FCSTD DOCUMENT  (FreeCAD 0.21R)
Label: MMU
License: All rights reserved
LicenseURL: http://en.wikipedia.org/wiki/All_rights_reserved
objects: Sketcher::SketchObject×75, Part::Feature×72, PartDesign::Pad×33, PartDesign::Pocket×28, PartDesign::Body×21, App::Part×17, Part::FeaturePython×10, PartDesign::Chamfer×8, PartDesign::PolarPattern×5, Mesh::Feature×2, PartDesign::FeatureBase×2, PartDesign::Groove×1, Spreadsheet::Sheet×1, PartDesign::AdditiveLoft×1, PartDesign::SubtractivePipe×1, PartDesign::Fillet×1
note: 331 computed .brp shape members not serialized (recipe doc carries the construction recipe); baked Part::Feature solids carry a one-line shape summary decoded from their .brp

FEATURE [Sketcher::SketchObject] Sketch
  FullyConstrained = true
  MapMode = 5
  Support = -> [XY_Plane]
  expr: Constraints[33] = 34mm
  expr: Constraints[46] = 6mm
  expr: Constraints[47] = Spreadsheet.FilamentTopPathOffset
  expr: Constraints[7] = 2mm
  sketch-geometry (21):
    g0: Circle CenterX=0 CenterY=0 CenterZ=0 NormalX=0 NormalY=0 NormalZ=1 AngleXU=0 Radius=17
    g1: Circle CenterX=0 CenterY=13.208 CenterZ=0 NormalX=0 NormalY=0 NormalZ=1 AngleXU=0 Radius=1
    g2: Circle CenterX=0 CenterY=-13.208 CenterZ=0 NormalX=0 NormalY=0 NormalZ=1 AngleXU=0 Radius=1
    g3: Circle CenterX=-11.4385 CenterY=6.604 CenterZ=0 NormalX=0 NormalY=0 NormalZ=1 AngleXU=0 Radius=1
    g4: Circle CenterX=11.4385 CenterY=6.604 CenterZ=0 NormalX=0 NormalY=0 NormalZ=1 AngleXU=0 Radius=1
    g5: Circle CenterX=11.4385 CenterY=-6.604 CenterZ=0 NormalX=0 NormalY=0 NormalZ=1 AngleXU=0 Radius=1
    g6: Circle CenterX=-11.4385 CenterY=-6.604 CenterZ=0 NormalX=0 NormalY=0 NormalZ=1 AngleXU=0 Radius=1
    g7: LineSegment StartX=0 StartY=13.208 StartZ=0 EndX=-11.4385 EndY=6.604 EndZ=0
    g8: LineSegment StartX=-11.4385 StartY=6.604 StartZ=0 EndX=-11.4385 EndY=-6.604 EndZ=0
    g9: LineSegment StartX=-11.4385 StartY=-6.604 StartZ=0 EndX=0 EndY=-13.208 EndZ=0
    g10: LineSegment StartX=0 StartY=-13.208 StartZ=0 EndX=11.4385 EndY=-6.604 EndZ=0
    g11: LineSegment StartX=11.4385 StartY=-6.604 StartZ=0 EndX=11.4385 EndY=6.604 EndZ=0
    g12: LineSegment StartX=11.4385 StartY=6.604 StartZ=0 EndX=0 EndY=13.208 EndZ=0
    g13: Circle CenterX=0 CenterY=0 CenterZ=0 NormalX=0 NormalY=0 NormalZ=1 AngleXU=0 Radius=13.208
    g14: GeomPoint X=0 Y=17 Z=0
    g15: Circle CenterX=-11.4385 CenterY=6.604 CenterZ=0 NormalX=0 NormalY=0 NormalZ=1 AngleXU=0 Radius=3
    g16: Circle CenterX=0 CenterY=13.208 CenterZ=0 NormalX=0 NormalY=0 NormalZ=1 AngleXU=0 Radius=3
    g17: Circle CenterX=11.4385 CenterY=6.604 CenterZ=0 NormalX=0 NormalY=0 NormalZ=1 AngleXU=0 Radius=3
    g18: Circle CenterX=-11.4385 CenterY=-6.604 CenterZ=0 NormalX=0 NormalY=0 NormalZ=1 AngleXU=0 Radius=3
    g19: Circle CenterX=0 CenterY=-13.208 CenterZ=0 NormalX=0 NormalY=0 NormalZ=1 AngleXU=0 Radius=3
    g20: Circle CenterX=11.4385 CenterY=-6.604 CenterZ=0 NormalX=0 NormalY=0 NormalZ=1 AngleXU=0 Radius=3
  constraints (44):
    c: Coincident(g0,g-1)
    c: PointOnObject(g1,g-2)
    c: PointOnObject(g2,g-2)
    c: Equal(g3,g1)
    c: Equal(g5,g2)
    c: Equal(g2,g6)
    c: Equal(g6,g3)
    c: Diameter(g1) = 2
    c: Coincident(g7,g8)
    c: Coincident(g8,g9)
    c: Coincident(g9,g10)
    c: Coincident(g10,g11)
    c: Coincident(g11,g12)
    c: Coincident(g12,g7)
    c: Equal(g7, g8-g12) x5
    c: PointOnObject(g7,g13)
    c: PointOnObject(g8,g13)
    c: PointOnObject(g9,g13)
    c: PointOnObject(g10,g13)
    c: PointOnObject(g12,g13)
    c: Coincident(g13,g0)
    c: Coincident(g12,g1)
    c: Coincident(g3,g7)
    c: Coincident(g8,g6)
    c: Coincident(g2,g9)
    c: Coincident(g5,g10)
    c: Coincident(g4,g11)
    c: PointOnObject(g14,g0)
    c: PointOnObject(g14,g-2)
    c: Diameter(g0) = 34
    c: Equal(g4,g1)
    c: Coincident(g15,g3)
    c: Coincident(g16,g1)
    c: Coincident(g17,g4)
    c: Coincident(g18,g6)
    c: Coincident(g19,g2)
    c: Coincident(g20,g5)
    c: Equal(g20,g17)
    c: Equal(g17,g16)
    c: Equal(g16,g15)
    c: Equal(g15,g18)
    c: Equal(g18,g19)
    c: Diameter(g16) = 6
    c: DistanceY(g0,g1) = 13.208
FEATURE [PartDesign::Pad] Pad
  Direction = (0,0,1)
  Length = 38.1
  Length2 = 9.906
  Profile = -> Sketch
  ReferenceAxis = -> Sketch [N_Axis]
  Type = 0
FEATURE [Sketcher::SketchObject] Sketch001
  FullyConstrained = false
  MapMode = 5
  Placement = pos=(0,0,0) rot=(1,0,0;1.5708rad)
  Support = -> [XZ_Plane]
  sketch-geometry (4):
    g0: ArcOfCircle CenterX=-17.564 CenterY=26.2819 CenterZ=0 NormalX=0 NormalY=0 NormalZ=1 AngleXU=0 Radius=4.064 StartAngle=3.14159 EndAngle=6.28319
    g1: ArcOfCircle CenterX=-17.564 CenterY=30.52 CenterZ=0 NormalX=0 NormalY=0 NormalZ=1 AngleXU=0 Radius=4.064 StartAngle=3e-16 EndAngle=3.14159
    g2: LineSegment StartX=-13.5 StartY=26.2819 StartZ=0 EndX=-13.5 EndY=30.52 EndZ=0
    g3: LineSegment StartX=-21.628 StartY=30.52 StartZ=0 EndX=-21.628 EndY=26.2819 EndZ=0
  constraints (8):
    c: Tangent(g0,g2) = -1.5708
    c: Tangent(g2,g1) = -1.5708
    c: Tangent(g1,g3) = -1.5708
    c: Tangent(g3,g0) = -1.5708
    c: Equal(g0,g1)
    c: Vertical(g2)
    c: DistanceX(g1,g1) = 4.064
    c: DistanceX(g0,g-1) = 13.5
FEATURE [PartDesign::Groove] Groove
  Angle = 360
  Axis = (0,-2e-16,1)
  Base = (0,0,0)
  BaseFeature = -> Pad
  Profile = -> Sketch001
  ReferenceAxis = -> Sketch001 [V_Axis]
  Reversed = true
FEATURE [Sketcher::SketchObject] Sketch002
  FullyConstrained = false
  MapMode = 5
  Placement = pos=(0,0,0) rot=(0.57735,0.57735,0.57735;2.0944rad)
  Support = -> [YZ_Plane]
  expr: Constraints[6] = Spreadsheet.IdlerBearingZ
  expr: Constraints[7] = Spreadsheet.IdlerBearingOffset
  expr: Constraints[8] = 7mm
  sketch-geometry (4):
    g0: ArcOfCircle CenterX=-15.9643 CenterY=27.94 CenterZ=0 NormalX=0 NormalY=0 NormalZ=1 AngleXU=0 Radius=3.31487 StartAngle=1.5708 EndAngle=4.71239
    g1: ArcOfCircle CenterX=-9.652 CenterY=27.94 CenterZ=0 NormalX=0 NormalY=0 NormalZ=1 AngleXU=0 Radius=3.31487 StartAngle=4.71239 EndAngle=7.85398
    g2: LineSegment StartX=-15.9643 StartY=24.6251 StartZ=0 EndX=-9.652 EndY=24.6251 EndZ=0
    g3: LineSegment StartX=-9.652 StartY=31.2549 StartZ=0 EndX=-15.9643 EndY=31.2549 EndZ=0
  constraints (9):
    c: Tangent(g0,g2) = -1.5708
    c: Tangent(g2,g1) = -1.5708
    c: Tangent(g1,g3) = -1.5708
    c: Tangent(g3,g0) = -1.5708
    c: Equal(g0,g1)
    c: Horizontal(g2)
    c: DistanceY(g-1,g0) = 27.94
    c: DistanceX(g1,g-1) = 9.652
    c: Diameter(g1) = 6.62974
FEATURE [PartDesign::Pocket] Pocket
  BaseFeature = -> Groove
  Direction = (-1,2e-16,-3e-16)
  Length = 2.794
  Length2 = 5.08
  Midplane = true
  Profile = -> Sketch002
  ReferenceAxis = -> Sketch002 [N_Axis]
  Type = 0
  expr: Length = Spreadsheet.IdlerBearingWidth + 0.01"
FEATURE [PartDesign::PolarPattern] PolarPattern
  Angle = 360
  Axis = -> Z_Axis
  BaseFeature = -> Pocket
  Occurrences = 6
  Originals = -> [Pocket]
FEATURE [Part::Feature] Part__Feature  label="Hobbed Shaft"
  shape: bbox 9.206 x 11 x 9.227 mm, 71 faces (baked)
FEATURE [Sketcher::SketchObject] Sketch003
  AttachmentOffset = pos=(0,0,7.62) rot=(0,0,1;0rad)
  FullyConstrained = false
  MapMode = 5
  Placement = pos=(0,-7.62,-1.7e-15) rot=(1,0,0;1.5708rad)
  Support = -> [XZ_Plane002]
  sketch-geometry (16):
    g0: ArcOfCircle CenterX=-39.2362 CenterY=0.297645 CenterZ=0 NormalX=0 NormalY=0 NormalZ=1 AngleXU=0 Radius=8.97278 StartAngle=2.89527 EndAngle=6.14074
    g1: LineSegment StartX=-41.3063 StartY=28.862 StartZ=0 EndX=-47.9381 EndY=2.48557 EndZ=0
    g2: LineSegment StartX=-30.3543 StartY=-0.976169 StartZ=0 EndX=-27.6367 EndY=17.9726 EndZ=0
    g3: Circle CenterX=-39.2362 CenterY=0.297645 CenterZ=0 NormalX=0 NormalY=0 NormalZ=1 AngleXU=0 Radius=6.05
    g4: Circle CenterX=-17.75 CenterY=27.75 CenterZ=0 NormalX=0 NormalY=0 NormalZ=1 AngleXU=0 Radius=2.56662
    g5: Circle CenterX=-8.40876 CenterY=42.3503 CenterZ=0 NormalX=0 NormalY=0 NormalZ=1 AngleXU=0 Radius=2.032
    g6: Circle CenterX=-11.4193 CenterY=18.5398 CenterZ=0 NormalX=0 NormalY=0 NormalZ=1 AngleXU=0 Radius=2.032
    g7: Circle CenterX=-32.2192 CenterY=45.3608 CenterZ=0 NormalX=0 NormalY=0 NormalZ=1 AngleXU=0 Radius=2.032
    g8: Circle CenterX=-35.2297 CenterY=21.5503 CenterZ=0 NormalX=0 NormalY=0 NormalZ=1 AngleXU=0 Radius=2.032
    g9: LineSegment StartX=-32.2192 StartY=45.3608 StartZ=0 EndX=-8.40876 EndY=42.3503 EndZ=0
    g10: LineSegment StartX=-8.40876 StartY=42.3503 StartZ=0 EndX=-11.4193 EndY=18.5398 EndZ=0
    g11: LineSegment StartX=-11.4193 StartY=18.5398 StartZ=0 EndX=-35.2297 EndY=21.5503 EndZ=0
    g12: LineSegment StartX=-35.2297 StartY=21.5503 StartZ=0 EndX=-32.2192 EndY=45.3608 EndZ=0
    g13: LineSegment StartX=-27.6367 StartY=17.9726 StartZ=0 EndX=-14.5474 EndY=23.3304 EndZ=0
    g14: LineSegment StartX=-17.6166 StartY=33.2063 StartZ=0 EndX=-41.3063 EndY=28.862 EndZ=0
    g15: ArcOfCircle CenterX=-17.75 CenterY=27.75 CenterZ=0 NormalX=0 NormalY=0 NormalZ=1 AngleXU=0 Radius=5.45795 StartAngle=5.33945 EndAngle=7.82954
  constraints (28):
    c: Tangent(g1,g0) = -1.5708
    c: Tangent(g0,g2) = -1.5708
    c: Coincident(g3,g0)
    c: Diameter(g3) = 12.1
    c: Coincident(g9,g7)
    c: Coincident(g9,g5)
    c: Coincident(g10,g5)
    c: Coincident(g10,g6)
    c: Coincident(g10,g11)
    c: Coincident(g11,g8)
    c: Coincident(g11,g12)
    c: Coincident(g12,g7)
    c: Equal(g5,g7)
    c: Equal(g7,g6)
    c: Equal(g6,g8)
    c: Perpendicular(g9,g10)
    c: Perpendicular(g11,g10)
    c: Perpendicular(g9,g12)
    c: Equal(g9,g12)
    c: Distance(g10) = 24
    c: Diameter(g6) = 4.064
    c: Coincident(g13,g2)
    c: Coincident(g14,g1)
    c: Coincident(g15,g4)
    c: Coincident(g15,g14)
    c: Coincident(g15,g13)
    c: DistanceY(g-1,g4) = 27.75
    c: DistanceX(g4,g-1) = 17.75
FEATURE [PartDesign::Pad] Pad001
  Direction = (0,-1,-2e-16)
  Length = 17.5
  Length2 = 9.906
  Placement = pos=(0,0,0) rot=(1,0,0;1.5708rad)
  Profile = -> Sketch003
  ReferenceAxis = -> Sketch003 [N_Axis]
  Type = 0
FEATURE [Part::Feature] Part__Feature001  label="SOLID"
  shape: bbox 4 x 34.64 x 34.64 mm, 32 faces (baked)
FEATURE [Part::Feature] Part__Feature002  label="SOLID001"
  shape: bbox 4 x 29.63 x 29.63 mm, 16 faces (baked)
FEATURE [Part::Feature] Part__Feature003  label="SOLID002"
  shape: bbox 0.356 x 33.1 x 33.1 mm, 26 faces (baked)
FEATURE [Part::Feature] Part__Feature004  label="SOLID003"
  shape: bbox 0.356 x 33.1 x 33.1 mm, 26 faces (baked)
FEATURE [Part::Feature] Part__Feature005  label="SOLID004"
  shape: bbox 1.588 x 29.93 x 30.01 mm, 88 faces (baked)
FEATURE [App::Part] bearing_w_61705_2rs1_2_1  label="bearing_w_61705-2rs1_2_1"
  Group = -> [Part__Feature001,Part__Feature002,Part__Feature003,Part__Feature004,Part__Feature005]
  Origin = -> Origin004
  Placement = pos=(-2.5e-15,0,10.9982) rot=(0,1,0;1.5708rad)
FEATURE [Part::Feature] Part__Feature006  label="SOLID005"
  shape: bbox 0.356 x 33.1 x 33.1 mm, 26 faces (baked)
FEATURE [Part::Feature] Part__Feature007  label="SOLID006"
  shape: bbox 4 x 29.63 x 29.63 mm, 16 faces (baked)
FEATURE [Part::Feature] Part__Feature008  label="SOLID007"
  shape: bbox 4 x 34.64 x 34.64 mm, 32 faces (baked)
FEATURE [Part::Feature] Part__Feature009  label="SOLID008"
  shape: bbox 1.588 x 29.93 x 30.01 mm, 88 faces (baked)
FEATURE [Part::Feature] Part__Feature010  label="SOLID009"
  shape: bbox 0.356 x 33.1 x 33.1 mm, 26 faces (baked)
FEATURE [App::Part] bearing_w_61705_2rs1_2_002  label="bearing_w_61705-2rs1_2_002"
  Group = -> [Part__Feature008,Part__Feature007,Part__Feature010,Part__Feature006,Part__Feature009]
  Origin = -> Origin005
  Placement = pos=(4e-15,0,-17.9578) rot=(0,1,0;1.5708rad)
FEATURE [Sketcher::SketchObject] Sketch004
  FullyConstrained = false
  MapMode = 5
  Support = -> [XY_Plane006]
  sketch-geometry (1):
    g0: Circle CenterX=0 CenterY=0 CenterZ=0 NormalX=0 NormalY=0 NormalZ=1 AngleXU=0 Radius=14.3648
  constraints (1):
    c: Coincident(g0,g-1)
FEATURE [PartDesign::Pad] Pad002
  Direction = (0,0,1)
  Length = 6.35
  Length2 = 9.906
  Profile = -> Sketch004
  ReferenceAxis = -> Sketch004 [N_Axis]
  Type = 0
FEATURE [Sketcher::SketchObject] Sketch005
  FullyConstrained = false
  MapMode = 5
  Support = -> [XY_Plane006]
  sketch-geometry (5):
    g0: Circle CenterX=0 CenterY=0 CenterZ=0 NormalX=0 NormalY=0 NormalZ=1 AngleXU=0 Radius=14.3648
    g1: ArcOfCircle CenterX=-14.7291 CenterY=0 CenterZ=0 NormalX=0 NormalY=0 NormalZ=1 AngleXU=0 Radius=0.120334 StartAngle=1.5708 EndAngle=4.71239
    g2: LineSegment StartX=-14.7291 StartY=0.120334 StartZ=0 EndX=-14.2261 EndY=0.205585 EndZ=0
    g3: LineSegment StartX=-14.2261 StartY=0.205585 StartZ=0 EndX=-14.2261 EndY=-0.205585 EndZ=0
    g4: LineSegment StartX=-14.2261 StartY=-0.205585 StartZ=0 EndX=-14.7291 EndY=-0.120334 EndZ=0
  constraints (10):
    c: Coincident(g0,g-1)
    c: Block(g0)
    c: PointOnObject(g1,g-1)
    c: Vertical(g1,g1)
    c: Vertical(g1,g1)
    c: Coincident(g2,g1)
    c: Coincident(g3,g2)
    c: Coincident(g4,g3)
    c: Coincident(g4,g1)
    c: Symmetric(g2,g3,g-1)
FEATURE [PartDesign::Pad] Pad003
  BaseFeature = -> Pad002
  Direction = (0,0,1)
  Length = 6.35
  Length2 = 9.906
  Profile = -> Sketch005
  ReferenceAxis = -> Sketch005 [N_Axis]
  Type = 0
FEATURE [PartDesign::PolarPattern] PolarPattern001
  Angle = 360
  Axis = -> Sketch005 [N_Axis]
  BaseFeature = -> Pad003
  Occurrences = 100
  Originals = -> [Pad003]
FEATURE [PartDesign::Body] Body002  label="RotateTeeth"
  Group = -> [Sketch004,Pad002,Sketch005,Pad003,PolarPattern001]
  Origin = -> Origin006
  Placement = pos=(0,0,-11.5062) rot=(0,0,1;0rad)
  Tip = -> PolarPattern001
FEATURE [Sketcher::SketchObject] Sketch006
  AttachmentOffset = pos=(0,0,12.7) rot=(0,0,1;0rad)
  FullyConstrained = true
  MapMode = 5
  Placement = pos=(0,0,12.7) rot=(0,0,1;0rad)
  Support = -> [XY_Plane007]
  expr: Constraints[2] = 30mm
  sketch-geometry (2):
    g0: Circle CenterX=0 CenterY=0 CenterZ=0 NormalX=0 NormalY=0 NormalZ=1 AngleXU=0 Radius=18.5
    g1: Circle CenterX=0 CenterY=0 CenterZ=0 NormalX=0 NormalY=0 NormalZ=1 AngleXU=0 Radius=15
  constraints (4):
    c: Coincident(g0,g-1)
    c: Coincident(g1,g0)
    c: Diameter(g1) = 30
    c: Diameter(g0) = 37
FEATURE [PartDesign::Pad] Pad004
  Direction = (0,0,1)
  Length = 7.62
  Length2 = 9.906
  Profile = -> Sketch006
  ReferenceAxis = -> Sketch006 [N_Axis]
  Type = 0
FEATURE [Sketcher::SketchObject] Sketch007
  AttachmentOffset = pos=(0,0,12.7) rot=(0,0,1;0rad)
  FullyConstrained = false
  MapMode = 5
  Placement = pos=(0,0,12.7) rot=(0,0,1;0rad)
  Support = -> [XY_Plane007]
  expr: Constraints[2] = 34mm / 2
  sketch-geometry (9):
    g0: LineSegment StartX=-1 StartY=17 StartZ=0 EndX=1 EndY=17 EndZ=0
    g1: GeomPoint X=0 Y=17 Z=0
    g2: LineSegment StartX=4.50856 StartY=19 StartZ=0 EndX=-4.50856 EndY=19 EndZ=0
    g3: ArcOfCircle CenterX=-1 CenterY=20.3275 CenterZ=0 NormalX=0 NormalY=0 NormalZ=1 AngleXU=0 Radius=3.32752 StartAngle=4.15708 EndAngle=4.71239
    g4: ArcOfCircle CenterX=1 CenterY=20.3275 CenterZ=0 NormalX=0 NormalY=0 NormalZ=1 AngleXU=0 Radius=3.32752 StartAngle=4.71239 EndAngle=5.2677
    g5: ArcOfCircle CenterX=-4.50857 CenterY=14.6725 CenterZ=0 NormalX=0 NormalY=0 NormalZ=1 AngleXU=0 Radius=3.32752 StartAngle=1.01549 EndAngle=1.5708
    g6: ArcOfCircle CenterX=4.50857 CenterY=14.6725 CenterZ=0 NormalX=0 NormalY=0 NormalZ=1 AngleXU=0 Radius=3.32752 StartAngle=1.5708 EndAngle=2.1261
    g7: LineSegment StartX=-4.50857 StartY=18 StartZ=0 EndX=-4.50856 EndY=19 EndZ=0
    g8: LineSegment StartX=4.50856 StartY=18 StartZ=0 EndX=4.50856 EndY=19 EndZ=0
  constraints (23):
    c: Horizontal(g0)
    c: PointOnObject(g1,g-2)
    c: DistanceY(g-1,g1) = 17
    c: Symmetric(g2,g2,g-2)
    c: DistanceX(g2,g2) = 9.01713
    c: Tangent(g0,g3) = -1.5708
    c: Tangent(g0,g4) = -1.5708
    c: Equal(g3,g4)
    c: Symmetric(g0,g0,g1)
    c: Equal(g6,g5)
    c: DistanceX(g0,g0) = 2
    c: Tangent(g5,g3) = 1.5708
    c: Tangent(g6,g4) = 1.5708
    c: Horizontal(g4,g3)
    c: Horizontal(g5,g6)
    c: Coincident(g7,g5)
    c: Coincident(g2,g7)
    c: Coincident(g8,g6)
    c: Coincident(g8,g2)
    c: Vertical(g8)
    c: Vertical(g5,g5)
    c: DistanceY(g1,g5) = 1
    c: Equal(g5,g3)
FEATURE [PartDesign::Pocket] Pocket001
  BaseFeature = -> Pad004
  Direction = (0,0,-1)
  Length = 25.4
  Length2 = 5.08
  Profile = -> Sketch007
  ReferenceAxis = -> Sketch007 [N_Axis]
  Reversed = true
  Type = 0
FEATURE [PartDesign::PolarPattern] PolarPattern002
  Angle = 360
  Axis = -> Z_Axis007
  BaseFeature = -> Pocket001
  Occurrences = 6
  Originals = -> [Pocket001]
FEATURE [Part::Feature] Part__Feature011  label="SOLID010"
  shape: bbox 4 x 10.82 x 10.82 mm, 32 faces (baked)
FEATURE [Part::Feature] Part__Feature012  label="SOLID011"
  shape: bbox 4 x 5.209 x 5.209 mm, 16 faces (baked)
FEATURE [Part::Feature] Part__Feature013  label="SOLID012"
  shape: bbox 1.588 x 7.234 x 7.379 mm, 28 faces (baked)
FEATURE [App::Part] bearing_623_2_1
  Group = -> [Part__Feature011,Part__Feature012,Part__Feature013]
  Origin = -> Origin009
  Placement = pos=(-21.3266,0,12.9066) rot=(0,1,0;4.71239rad)
FEATURE [Part::Feature] Part__Feature015  label="pc4-m6"
  Placement = pos=(-11.4808,7.1374,37.719) rot=(0,0,1;0rad)
  shape: bbox 11.55 x 11.55 x 20.8 mm, 84 faces (baked)
FEATURE [Part::Feature] Part__Feature016  label="pc4-m007"
  Placement = pos=(-11.42,-6.17,37.59) rot=(0,0,1;0rad)
  shape: bbox 11.55 x 11.55 x 20.8 mm, 84 faces (baked)
FEATURE [Part::Feature] Part__Feature017  label="pc4-m008"
  Placement = pos=(-0.28,-12.73,37.59) rot=(0,0,1;0rad)
  shape: bbox 11.55 x 11.55 x 20.8 mm, 84 faces (baked)
FEATURE [Part::Feature] Part__Feature018  label="pc4-m009"
  Placement = pos=(11.28,-6.65,37.59) rot=(0,0,1;0rad)
  shape: bbox 11.55 x 11.55 x 20.8 mm, 84 faces (baked)
FEATURE [Part::Feature] Part__Feature019  label="pc4-m010"
  Placement = pos=(-0.03,13.18,37.59) rot=(0,0,1;0rad)
  shape: bbox 11.55 x 11.55 x 20.8 mm, 84 faces (baked)
FEATURE [Part::Feature] Part__Feature020  label="pc4-m011"
  Placement = pos=(11.68,6.96,37.59) rot=(0,0,1;0rad)
  shape: bbox 11.55 x 11.55 x 20.8 mm, 84 faces (baked)
FEATURE [App::Part] Part002  label="Couplings"
  Group = -> [Part__Feature015,Part__Feature016,Part__Feature017,Part__Feature018,Part__Feature019,Part__Feature020]
  Origin = -> Origin010
FEATURE [Sketcher::SketchObject] Sketch008
  FullyConstrained = false
  MapMode = 5
  Support = -> [XY_Plane]
  expr: Constraints[1] = 25mm
  sketch-geometry (2):
    g0: Circle CenterX=0 CenterY=0 CenterZ=0 NormalX=0 NormalY=0 NormalZ=1 AngleXU=0 Radius=12.5
    g1: Circle CenterX=0 CenterY=0 CenterZ=0 NormalX=0 NormalY=0 NormalZ=1 AngleXU=0 Radius=21.9399
  constraints (3):
    c: Coincident(g0,g-1)
    c: Diameter(g0) = 25
    c: Coincident(g1,g0)
FEATURE [PartDesign::Pocket] Pocket002
  BaseFeature = -> PolarPattern
  Direction = (0,0,-1)
  Length = 11.43
  Length2 = 5.08
  Profile = -> Sketch008
  ReferenceAxis = -> Sketch008 [N_Axis]
  Reversed = true
  Type = 0
FEATURE [Sketcher::SketchObject] Sketch009
  FullyConstrained = false
  MapMode = 5
  Support = -> [XY_Plane011]
  expr: Constraints[9] = Spreadsheet.PivotFrameRadius
  sketch-geometry (11):
    g0: Circle CenterX=0 CenterY=0 CenterZ=0 NormalX=0 NormalY=0 NormalZ=1 AngleXU=0 Radius=15.75
    g1: ArcOfCircle CenterX=0 CenterY=0 CenterZ=0 NormalX=0 NormalY=0 NormalZ=1 AngleXU=0 Radius=41.91 StartAngle=4.51427 EndAngle=7.25357
    g2: LineSegment StartX=23.6783 StartY=34.5801 StartZ=0 EndX=5.00879 EndY=47.3638 EndZ=0
    g3: LineSegment StartX=-64.4109 StartY=-29.8155 StartZ=0 EndX=-8.24899 EndY=-41.0902 EndZ=0
    g4: LineSegment StartX=-23.0323 StartY=57.2349 StartZ=0 EndX=-57.988 EndY=28.0376 EndZ=0
    g5: LineSegment StartX=5.00879 StartY=47.3638 StartZ=0 EndX=-23.0323 EndY=57.2349 EndZ=0
    g6: LineSegment StartX=-57.988 StartY=28.0376 StartZ=0 EndX=-64.4109 EndY=-29.8155 EndZ=0
    g7: ArcOfCircle CenterX=-49.1729 CenterY=-13.0622 CenterZ=0 NormalX=0 NormalY=0 NormalZ=1 AngleXU=0 Radius=3.72272 StartAngle=1.5708 EndAngle=4.71239
    g8: ArcOfCircle CenterX=-35.7364 CenterY=-13.0622 CenterZ=0 NormalX=0 NormalY=0 NormalZ=1 AngleXU=0 Radius=3.72272 StartAngle=4.71239 EndAngle=7.85398
    g9: LineSegment StartX=-49.1729 StartY=-16.7849 StartZ=0 EndX=-35.7364 EndY=-16.7849 EndZ=0
    g10: LineSegment StartX=-35.7364 StartY=-9.33949 StartZ=0 EndX=-49.1729 EndY=-9.33949 EndZ=0
  constraints (16):
    c: Coincident(g0,g-1)
    c: Diameter(g0) = 31.5
    c: Tangent(g1,g2) = -1.5708
    c: Tangent(g3,g1) = -1.5708
    c: Coincident(g1,g0)
    c: Coincident(g5,g2)
    c: Coincident(g5,g4)
    c: Coincident(g6,g4)
    c: Coincident(g6,g3)
    c: Diameter(g1) = 83.82
    c: Tangent(g7,g9) = -1.5708
    c: Tangent(g9,g8) = -1.5708
    c: Tangent(g8,g10) = -1.5708
    c: Tangent(g10,g7) = -1.5708
    c: Equal(g7,g8)
    c: Horizontal(g9)
FEATURE [PartDesign::Pad] Pad005
  Direction = (0,0,1)
  Length = 8.89
  Length2 = 9.906
  Profile = -> Sketch009
  ReferenceAxis = -> Sketch009 [N_Axis]
  Type = 0
FEATURE [Sketcher::SketchObject] Sketch010
  FullyConstrained = false
  MapMode = 5
  Placement = pos=(0,0,0) rot=(1,0,0;1.5708rad)
  Support = -> [XZ_Plane011]
  sketch-geometry (4):
    g0: LineSegment StartX=-46.7628 StartY=29.512 StartZ=0 EndX=-59.6542 EndY=8.89 EndZ=0
    g1: LineSegment StartX=-46.7628 StartY=29.512 StartZ=0 EndX=-32.037 EndY=29.512 EndZ=0
    g2: LineSegment StartX=-32.037 StartY=29.512 StartZ=0 EndX=-34.8413 EndY=8.89 EndZ=0
    g3: LineSegment StartX=-34.8413 StartY=8.89 StartZ=0 EndX=-59.6542 EndY=8.89 EndZ=0
  constraints (7):
    c: Coincident(g1,g0)
    c: Coincident(g2,g1)
    c: Coincident(g3,g2)
    c: Coincident(g3,g0)
    c: Horizontal(g3)
    c: Horizontal(g1)
    c: DistanceY(g-1,g0) = 8.89
FEATURE [PartDesign::Pad] Pad006
  BaseFeature = -> Pad005
  Direction = (0,-1,-2e-16)
  Length = 7.62
  Length2 = 9.906
  Profile = -> Sketch010
  ReferenceAxis = -> Sketch010 [N_Axis]
  Type = 0
FEATURE [Sketcher::SketchObject] Sketch011
  AttachmentOffset = pos=(0,0,7.62) rot=(0,0,1;0rad)
  FullyConstrained = false
  MapMode = 5
  Placement = pos=(0,-7.62,-1.7e-15) rot=(1,0,0;1.5708rad)
  Support = -> [XZ_Plane011]
  sketch-geometry (1):
    g0: Circle CenterX=-39.2583 CenterY=22.0028 CenterZ=0 NormalX=0 NormalY=0 NormalZ=1 AngleXU=0 Radius=6
  constraints (1):
    c: Diameter(g0) = 12
FEATURE [PartDesign::Pad] Pad007
  BaseFeature = -> Pad006
  Direction = (0,-1,-2e-16)
  Length = 10.16
  Length2 = 9.906
  Profile = -> Sketch011
  ReferenceAxis = -> Sketch011 [N_Axis]
  Type = 0
FEATURE [Spreadsheet::Sheet] Spreadsheet
  cells = A1(IdlerBearingOffset)==0.38"; B1=IdlerBearingOffset; A2(IdlerBearingZ)==1.1"; B2=IdlerBearingZ; A3(IdlerBearingWidth)==0.1"; B3=IdlerBearingWidth; A4(FilamentTopPathOffset)==0.52"; B4=FilamentTopPathOffset; A5(FilamentBottomPathOffset)==0.4"; B5=FilamentBottomPathOffset; A6(PivotFrameRadius)==3.3"; B6=PivotFrameRadius
FEATURE [Sketcher::SketchObject] Sketch014
  FullyConstrained = false
  MapMode = 5
  Placement = pos=(0,0,0) rot=(0.57735,0.57735,0.57735;2.0944rad)
  Support = -> [YZ_Plane]
  expr: Constraints[6] = Spreadsheet.IdlerBearingZ
  expr: Constraints[7] = Spreadsheet.IdlerBearingOffset
  expr: Constraints[8] = 3.1mm
  sketch-geometry (4):
    g0: ArcOfCircle CenterX=-9.652 CenterY=27.94 CenterZ=0 NormalX=0 NormalY=0 NormalZ=1 AngleXU=0 Radius=1.65282 StartAngle=4.71239 EndAngle=7.85398
    g1: ArcOfCircle CenterX=-14.0387 CenterY=27.94 CenterZ=0 NormalX=0 NormalY=0 NormalZ=1 AngleXU=0 Radius=1.65282 StartAngle=1.5708 EndAngle=4.71239
    g2: LineSegment StartX=-9.652 StartY=29.5928 StartZ=0 EndX=-14.0387 EndY=29.5928 EndZ=0
    g3: LineSegment StartX=-14.0387 StartY=26.2872 StartZ=0 EndX=-9.652 EndY=26.2872 EndZ=0
  constraints (9):
    c: Tangent(g0,g2) = -1.5708
    c: Tangent(g2,g1) = -1.5708
    c: Tangent(g1,g3) = -1.5708
    c: Tangent(g3,g0) = -1.5708
    c: Equal(g0,g1)
    c: Horizontal(g2)
    c: DistanceY(g-1,g0) = 27.94
    c: DistanceX(g0,g-1) = 9.652
    c: Diameter(g0) = 3.30563
FEATURE [PartDesign::Pocket] Pocket003
  BaseFeature = -> Pocket002
  Direction = (-1,2e-16,-3e-16)
  Length = 10.16
  Length2 = 5.08
  Midplane = true
  Profile = -> Sketch014
  ReferenceAxis = -> Sketch014 [N_Axis]
  Type = 0
FEATURE [PartDesign::PolarPattern] PolarPattern004
  Angle = 360
  Axis = -> Z_Axis
  BaseFeature = -> Pocket003
  Occurrences = 6
  Originals = -> [Pocket003]
FEATURE [Part::Feature] Part__Feature042  label="7804K124_Stainless Steel Ball Bearing"
  Placement = pos=(0,9.652,27.94) rot=(0,1,0;1.5708rad)
  shape: bbox 2.5 x 6.119 x 6.119 mm, 66 faces, 16 solids (baked)
  expr: .Placement.Base.y = Spreadsheet.IdlerBearingOffset
  expr: .Placement.Base.z = Spreadsheet.IdlerBearingZ
FEATURE [Part::Feature] Part__Feature043  label="7804K124_Stainless Steel Ball Bearing001"
  Placement = pos=(0.0508,-9.652,27.94) rot=(0,1,0;1.5708rad)
  shape: bbox 2.5 x 6.119 x 6.119 mm, 66 faces, 16 solids (baked)
  expr: .Placement.Base.y = -Spreadsheet.IdlerBearingOffset
  expr: .Placement.Base.z = Spreadsheet.IdlerBearingZ
FEATURE [Part::Feature] Part__Feature044  label="7804K124_Stainless Steel Ball Bearing002"
  Placement = pos=(-8.49085,4.89655,27.94) rot=(-0.447214,0.774597,0.447214;1.82348rad)
  shape: bbox 6.321 x 5.04 x 6.119 mm, 66 faces, 16 solids (baked)
  expr: .Placement.Base.z = Spreadsheet.IdlerBearingZ
FEATURE [Part::Feature] Part__Feature045  label="7804K124_Stainless Steel Ball Bearing003"
  Placement = pos=(8.7206,5.0292,27.94) rot=(0.447214,0.774597,-0.447214;1.82348rad)
  shape: bbox 6.321 x 5.04 x 6.119 mm, 66 faces, 16 solids (baked)
  expr: .Placement.Base.z = Spreadsheet.IdlerBearingZ
FEATURE [Part::Feature] Part__Feature046  label="7804K124_Stainless Steel Ball Bearing004"
  Placement = pos=(8.66678,-5.01741,27.94) rot=(-0.447214,0.774597,0.447214;1.82348rad)
  shape: bbox 6.321 x 5.04 x 6.119 mm, 66 faces, 16 solids (baked)
  expr: .Placement.Base.z = Spreadsheet.IdlerBearingZ
FEATURE [Part::Feature] Part__Feature047  label="7804K124_Stainless Steel Ball Bearing005"
  Placement = pos=(0,7.62,27.94) rot=(0,1,0;1.5708rad)
  shape: bbox 2.5 x 6.119 x 6.119 mm, 66 faces, 16 solids (baked)
  expr: .Placement.Base.z = Spreadsheet.IdlerBearingZ
FEATURE [Part::Feature] Part__Feature048  label="7804K124_Stainless Steel Ball Bearing006"
  Placement = pos=(-8.90125,-5.10522,27.94) rot=(0.447214,0.774597,-0.447214;1.82348rad)
  shape: bbox 6.321 x 5.04 x 6.119 mm, 66 faces, 16 solids (baked)
  expr: .Placement.Base.z = Spreadsheet.IdlerBearingZ
FEATURE [App::Part] Part003  label="Bearings"
  Group = -> [Part__Feature042,Part__Feature043,Part__Feature044,Part__Feature045,Part__Feature046,Part__Feature047,Part__Feature048]
  Origin = -> Origin013
FEATURE [Sketcher::SketchObject] Sketch019
  AttachmentOffset = pos=(0,0,38.1) rot=(0,0,1;1.5708rad)
  FullyConstrained = true
  MapMode = 5
  Placement = pos=(0,0,38.1) rot=(0,0,1;1.5708rad)
  Support = -> [XY_Plane]
  expr: Constraints[2] = Spreadsheet.FilamentTopPathOffset
  sketch-geometry (1):
    g0: Circle CenterX=-13.208 CenterY=0 CenterZ=0 NormalX=0 NormalY=0 NormalZ=1 AngleXU=0 Radius=1.5
  constraints (3):
    c: PointOnObject(g0,g-1)
    c: Diameter(g0) = 3
    c: DistanceX(g0,g-1) = 13.208
FEATURE [Sketcher::SketchObject] Sketch020
  AttachmentOffset = pos=(0,0,20.32) rot=(0,0,1;1.5708rad)
  FullyConstrained = true
  MapMode = 5
  Placement = pos=(0,0,20.32) rot=(0,0,1;1.5708rad)
  Support = -> [XY_Plane]
  expr: Constraints[2] = Spreadsheet.FilamentTopPathOffset
  sketch-geometry (1):
    g0: Circle CenterX=-13.208 CenterY=0 CenterZ=0 NormalX=0 NormalY=0 NormalZ=1 AngleXU=0 Radius=1.5
  constraints (3):
    c: PointOnObject(g0,g-1)
    c: Diameter(g0) = 3
    c: DistanceX(g0,g-1) = 13.208
FEATURE [Sketcher::SketchObject] Sketch021
  AttachmentOffset = pos=(0,0,10.16) rot=(0,0,1;1.5708rad)
  FullyConstrained = true
  MapMode = 5
  Placement = pos=(0,0,10.16) rot=(0,0,1;1.5708rad)
  Support = -> [XY_Plane]
  expr: Constraints[2] = Spreadsheet.FilamentBottomPathOffset
  sketch-geometry (1):
    g0: Circle CenterX=-10.16 CenterY=0 CenterZ=0 NormalX=0 NormalY=0 NormalZ=1 AngleXU=0 Radius=1.5
  constraints (3):
    c: PointOnObject(g0,g-1)
    c: Diameter(g0) = 3
    c: DistanceX(g0,g-1) = 10.16
FEATURE [Sketcher::SketchObject] Sketch022
  AttachmentOffset = pos=(0,0,0) rot=(0,0,1;1.5708rad)
  FullyConstrained = true
  MapMode = 5
  Placement = pos=(0,0,0) rot=(0,0,1;1.5708rad)
  Support = -> [XY_Plane]
  expr: Constraints[2] = Spreadsheet.FilamentBottomPathOffset
  sketch-geometry (1):
    g0: Circle CenterX=-10.16 CenterY=0 CenterZ=0 NormalX=0 NormalY=0 NormalZ=1 AngleXU=0 Radius=1.5
  constraints (3):
    c: PointOnObject(g0,g-1)
    c: Diameter(g0) = 3
    c: DistanceX(g0,g-1) = 10.16
FEATURE [Part::FeaturePython] InvoluteGear  # WARN: FeaturePython — macro-defined, semantics opaque (R4)
  AttacherType = Attacher::AttachEngine3D
  Placement = pos=(-29,29,-12.217) rot=(0,0,1;0.174533rad)
  angular_backlash = 0
  backlash = 0
  beta = 0
  clearance = 0.25
  da = 22
  df = 17.5
  double_helix = false
  dw = 20
  head = 0
  head_fillet = 0
  height = 5
  module = 1
  numpoints = 6
  pressure_angle = 20
  properties_from_tool = false
  reversed_backlash = false
  root_fillet = 0
  shift = 0
  simple = false
  teeth = 20
  transverse_pitch = 3.14159
  undercut = false
  version = 0.0.4
  expr: angular_backlash = backlash / dw * 360° / pi
  expr: dw = teeth * module
FEATURE [Sketcher::SketchObject] Sketch023
  FullyConstrained = true
  MapMode = 5
  Support = -> [XY_Plane014]
  sketch-geometry (1):
    g0: Circle CenterX=0 CenterY=0 CenterZ=0 NormalX=0 NormalY=0 NormalZ=1 AngleXU=0 Radius=12.5
  constraints (2):
    c: Coincident(g0,g-1)
    c: Diameter(g0) = 25
FEATURE [Part::Feature] Part__Feature049  label="28BYJ-48 Side Enclosure"
  shape: bbox 28.01 x 19.21 x 28.01 mm, 67 faces (baked)
FEATURE [Part::Feature] Part__Feature050  label="28BYJ-48 Upper Enclosure"
  Placement = pos=(0,-19,0) rot=(0,0,1;3.14159rad)
  shape: bbox 42 x 3.4 x 29 mm, 63 faces (baked)
FEATURE [Part::Feature] Part__Feature051  label="28BYJ-48 Motor Wire Front Cover"
  Placement = pos=(1e-15,-19,-2e-15) rot=(0,0,1;0rad)
  shape: bbox 16.34 x 13.5 x 5.632 mm, 26 faces (baked)
FEATURE [Part::Feature] Part__Feature052  label="28BYJ-48 Dummy Wire"
  Placement = pos=(-4.3e-14,-17.25,-16.5) rot=(1,0,0;1.5708rad)
  shape: bbox 7 x 2 x 1 mm, 21 faces (baked)
FEATURE [Part::Feature] Part__Feature053  label="28BYJ-48 Motor Bearing Ring"
  Placement = pos=(2e-15,-20.25,8) rot=(0.99943,0,0.033769;3.14159rad)
  shape: bbox 7 x 2.5 x 7 mm, 4 faces (baked)
FEATURE [Part::Feature] Part__Feature054  label="28BYJ-48 Shaft"
  Placement = pos=(2e-15,-18,8) rot=(0,1,0;2.63043rad)
  shape: bbox 5.365 x 10 x 5 mm, 11 faces (baked)
FEATURE [Part::Feature] Part__Feature055  label="28BYJ-48 Lower Enclosure"
  Placement = pos=(0,-2e-15,0) rot=(0.682081,0,0.731277;3.14159rad)
  shape: bbox 26 x 1 x 26 mm, 3 faces (baked)
FEATURE [App::Part] _8BYJ_48_Stepper_Motor  label="28BYJ-48 Stepper Motor"
  Group = -> [Part__Feature049,Part__Feature050,Part__Feature051,Part__Feature052,Part__Feature053,Part__Feature054,Part__Feature055]
  Origin = -> Origin015
  Placement = pos=(-26.9748,73.5076,-39.4208) rot=(0.57735,-0.57735,0.57735;4.18879rad)
FEATURE [Sketcher::SketchObject] Sketch024
  FullyConstrained = true
  MapMode = 5
  Support = -> [XY_Plane011]
  expr: Constraints[16] = 22.1mm
  sketch-geometry (33):
    g0: LineSegment StartX=-30.9105 StartY=7.1631 StartZ=0 EndX=-7.1631 EndY=27.0895 EndZ=0
    g1: LineSegment StartX=-7.1631 StartY=27.0895 StartZ=0 EndX=-27.0895 EndY=50.8369 EndZ=0
    g2: LineSegment StartX=-27.0895 StartY=50.8369 StartZ=0 EndX=-50.8369 EndY=30.9105 EndZ=0
    g3: LineSegment StartX=-50.8369 StartY=30.9105 StartZ=0 EndX=-30.9105 EndY=7.1631 EndZ=0
    g4: GeomPoint X=-29 Y=29 Z=0
    g5: ArcOfCircle CenterX=-30.1429 CenterY=30.362 CenterZ=0 NormalX=0 NormalY=0 NormalZ=1 AngleXU=0 Radius=11.05 StartAngle=0.698132 EndAngle=3.83972
    g6: ArcOfCircle CenterX=-27.8571 CenterY=27.638 CenterZ=0 NormalX=0 NormalY=0 NormalZ=1 AngleXU=0 Radius=11.05 StartAngle=3.83972 EndAngle=6.98132
    g7: LineSegment StartX=-38.6077 StartY=23.2592 StartZ=0 EndX=-36.3219 EndY=20.5352 EndZ=0
    g8: LineSegment StartX=-19.3923 StartY=34.7408 StartZ=0 EndX=-21.6781 EndY=37.4648 EndZ=0
    g9: LineSegment StartX=-30.1429 StartY=30.362 StartZ=0 EndX=-29 EndY=29 EndZ=0
    g10: LineSegment StartX=-29 StartY=29 StartZ=0 EndX=-27.8571 EndY=27.638 EndZ=0
    g11: ArcOfCircle CenterX=-32.0534 CenterY=8.52513 CenterZ=0 NormalX=0 NormalY=0 NormalZ=1 AngleXU=0 Radius=1.55 StartAngle=0.698132 EndAngle=3.83972
    g12: ArcOfCircle CenterX=-29.7676 CenterY=5.80108 CenterZ=0 NormalX=0 NormalY=0 NormalZ=1 AngleXU=0 Radius=1.55 StartAngle=3.83972 EndAngle=6.98132
    g13: LineSegment StartX=-33.2407 StartY=7.52881 StartZ=0 EndX=-30.955 EndY=4.80476 EndZ=0
    g14: LineSegment StartX=-28.5802 StartY=6.7974 StartZ=0 EndX=-30.866 EndY=9.52145 EndZ=0
    g15: ArcOfCircle CenterX=-8.30598 CenterY=28.4515 CenterZ=0 NormalX=0 NormalY=0 NormalZ=1 AngleXU=0 Radius=1.55 StartAngle=0.698132 EndAngle=3.83972
    g16: ArcOfCircle CenterX=-6.02023 CenterY=25.7275 CenterZ=0 NormalX=0 NormalY=0 NormalZ=1 AngleXU=0 Radius=1.55 StartAngle=3.83972 EndAngle=6.98132
    g17: LineSegment StartX=-9.49335 StartY=27.4552 StartZ=0 EndX=-7.2076 EndY=24.7312 EndZ=0
    g18: LineSegment StartX=-4.83286 StartY=26.7238 StartZ=0 EndX=-7.11861 EndY=29.4479 EndZ=0
    g19: ArcOfCircle CenterX=-49.694 CenterY=29.5485 CenterZ=0 NormalX=0 NormalY=0 NormalZ=1 AngleXU=0 Radius=1.55 StartAngle=3.83972 EndAngle=6.98132
    g20: ArcOfCircle CenterX=-51.9798 CenterY=32.2725 CenterZ=0 NormalX=0 NormalY=0 NormalZ=1 AngleXU=0 Radius=1.55 StartAngle=0.698132 EndAngle=3.83972
    g21: LineSegment StartX=-48.5067 StartY=30.5448 StartZ=0 EndX=-50.7924 EndY=33.2688 EndZ=0
    g22: LineSegment StartX=-53.1671 StartY=31.2762 StartZ=0 EndX=-50.8814 EndY=28.5521 EndZ=0
    g23: ArcOfCircle CenterX=-25.9466 CenterY=49.4749 CenterZ=0 NormalX=0 NormalY=0 NormalZ=1 AngleXU=0 Radius=1.55 StartAngle=3.83972 EndAngle=6.98132
    g24: ArcOfCircle CenterX=-28.2324 CenterY=52.1989 CenterZ=0 NormalX=0 NormalY=0 NormalZ=1 AngleXU=0 Radius=1.55 StartAngle=0.698132 EndAngle=3.83972
    g25: LineSegment StartX=-24.7593 StartY=50.4712 StartZ=0 EndX=-27.045 EndY=53.1952 EndZ=0
    g26: LineSegment StartX=-29.4198 StartY=51.2026 StartZ=0 EndX=-27.134 EndY=48.4785 EndZ=0
    g27: LineSegment StartX=-7.1631 StartY=27.0895 StartZ=0 EndX=-6.02023 EndY=25.7275 EndZ=0
    g28: LineSegment StartX=-30.9105 StartY=7.1631 StartZ=0 EndX=-29.7676 EndY=5.80108 EndZ=0
    g29: LineSegment StartX=-51.9798 StartY=32.2725 StartZ=0 EndX=-50.8369 EndY=30.9105 EndZ=0
    g30: LineSegment StartX=-28.2324 StartY=52.1989 StartZ=0 EndX=-27.0895 EndY=50.8369 EndZ=0
    g31: LineSegment StartX=-8.30598 StartY=28.4515 StartZ=0 EndX=-8.13598 EndY=26.2732 EndZ=0
    g32: LineSegment StartX=-8.13598 StartY=26.2732 StartZ=0 EndX=-6.02023 EndY=25.7275 EndZ=0
  constraints (80):
    c: Coincident(g0,g1)
    c: Coincident(g1,g2)
    c: Coincident(g2,g3)
    c: Coincident(g3,g0)
    c: Symmetric(g1,g0,g4)
    c: Perpendicular(g3,g0)
    c: Perpendicular(g3,g2)
    c: Perpendicular(g2,g1)
    c: Equal(g3,g2)
    c: Distance(g1) = 31
    c: Tangent(g5,g7) = -1.5708
    c: Tangent(g7,g6) = -1.5708
    c: Tangent(g6,g8) = -1.5708
    c: Tangent(g8,g5) = -1.5708
    c: Equal(g5,g6)
    c: Parallel(g8,g1)
    c: Distance(g5,g5) = 22.1
    c: Coincident(g9,g5)
    c: Coincident(g9,g4)
    c: Coincident(g10,g4)
    c: Coincident(g10,g6)
    c: Parallel(g10,g9)
    c: Equal(g9,g10)
    c: Tangent(g11,g13) = -1.5708
    c: Tangent(g13,g12) = -1.5708
    c: Tangent(g12,g14) = -1.5708
    c: Tangent(g14,g11) = -1.5708
    c: Equal(g11,g12)
    c: PointOnObject(g11,g3)
    c: Tangent(g15,g17) = -1.5708
    c: Tangent(g17,g16) = -1.5708
    c: Tangent(g16,g18) = -1.5708
    c: Tangent(g18,g15) = -1.5708
    c: Equal(g15,g16)
    c: PointOnObject(g15,g1)
    c: Tangent(g19,g21) = -1.5708
    c: Tangent(g21,g20) = -1.5708
    c: Tangent(g20,g22) = -1.5708
    c: Tangent(g22,g19) = -1.5708
    c: Equal(g19,g20)
    c: PointOnObject(g19,g3)
    c: Tangent(g23,g25) = -1.5708
    c: Tangent(g25,g24) = -1.5708
    c: Tangent(g24,g26) = -1.5708
    c: Tangent(g26,g23) = -1.5708
    c: Equal(g23,g24)
    c: PointOnObject(g23,g1)
    c: Parallel(g18,g25)
    c: Coincident(g27,g0)
    c: Coincident(g27,g16)
    c: Parallel(g27,g1)
    c: Equal(g25,g18)
    c: Equal(g18,g22)
    c: Equal(g22,g13)
    c: Coincident(g28,g0)
    c: Coincident(g28,g12)
    c: Parallel(g3,g28)
    c: Diameter(g12) = 3.1
    c: Equal(g20,g12)
    c: Equal(g12,g16)
    c: Equal(g16,g24)
    c: Coincident(g29,g20)
    c: Coincident(g29,g2)
    c: Coincident(g30,g24)
    c: Coincident(g30,g1)
    c: Equal(g30,g29)
    c: Equal(g29,g27)
    c: Equal(g27,g28)
    c: Parallel(g29,g3)
    c: Distance(g5,g6) = 3.556
    c: Distance(g23,g24) = 3.556
    c: Coincident(g31,g15)
    c: PointOnObject(g31,g0)
    c: Coincident(g32,g31)
    c: Coincident(g32,g16)
    c: Equal(g31,g32)
    c: Distance(g31,g0) = 1.27
    c: DistanceY(g-1,g4) = 29
    c: DistanceX(g4,g-1) = 29
    c: Angle(g-1,g3) = 2.26893
FEATURE [Sketcher::SketchObject] Sketch025
  FullyConstrained = true
  MapMode = 5
  Support = -> [XY_Plane]
  expr: Constraints[0] = 25mm
  sketch-geometry (10):
    g0: Circle CenterX=0 CenterY=0 CenterZ=0 NormalX=0 NormalY=0 NormalZ=1 AngleXU=0 Radius=12.5
    g1: Circle CenterX=0 CenterY=10.16 CenterZ=0 NormalX=0 NormalY=0 NormalZ=1 AngleXU=0 Radius=1.5
    g2: Circle CenterX=8.79882 CenterY=5.08 CenterZ=0 NormalX=0 NormalY=0 NormalZ=1 AngleXU=0 Radius=1.5
    g3: Circle CenterX=8.79882 CenterY=-5.08 CenterZ=0 NormalX=0 NormalY=0 NormalZ=1 AngleXU=0 Radius=1.5
    g4: Circle CenterX=0 CenterY=-10.16 CenterZ=0 NormalX=0 NormalY=0 NormalZ=1 AngleXU=0 Radius=1.5
    g5: Circle CenterX=-8.79882 CenterY=-5.08 CenterZ=0 NormalX=0 NormalY=0 NormalZ=1 AngleXU=0 Radius=1.5
    g6: Circle CenterX=-8.79882 CenterY=5.08 CenterZ=0 NormalX=0 NormalY=0 NormalZ=1 AngleXU=0 Radius=1.5
    g7: LineSegment StartX=-8.79882 StartY=-5.08 StartZ=0 EndX=8.79882 EndY=5.08 EndZ=0
    g8: LineSegment StartX=8.79882 StartY=-5.08 StartZ=0 EndX=-8.79882 EndY=5.08 EndZ=0
    g9: LineSegment StartX=0 StartY=10.16 StartZ=0 EndX=0 EndY=-10.16 EndZ=0
  constraints (23):
    c: Diameter(g0) = 25
    c: Coincident(g0,g-1)
    c: PointOnObject(g1,g-2)
    c: Equal(g1,g6)
    c: Equal(g6,g2)
    c: Equal(g2,g3)
    c: Equal(g3,g4)
    c: Equal(g4,g5)
    c: Diameter(g1) = 3
    c: Coincident(g7,g5)
    c: Coincident(g7,g2)
    c: Coincident(g8,g3)
    c: Coincident(g8,g6)
    c: Symmetric(g3,g6,g0)
    c: Symmetric(g5,g2,g0)
    c: Angle(g7,g-1) = 2.61799
    c: Angle(g8,g-1) = 0.523599
    c: Coincident(g9,g1)
    c: Coincident(g9,g4)
    c: Equal(g8,g7)
    c: Equal(g7,g9)
    c: Symmetric(g1,g4,g0)
    c: DistanceY(g1) = 10.16
FEATURE [Sketcher::SketchObject] Sketch026
  FullyConstrained = false
  MapMode = 5
  Support = -> [XY_Plane011]
  expr: Constraints[13] = Spreadsheet.PivotFrameRadius
  sketch-geometry (7):
    g0: ArcOfCircle CenterX=0 CenterY=0 CenterZ=0 NormalX=0 NormalY=0 NormalZ=1 AngleXU=0 Radius=34.9226 StartAngle=4.71239 EndAngle=6.34897
    g1: ArcOfCircle CenterX=0 CenterY=0 CenterZ=0 NormalX=0 NormalY=0 NormalZ=1 AngleXU=0 Radius=41.91 StartAngle=4.71239 EndAngle=6.33799
    g2: LineSegment StartX=34.8471 StartY=2.29554 StartZ=0 EndX=41.8471 EndY=2.29554 EndZ=0
    g3: LineSegment StartX=-6.4e-15 StartY=-34.9226 StartZ=0 EndX=-6.4e-15 EndY=-41.91 EndZ=0
    g4: LineSegment StartX=-23.8891 StartY=-30.1063 StartZ=0 EndX=-24.9829 EndY=-25.0613 EndZ=0
    g5: LineSegment StartX=-24.9829 StartY=-25.0613 StartZ=0 EndX=-7.1e-15 EndY=-34.9226 EndZ=0
    g6: LineSegment StartX=-23.8891 StartY=-30.1063 StartZ=0 EndX=-7.1e-15 EndY=-41.91 EndZ=0
  constraints (15):
    c: Coincident(g0,g-1)
    c: PointOnObject(g0,g-2)
    c: Coincident(g1,g0)
    c: Vertical(g1,g0)
    c: Horizontal(g1,g0)
    c: Coincident(g2,g0)
    c: Coincident(g2,g1)
    c: Coincident(g3,g0)
    c: Coincident(g3,g1)
    c: Coincident(g4,g5)
    c: Coincident(g5,g0)
    c: Coincident(g4,g6)
    c: Coincident(g6,g1)
    c: Diameter(g1) = 83.82
    c: DistanceX(g2,g2) = 7
FEATURE [PartDesign::Pad] Pad009
  BaseFeature = -> Pad007
  Direction = (0,0,1)
  Length = 29.21
  Length2 = 9.906
  Profile = -> Sketch026
  ReferenceAxis = -> Sketch026 [N_Axis]
  Type = 0
FEATURE [Sketcher::SketchObject] Sketch027
  AttachmentOffset = pos=(0,0,29.21) rot=(0,0,1;0rad)
  FullyConstrained = false
  MapMode = 5
  Placement = pos=(0,0,29.21) rot=(0,0,1;0rad)
  Support = -> [XY_Plane011]
  expr: Constraints[7] = Spreadsheet.PivotFrameRadius
  sketch-geometry (15):
    g0: Circle CenterX=0 CenterY=0 CenterZ=0 NormalX=0 NormalY=0 NormalZ=1 AngleXU=0 Radius=15.9
    g1: ArcOfCircle CenterX=0 CenterY=0 CenterZ=0 NormalX=0 NormalY=0 NormalZ=1 AngleXU=0 Radius=41.91 StartAngle=4.71239 EndAngle=6.46427
    g2: LineSegment StartX=41.2247 StartY=7.54787 StartZ=0 EndX=40.5483 EndY=11.2423 EndZ=0
    g3: LineSegment StartX=-4.4308 StartY=21.4434 StartZ=0 EndX=-17.2122 EndY=15.3247 EndZ=0
    g4: LineSegment StartX=40.5483 StartY=11.2423 StartZ=0 EndX=-4.4308 EndY=21.4434 EndZ=0
    g5: LineSegment StartX=-17.2122 StartY=15.3247 StartZ=0 EndX=-22.6585 EndY=-20.3025 EndZ=0
    g6: LineSegment StartX=-22.6585 StartY=-20.3025 StartZ=0 EndX=0 EndY=-41.91 EndZ=0
    g7: Circle CenterX=38.4941 CenterY=-0.671918 CenterZ=0 NormalX=0 NormalY=0 NormalZ=1 AngleXU=0 Radius=2.3
    g8: Circle CenterX=33.0009 CenterY=-19.829 CenterZ=0 NormalX=0 NormalY=0 NormalZ=1 AngleXU=0 Radius=2.3
    g9: Circle CenterX=-0.671918 CenterY=-38.4941 CenterZ=0 NormalX=0 NormalY=0 NormalZ=1 AngleXU=0 Radius=2.3
    g10: Circle CenterX=18.6652 CenterY=-33.6729 CenterZ=0 NormalX=0 NormalY=0 NormalZ=1 AngleXU=0 Radius=2.3
    g11: LineSegment StartX=0 StartY=0 StartZ=0 EndX=38.4941 EndY=-0.671918 EndZ=0
    g12: LineSegment StartX=0 StartY=0 StartZ=0 EndX=33.0009 EndY=-19.829 EndZ=0
    g13: LineSegment StartX=0 StartY=0 StartZ=0 EndX=18.6652 EndY=-33.6729 EndZ=0
    g14: LineSegment StartX=0 StartY=0 StartZ=0 EndX=-0.671918 EndY=-38.4941 EndZ=0
  constraints (31):
    c: Coincident(g0,g-1)
    c: Diameter(g0) = 31.8
    c: Tangent(g1,g2) = -1.5708
    c: Coincident(g1,g0)
    c: Coincident(g4,g2)
    c: Coincident(g4,g3)
    c: Coincident(g5,g3)
    c: Diameter(g1) = 83.82
    c: PointOnObject(g1,g-2)
    c: Coincident(g5,g6)
    c: Coincident(g6,g1)
    c: Coincident(g11,g0)
    c: Coincident(g11,g7)
    c: Coincident(g12,g0)
    c: Coincident(g12,g8)
    c: Coincident(g13,g0)
    c: Coincident(g13,g10)
    c: Coincident(g14,g0)
    c: Coincident(g14,g9)
    c: Equal(g14,g13)
    c: Equal(g13,g12)
    c: Equal(g12,g11)
    c: Equal(g10,g7)
    c: Equal(g7,g8)
    c: Equal(g8,g9)
    c: Diameter(g7) = 4.6
    c: Distance(g11) = 38.5
    c: Angle(g12,g11) = 0.523599
    c: Angle(g13,g12) = 0.523599
    c: Angle(g14,g13) = 0.523599
    c: Angle(g11,g-1) = 0.0174533
FEATURE [Sketcher::SketchObject] Sketch028
  AttachmentOffset = pos=(0,0,17) rot=(0,0,1;0rad)
  FullyConstrained = false
  MapMode = 5
  Placement = pos=(0,0,17) rot=(0,0,1;0rad)
  Support = -> [XY_Plane002]
  sketch-geometry (8):
    g0: ArcOfCircle CenterX=-21.5074 CenterY=0 CenterZ=0 NormalX=0 NormalY=0 NormalZ=1 AngleXU=0 Radius=4 StartAngle=4.35012 EndAngle=8.11146
    g1: LineSegment StartX=-22.925 StartY=-3.74038 StartZ=0 EndX=-28.0552 EndY=-7.62 EndZ=0
    g2: LineSegment StartX=-22.526 StartY=3.86814 StartZ=0 EndX=-34.2403 EndY=0.783535 EndZ=0
    g3: LineSegment StartX=-28.0552 StartY=-7.62 StartZ=0 EndX=-39.3482 EndY=-7.62 EndZ=0
    g4: LineSegment StartX=-39.3482 StartY=-7.62 StartZ=0 EndX=-39.1891 EndY=-5.07912 EndZ=0
    g5: LineSegment StartX=-39.1891 StartY=-5.07912 StartZ=0 EndX=-34.2403 EndY=0.783535 EndZ=0
    g6: Circle CenterX=-21.5074 CenterY=0 CenterZ=0 NormalX=0 NormalY=0 NormalZ=1 AngleXU=0 Radius=1.55837
    g7: Circle CenterX=-21.5074 CenterY=0 CenterZ=0 NormalX=0 NormalY=0 NormalZ=1 AngleXU=0 Radius=5
  constraints (13):
    c: PointOnObject(g0,g-1)
    c: Coincident(g1,g0)
    c: Coincident(g3,g1)
    c: DistanceY(g3,g-1) = 7.62
    c: Horizontal(g3)
    c: Coincident(g4,g3)
    c: Coincident(g5,g4)
    c: Coincident(g5,g2)
    c: Coincident(g6,g0)
    c: Coincident(g7,g0)
    c: Diameter(g7) = 10
    c: Tangent(g2,g0) = -1.5708
    c: Diameter(g0) = 8
FEATURE [PartDesign::Pad] Pad011
  BaseFeature = -> Pad001
  Direction = (0,0,1)
  Length = 3.81
  Length2 = 9.906
  Placement = pos=(0,0,0) rot=(1,0,0;1.5708rad)
  Profile = -> Sketch028
  ReferenceAxis = -> Sketch028 [N_Axis]
  Type = 0
FEATURE [Sketcher::SketchObject] Sketch029
  AttachmentOffset = pos=(0,0,25.4) rot=(0,0,1;0rad)
  FullyConstrained = true
  MapMode = 5
  Placement = pos=(0,-25.4,-5.6e-15) rot=(1,0,0;1.5708rad)
  Support = -> [XZ_Plane002]
  sketch-geometry (10):
    g0: LineSegment StartX=-4.75 StartY=40.75 StartZ=0 EndX=-30.75 EndY=40.75 EndZ=0
    g1: LineSegment StartX=-30.75 StartY=40.75 StartZ=0 EndX=-30.75 EndY=14.75 EndZ=0
    g2: LineSegment StartX=-30.75 StartY=14.75 StartZ=0 EndX=-4.75 EndY=14.75 EndZ=0
    g3: LineSegment StartX=-4.75 StartY=14.75 StartZ=0 EndX=-4.75 EndY=40.75 EndZ=0
    g4: Circle CenterX=-30.75 CenterY=40.75 CenterZ=0 NormalX=0 NormalY=0 NormalZ=1 AngleXU=0 Radius=1.5
    g5: Circle CenterX=-4.75 CenterY=40.75 CenterZ=0 NormalX=0 NormalY=0 NormalZ=1 AngleXU=0 Radius=1.5
    g6: Circle CenterX=-4.75 CenterY=14.75 CenterZ=0 NormalX=0 NormalY=0 NormalZ=1 AngleXU=0 Radius=1.5
    g7: Circle CenterX=-30.75 CenterY=14.75 CenterZ=0 NormalX=0 NormalY=0 NormalZ=1 AngleXU=0 Radius=1.5
    g8: GeomPoint X=-17.75 Y=27.75 Z=0
    g9: Circle CenterX=-17.75 CenterY=27.75 CenterZ=0 NormalX=0 NormalY=0 NormalZ=1 AngleXU=0 Radius=11.5
  constraints (23):
    c: Coincident(g0,g1)
    c: Coincident(g1,g2)
    c: Coincident(g2,g3)
    c: Coincident(g3,g0)
    c: Equal(g0,g1)
    c: Equal(g0,g2)
    c: Equal(g0,g3)
    c: Perpendicular(g0,g1)
    c: Coincident(g4,g0)
    c: Coincident(g5,g0)
    c: Coincident(g6,g2)
    c: Coincident(g7,g1)
    c: Equal(g7,g4)
    c: Equal(g4,g5)
    c: Equal(g5,g6)
    c: Diameter(g6) = 3
    c: Symmetric(g4,g6,g8)
    c: Distance(g3) = 26
    c: Vertical(g3)
    c: Coincident(g9,g8)
    c: Diameter(g9) = 23
    c: DistanceX(g9) = -17.75
    c: DistanceY(g9) = 27.75
FEATURE [Part::Feature] Part__Feature056  label="FeedMotor"
  Placement = pos=(-17.6022,-25.4,27.813) rot=(-1,0,0;1.5708rad)
  shape: bbox 35 x 37.5 x 39.5 mm, 178 faces (baked)
FEATURE [Part::Feature] Part__Feature057  label="RotateMotor-14"
  Placement = pos=(-24.0959,23.8442,-15.748) rot=(0,0,1;3.83972rad)
  shape: bbox 46.74 x 46.74 x 37.5 mm, 178 faces (baked)
FEATURE [Sketcher::SketchObject] Sketch030
  FullyConstrained = false
  MapMode = 5
  Support = -> [XY_Plane011]
  expr: Constraints[16] = 22.1mm
  expr: Constraints[85] = 43mm
  sketch-geometry (38):
    g0: LineSegment StartX=-30.6023 StartY=10.6852 StartZ=0 EndX=-10.6852 EndY=27.3977 EndZ=0
    g1: LineSegment StartX=-10.6852 StartY=27.3977 StartZ=0 EndX=-27.3977 EndY=47.3148 EndZ=0
    g2: LineSegment StartX=-27.3977 StartY=47.3148 StartZ=0 EndX=-47.3148 EndY=30.6023 EndZ=0
    g3: LineSegment StartX=-47.3148 StartY=30.6023 StartZ=0 EndX=-30.6023 EndY=10.6852 EndZ=0
    g4: GeomPoint X=-29 Y=29 Z=0
    g5: ArcOfCircle CenterX=-30.1429 CenterY=30.362 CenterZ=0 NormalX=0 NormalY=0 NormalZ=1 AngleXU=0 Radius=11.05 StartAngle=0.698132 EndAngle=3.83972
    g6: ArcOfCircle CenterX=-27.8571 CenterY=27.638 CenterZ=0 NormalX=0 NormalY=0 NormalZ=1 AngleXU=0 Radius=11.05 StartAngle=3.83972 EndAngle=6.98132
    g7: LineSegment StartX=-38.6077 StartY=23.2592 StartZ=0 EndX=-36.3219 EndY=20.5352 EndZ=0
    g8: LineSegment StartX=-19.3923 StartY=34.7408 StartZ=0 EndX=-21.6781 EndY=37.4648 EndZ=0
    g9: LineSegment StartX=-30.1429 StartY=30.362 StartZ=0 EndX=-29 EndY=29 EndZ=0
    g10: LineSegment StartX=-29 StartY=29 StartZ=0 EndX=-27.8571 EndY=27.638 EndZ=0
    g11: ArcOfCircle CenterX=-31.7452 CenterY=12.0472 CenterZ=0 NormalX=0 NormalY=0 NormalZ=1 AngleXU=0 Radius=1.55 StartAngle=0.698132 EndAngle=3.83972
    g12: ArcOfCircle CenterX=-29.4595 CenterY=9.32316 CenterZ=0 NormalX=0 NormalY=0 NormalZ=1 AngleXU=0 Radius=1.55 StartAngle=3.83972 EndAngle=6.98132
    g13: LineSegment StartX=-32.9326 StartY=11.0509 StartZ=0 EndX=-30.6468 EndY=8.32684 EndZ=0
    g14: LineSegment StartX=-28.2721 StartY=10.3195 StartZ=0 EndX=-30.5578 EndY=13.0435 EndZ=0
    g15: ArcOfCircle CenterX=-11.8281 CenterY=28.7597 CenterZ=0 NormalX=0 NormalY=0 NormalZ=1 AngleXU=0 Radius=1.55 StartAngle=0.698132 EndAngle=3.83972
    g16: ArcOfCircle CenterX=-9.54231 CenterY=26.0356 CenterZ=0 NormalX=0 NormalY=0 NormalZ=1 AngleXU=0 Radius=1.55 StartAngle=3.83972 EndAngle=6.98132
    g17: LineSegment StartX=-13.0154 StartY=27.7634 StartZ=0 EndX=-10.7297 EndY=25.0393 EndZ=0
    g18: LineSegment StartX=-8.35494 StartY=27.032 StartZ=0 EndX=-10.6407 EndY=29.756 EndZ=0
    g19: ArcOfCircle CenterX=-46.1719 CenterY=29.2403 CenterZ=0 NormalX=0 NormalY=0 NormalZ=1 AngleXU=0 Radius=1.55 StartAngle=3.83972 EndAngle=6.98132
    g20: ArcOfCircle CenterX=-48.4577 CenterY=31.9644 CenterZ=0 NormalX=0 NormalY=0 NormalZ=1 AngleXU=0 Radius=1.55 StartAngle=0.698132 EndAngle=3.83972
    g21: LineSegment StartX=-44.9846 StartY=30.2366 StartZ=0 EndX=-47.2703 EndY=32.9607 EndZ=0
    g22: LineSegment StartX=-49.6451 StartY=30.968 StartZ=0 EndX=-47.3593 EndY=28.244 EndZ=0
    g23: ArcOfCircle CenterX=-26.2548 CenterY=45.9528 CenterZ=0 NormalX=0 NormalY=0 NormalZ=1 AngleXU=0 Radius=1.55 StartAngle=3.83972 EndAngle=6.98132
    g24: ArcOfCircle CenterX=-28.5405 CenterY=48.6768 CenterZ=0 NormalX=0 NormalY=0 NormalZ=1 AngleXU=0 Radius=1.55 StartAngle=0.698132 EndAngle=3.83972
    g25: LineSegment StartX=-25.0674 StartY=46.9491 StartZ=0 EndX=-27.3532 EndY=49.6732 EndZ=0
    g26: LineSegment StartX=-29.7279 StartY=47.6805 StartZ=0 EndX=-27.4422 EndY=44.9565 EndZ=0
    g27: LineSegment StartX=-10.6852 StartY=27.3977 StartZ=0 EndX=-9.54231 EndY=26.0356 EndZ=0
    g28: LineSegment StartX=-30.6023 StartY=10.6852 StartZ=0 EndX=-29.4595 EndY=9.32316 EndZ=0
    g29: LineSegment StartX=-48.4577 StartY=31.9644 StartZ=0 EndX=-47.3148 EndY=30.6023 EndZ=0
    g30: LineSegment StartX=-28.5405 StartY=48.6768 StartZ=0 EndX=-27.3977 EndY=47.3148 EndZ=0
    g31: LineSegment StartX=-11.8281 StartY=28.7597 StartZ=0 EndX=-11.6581 EndY=26.5813 EndZ=0
    g32: LineSegment StartX=-11.6581 StartY=26.5813 StartZ=0 EndX=-9.54231 EndY=26.0356 EndZ=0
    g33: LineSegment StartX=-28.356 StartY=61.6805 StartZ=0 EndX=-61.2959 EndY=34.0407 EndZ=0
    g34: LineSegment StartX=-61.2959 StartY=34.0407 StartZ=0 EndX=-29.644 EndY=-3.68055 EndZ=0
    g35: LineSegment StartX=-29.644 StartY=-3.68055 StartZ=0 EndX=3.29589 EndY=23.9593 EndZ=0
    g36: LineSegment StartX=3.29589 StartY=23.9593 StartZ=0 EndX=-28.356 EndY=61.6805 EndZ=0
    g37: GeomPoint X=-29 Y=29 Z=0
  constraints (91):
    c: Coincident(g0,g1)
    c: Coincident(g1,g2)
    c: Coincident(g2,g3)
    c: Coincident(g3,g0)
    c: Symmetric(g1,g0,g4)
    c: Perpendicular(g3,g0)
    c: Perpendicular(g3,g2)
    c: Perpendicular(g2,g1)
    c: Equal(g3,g2)
    c: Distance(g1) = 26
    c: Tangent(g5,g7) = -1.5708
    c: Tangent(g7,g6) = -1.5708
    c: Tangent(g6,g8) = -1.5708
    c: Tangent(g8,g5) = -1.5708
    c: Equal(g5,g6)
    c: Parallel(g8,g1)
    c: Distance(g5,g5) = 22.1
    c: Coincident(g9,g5)
    c: Coincident(g9,g4)
    c: Coincident(g10,g4)
    c: Coincident(g10,g6)
    c: Parallel(g10,g9)
    c: Equal(g9,g10)
    c: Tangent(g11,g13) = -1.5708
    c: Tangent(g13,g12) = -1.5708
    c: Tangent(g12,g14) = -1.5708
    c: Tangent(g14,g11) = -1.5708
    c: Equal(g11,g12)
    c: PointOnObject(g11,g3)
    c: Tangent(g15,g17) = -1.5708
    c: Tangent(g17,g16) = -1.5708
    c: Tangent(g16,g18) = -1.5708
    c: Tangent(g18,g15) = -1.5708
    c: Equal(g15,g16)
    c: PointOnObject(g15,g1)
    c: Tangent(g19,g21) = -1.5708
    c: Tangent(g21,g20) = -1.5708
    c: Tangent(g20,g22) = -1.5708
    c: Tangent(g22,g19) = -1.5708
    c: Equal(g19,g20)
    c: PointOnObject(g19,g3)
    c: Tangent(g23,g25) = -1.5708
    c: Tangent(g25,g24) = -1.5708
    c: Tangent(g24,g26) = -1.5708
    c: Tangent(g26,g23) = -1.5708
    c: Equal(g23,g24)
    c: PointOnObject(g23,g1)
    c: Parallel(g18,g25)
    c: Coincident(g27,g0)
    c: Coincident(g27,g16)
    c: Parallel(g27,g1)
    c: Equal(g25,g18)
    c: Equal(g18,g22)
    c: Equal(g22,g13)
    c: Coincident(g28,g0)
    c: Coincident(g28,g12)
    c: Parallel(g3,g28)
    c: Diameter(g12) = 3.1
    c: Equal(g20,g12)
    c: Equal(g12,g16)
    c: Equal(g16,g24)
    c: Coincident(g29,g20)
    c: Coincident(g29,g2)
    c: Coincident(g30,g24)
    c: Coincident(g30,g1)
    c: Equal(g30,g29)
    c: Equal(g29,g27)
    c: Equal(g27,g28)
    c: Parallel(g29,g3)
    c: Distance(g5,g6) = 3.556
    c: Distance(g23,g24) = 3.556
    c: Coincident(g31,g15)
    c: PointOnObject(g31,g0)
    c: Coincident(g32,g31)
    c: Coincident(g32,g16)
    c: Equal(g31,g32)
    c: Distance(g31,g0) = 1.27
    c: Angle(g-1,g3) = 2.26893
    c: DistanceY(g-1,g4) = 29
    c: DistanceX(g4,g-1) = 29
    c: Coincident(g33,g34)
    c: Coincident(g34,g35)
    c: Coincident(g35,g36)
    c: Coincident(g36,g33)
    c: Parallel(g1,g36)
    c: Distance(g33) = 43
    c: Perpendicular(g34,g35)
    c: Perpendicular(g33,g34)
    c: Perpendicular(g36,g33)
    c: Symmetric(g33,g35,g37)
    c: Coincident(g37,g4)
FEATURE [Sketcher::SketchObject] Sketch031
  AttachmentOffset = pos=(0,0,14) rot=(0,0,1;0rad)
  FullyConstrained = false
  MapMode = 5
  Placement = pos=(0,-14,-3.1e-15) rot=(1,0,0;1.5708rad)
  Support = -> [XZ_Plane016]
  sketch-geometry (1):
    g0: LineSegment StartX=-40.9166 StartY=28.5719 StartZ=0 EndX=-17.4675 EndY=32.6815 EndZ=0
FEATURE [PartDesign::Body] Body007  label="FeedMount"
  Group = -> [Sketch031]
  Origin = -> Origin016
FEATURE [Sketcher::SketchObject] Sketch032  label="YSlicer"
  AttachmentOffset = pos=(0,0,50) rot=(0,0,1;0rad)
  FullyConstrained = false
  MapMode = 5
  Placement = pos=(-50,1.11e-14,-1.11e-14) rot=(-0.57735,0.57735,0.57735;4.18879rad)
  Support = -> [YZ_Plane002]
  sketch-geometry (6):
    g0: LineSegment StartX=15.0915 StartY=7.36291 StartZ=0 EndX=25.8864 EndY=11.1747 EndZ=0
    g1: LineSegment StartX=25.8864 StartY=11.1747 StartZ=0 EndX=25.8864 EndY=33.1188 EndZ=0
    g2: LineSegment StartX=15.0915 StartY=7.36291 StartZ=0 EndX=15.0915 EndY=-12.4787 EndZ=0
    g3: LineSegment StartX=15.0915 StartY=-12.4787 StartZ=0 EndX=34.9085 EndY=-12.4787 EndZ=0
    g4: LineSegment StartX=34.9085 StartY=-12.4787 StartZ=0 EndX=34.9085 EndY=33.1188 EndZ=0
    g5: LineSegment StartX=34.9085 StartY=33.1188 StartZ=0 EndX=25.8864 EndY=33.1188 EndZ=0
  constraints (11):
    c: Coincident(g1,g0)
    c: Vertical(g1)
    c: Coincident(g2,g0)
    c: Vertical(g2)
    c: Coincident(g3,g2)
    c: Horizontal(g3)
    c: Coincident(g4,g3)
    c: Vertical(g4)
    c: Coincident(g5,g4)
    c: Coincident(g5,g1)
    c: Horizontal(g5)
FEATURE [PartDesign::Pocket] Pocket007
  BaseFeature = -> Pad011
  Direction = (1,-2e-16,3e-16)
  Length = 5
  Length2 = 5
  Placement = pos=(0,0,0) rot=(1,0,0;1.5708rad)
  Profile = -> Sketch032
  ReferenceAxis = -> Sketch032 [N_Axis]
  Type = 1
FEATURE [Sketcher::SketchObject] Sketch033  label="ZSlicer"
  AttachmentOffset = pos=(0,0,35) rot=(0,0,1;0rad)
  FullyConstrained = false
  MapMode = 5
  Placement = pos=(0,0,35) rot=(0,0,1;0rad)
  Support = -> [XY_Plane002]
  sketch-geometry (4):
    g0: LineSegment StartX=-43.8848 StartY=-23.4718 StartZ=0 EndX=-43.8848 EndY=-6.06898 EndZ=0
    g1: LineSegment StartX=-43.8848 StartY=-6.06898 StartZ=0 EndX=-25.5222 EndY=-6.06898 EndZ=0
    g2: LineSegment StartX=-25.5222 StartY=-6.06898 StartZ=0 EndX=-25.5222 EndY=-9.61029 EndZ=0
    g3: LineSegment StartX=-43.8848 StartY=-23.4718 StartZ=0 EndX=-25.5222 EndY=-9.61029 EndZ=0
  constraints (7):
    c: Coincident(g0,g1)
    c: Coincident(g1,g2)
    c: Horizontal(g1)
    c: Vertical(g0)
    c: Vertical(g2)
    c: Coincident(g3,g0)
    c: Coincident(g3,g2)
FEATURE [PartDesign::Pocket] Pocket008
  BaseFeature = -> Pocket007
  Direction = (0,0,-1)
  Length = 12.6
  Length2 = 5
  Placement = pos=(0,0,0) rot=(1,0,0;1.5708rad)
  Profile = -> Sketch033
  ReferenceAxis = -> Sketch033 [N_Axis]
  Type = 0
FEATURE [Sketcher::SketchObject] Sketch034
  AttachmentOffset = pos=(0,0,-25) rot=(0,0,1;0rad)
  FullyConstrained = false
  MapMode = 5
  Placement = pos=(0,-25,-5.6e-15) rot=(0,0.707107,0.707107;3.14159rad)
  Support = -> [XZ_Plane002]
  sketch-geometry (19):
    g0: LineSegment StartX=30.75 StartY=40.75 StartZ=0 EndX=4.75 EndY=40.75 EndZ=0
    g1: LineSegment StartX=4.75 StartY=40.75 StartZ=0 EndX=4.75 EndY=14.75 EndZ=0
    g2: LineSegment StartX=4.75 StartY=14.75 StartZ=0 EndX=30.75 EndY=14.75 EndZ=0
    g3: LineSegment StartX=30.75 StartY=14.75 StartZ=0 EndX=30.75 EndY=40.75 EndZ=0
    g4: Circle CenterX=4.75 CenterY=40.75 CenterZ=0 NormalX=0 NormalY=0 NormalZ=1 AngleXU=0 Radius=1.5
    g5: Circle CenterX=30.75 CenterY=40.75 CenterZ=0 NormalX=0 NormalY=0 NormalZ=1 AngleXU=0 Radius=1.5
    g6: Circle CenterX=30.75 CenterY=14.75 CenterZ=0 NormalX=0 NormalY=0 NormalZ=1 AngleXU=0 Radius=1.5
    g7: Circle CenterX=4.75 CenterY=14.75 CenterZ=0 NormalX=0 NormalY=0 NormalZ=1 AngleXU=0 Radius=1.5
    g8: GeomPoint X=17.75 Y=27.75 Z=0
    g9: ArcOfCircle CenterX=4.75 CenterY=40.75 CenterZ=0 NormalX=0 NormalY=0 NormalZ=1 AngleXU=0 Radius=3.26481 StartAngle=1.61434 EndAngle=4.71239
    g10: ArcOfCircle CenterX=4.75 CenterY=14.75 CenterZ=0 NormalX=0 NormalY=0 NormalZ=1 AngleXU=0 Radius=3.26481 StartAngle=1.5708 EndAngle=4.71239
    g11: LineSegment StartX=4.75 StartY=11.4852 StartZ=0 EndX=33.7613 EndY=11.4852 EndZ=0
    g12: LineSegment StartX=4.60787 StartY=44.0117 StartZ=0 EndX=33.8629 EndY=44.0117 EndZ=0
    g13: LineSegment StartX=33.8629 StartY=44.0117 StartZ=0 EndX=40.9653 EndY=36.7606 EndZ=0
    g14: ArcOfCircle CenterX=17.75 CenterY=27.75 CenterZ=0 NormalX=0 NormalY=0 NormalZ=1 AngleXU=0 Radius=12.5 StartAngle=4.03437 EndAngle=8.532
    g15: LineSegment StartX=4.75 StartY=18.0148 StartZ=0 EndX=9.90933 EndY=18.0148 EndZ=0
    g16: LineSegment StartX=4.75 StartY=37.4852 StartZ=0 EndX=9.90933 EndY=37.4852 EndZ=0
    g17: LineSegment StartX=40.9653 StartY=36.7606 StartZ=0 EndX=40.9653 EndY=19.1299 EndZ=0
    g18: LineSegment StartX=40.9653 StartY=19.1299 StartZ=0 EndX=33.7613 EndY=11.4852 EndZ=0
  constraints (44):
    c: Coincident(g0,g1)
    c: Coincident(g1,g2)
    c: Coincident(g2,g3)
    c: Coincident(g3,g0)
    c: Equal(g0,g1)
    c: Equal(g0,g2)
    c: Equal(g0,g3)
    c: Perpendicular(g0,g1)
    c: Coincident(g4,g0)
    c: Coincident(g5,g0)
    c: Coincident(g6,g2)
    c: Coincident(g7,g1)
    c: Equal(g7,g4)
    c: Equal(g4,g5)
    c: Equal(g5,g6)
    c: Diameter(g6) = 3
    c: Symmetric(g4,g6,g8)
    c: Distance(g3) = 26
    c: Vertical(g3)
    c: DistanceX(g8) = 17.75
    c: DistanceY(g8) = 27.75
    c: Coincident(g9,g4)
    c: PointOnObject(g9,g1)
    c: Coincident(g10,g7)
    c: PointOnObject(g10,g1)
    c: Vertical(g10,g7)
    c: Equal(g9,g10)
    c: Coincident(g11,g10)
    c: Horizontal(g11)
    c: Coincident(g12,g9)
    c: Horizontal(g12)
    c: Coincident(g13,g12)
    c: Coincident(g14,g8)
    c: Diameter(g14) = 25
    c: Coincident(g15,g10)
    c: Coincident(g16,g9)
    c: Horizontal(g16)
    c: Horizontal(g15)
    c: Coincident(g14,g16)
    c: Coincident(g14,g15)
    c: Coincident(g17,g13)
    c: Coincident(g18,g17)
    c: Coincident(g18,g11)
    c: Vertical(g17)
FEATURE [PartDesign::Pad] Pad012
  BaseFeature = -> Pocket008
  Direction = (0,1,2e-16)
  Length = 3
  Length2 = 10
  Placement = pos=(0,0,0) rot=(1,0,0;1.5708rad)
  Profile = -> Sketch034
  ReferenceAxis = -> Sketch034 [N_Axis]
  Type = 0
FEATURE [PartDesign::Pocket] Pocket009
  BaseFeature = -> Pad012
  Direction = (0,1,2e-16)
  Length = 5
  Length2 = 5
  Placement = pos=(0,0,0) rot=(1,0,0;1.5708rad)
  Profile = -> Sketch029
  ReferenceAxis = -> Sketch029 [N_Axis]
  Type = 1
FEATURE [Sketcher::SketchObject] Sketch035
  AttachmentOffset = pos=(0,0,25.4) rot=(0,0,1;0rad)
  FullyConstrained = true
  MapMode = 5
  Placement = pos=(0,-25.4,-5.6e-15) rot=(1,0,0;1.5708rad)
  Support = -> [XZ_Plane002]
  sketch-geometry (10):
    g0: LineSegment StartX=-5 StartY=41.8 StartZ=0 EndX=-31 EndY=41.8 EndZ=0
    g1: LineSegment StartX=-31 StartY=41.8 StartZ=0 EndX=-31 EndY=15.8 EndZ=0
    g2: LineSegment StartX=-31 StartY=15.8 StartZ=0 EndX=-5 EndY=15.8 EndZ=0
    g3: LineSegment StartX=-5 StartY=15.8 StartZ=0 EndX=-5 EndY=41.8 EndZ=0
    g4: Circle CenterX=-31 CenterY=41.8 CenterZ=0 NormalX=0 NormalY=0 NormalZ=1 AngleXU=0 Radius=1.5
    g5: Circle CenterX=-5 CenterY=41.8 CenterZ=0 NormalX=0 NormalY=0 NormalZ=1 AngleXU=0 Radius=1.5
    g6: Circle CenterX=-5 CenterY=15.8 CenterZ=0 NormalX=0 NormalY=0 NormalZ=1 AngleXU=0 Radius=1.5
    g7: Circle CenterX=-31 CenterY=15.8 CenterZ=0 NormalX=0 NormalY=0 NormalZ=1 AngleXU=0 Radius=1.5
    g8: GeomPoint X=-18 Y=28.8 Z=0
    g9: Circle CenterX=-18 CenterY=28.8 CenterZ=0 NormalX=0 NormalY=0 NormalZ=1 AngleXU=0 Radius=11.5
  constraints (23):
    c: Coincident(g0,g1)
    c: Coincident(g1,g2)
    c: Coincident(g2,g3)
    c: Coincident(g3,g0)
    c: Equal(g0,g1)
    c: Equal(g0,g2)
    c: Equal(g0,g3)
    c: Perpendicular(g0,g1)
    c: Coincident(g4,g0)
    c: Coincident(g5,g0)
    c: Coincident(g6,g2)
    c: Coincident(g7,g1)
    c: Equal(g7,g4)
    c: Equal(g4,g5)
    c: Equal(g5,g6)
    c: Diameter(g6) = 3
    c: Symmetric(g4,g6,g8)
    c: Distance(g3) = 26
    c: Vertical(g3)
    c: Coincident(g9,g8)
    c: Diameter(g9) = 23
    c: DistanceX(g9) = -18
    c: DistanceY(g9) = 28.8
FEATURE [PartDesign::Pocket] Pocket010
  BaseFeature = -> Pocket009
  Direction = (0,1,2e-16)
  Length = 2
  Length2 = 5
  Placement = pos=(0,0,0) rot=(1,0,0;1.5708rad)
  Profile = -> Sketch035
  ReferenceAxis = -> Sketch035 [N_Axis]
  Type = 0
FEATURE [Sketcher::SketchObject] Sketch036
  AttachmentOffset = pos=(0,0,18) rot=(0,0,1;0rad)
  FullyConstrained = true
  MapMode = 5
  Placement = pos=(0,-18,-4e-15) rot=(1,0,0;1.5708rad)
  Support = -> [XZ_Plane011]
  sketch-geometry (4):
    g0: Circle CenterX=-41.5127 CenterY=24.2627 CenterZ=0 NormalX=0 NormalY=0 NormalZ=1 AngleXU=0 Radius=2.05
    g1: Circle CenterX=-36.9873 CenterY=19.7373 CenterZ=0 NormalX=0 NormalY=0 NormalZ=1 AngleXU=0 Radius=2.05
    g2: LineSegment StartX=-41.5127 StartY=24.2627 StartZ=0 EndX=-36.9873 EndY=19.7373 EndZ=0
    g3: Circle CenterX=-39.25 CenterY=22 CenterZ=0 NormalX=0 NormalY=0 NormalZ=1 AngleXU=0 Radius=6
  constraints (10):
    c: Equal(g1,g0)
    c: Coincident(g2,g0)
    c: Coincident(g2,g1)
    c: Angle(g-2,g2) = 0.785398
    c: Diameter(g0) = 4.1
    c: Distance(g0,g1) = 6.4
    c: Diameter(g3) = 12
    c: Symmetric(g0,g1,g3)
    c: DistanceY(g3) = 22
    c: DistanceX(g3,g-1) = 39.25
FEATURE [Sketcher::SketchObject] Sketch037
  AttachmentOffset = pos=(0,0,18) rot=(0,0,1;0rad)
  FullyConstrained = false
  MapMode = 5
  Placement = pos=(0,-18,-4e-15) rot=(1,0,0;1.5708rad)
  Support = -> [XZ_Plane017]
  sketch-geometry (9):
    g0: Circle CenterX=-2.26274 CenterY=2.26274 CenterZ=0 NormalX=0 NormalY=0 NormalZ=1 AngleXU=0 Radius=1.6
    g1: Circle CenterX=2.26274 CenterY=-2.26274 CenterZ=0 NormalX=0 NormalY=0 NormalZ=1 AngleXU=0 Radius=1.6
    g2: LineSegment StartX=-2.26274 StartY=2.26274 StartZ=0 EndX=2.26274 EndY=-2.26274 EndZ=0
    g3: Circle CenterX=0 CenterY=0 CenterZ=0 NormalX=0 NormalY=0 NormalZ=1 AngleXU=0 Radius=6
    g4: ArcOfCircle CenterX=0 CenterY=0 CenterZ=0 NormalX=0 NormalY=0 NormalZ=1 AngleXU=0 Radius=9 StartAngle=3.14159 EndAngle=6.13646
    g5: LineSegment StartX=8.9033 StartY=-1.31576 StartZ=0 EndX=9.58011 EndY=3.5 EndZ=0
    g6: ArcOfCircle CenterX=0 CenterY=0 CenterZ=0 NormalX=0 NormalY=0 NormalZ=1 AngleXU=0 Radius=6 StartAngle=0.622827 EndAngle=2.93088
    g7: LineSegment StartX=4.8734 StartY=3.5 StartZ=0 EndX=9.58011 EndY=3.5 EndZ=0
    g8: LineSegment StartX=-5.86729 StartY=1.25496 StartZ=0 EndX=-9 EndY=1.1e-15 EndZ=0
  constraints (22):
    c: Equal(g1,g0)
    c: Coincident(g2,g0)
    c: Coincident(g2,g1)
    c: Angle(g-2,g2) = 0.785398
    c: Diameter(g0) = 3.2
    c: Distance(g0,g1) = 6.4
    c: Diameter(g3) = 12
    c: Symmetric(g0,g1,g3)
    c: Coincident(g3,g-1)
    c: Coincident(g4,g3)
    c: Coincident(g5,g4)
    c: Diameter(g4) = 18
    c: PointOnObject(g4,g-1)
    c: Angle(g5,g-1) = 1.71042
    c: Coincident(g6,g4)
    c: PointOnObject(g6,g3)
    c: Coincident(g7,g6)
    c: Coincident(g7,g5)
    c: Coincident(g8,g6)
    c: Coincident(g8,g4)
    c: Horizontal(g7)
    c: DistanceY(g4,g6) = 3.5
FEATURE [PartDesign::Pad] Pad013
  Direction = (0,-1,2e-16)
  Length = 2
  Length2 = 10
  Placement = pos=(0,0,0) rot=(1,0,0;1.5708rad)
  Profile = -> Sketch037
  ReferenceAxis = -> Sketch037 [N_Axis]
  Type = 0
FEATURE [Sketcher::SketchObject] Sketch038
  AttachmentOffset = pos=(0,0,18) rot=(0,0,1;0rad)
  FullyConstrained = false
  MapMode = 5
  Placement = pos=(0,-18,-4e-15) rot=(1,0,0;1.5708rad)
  Support = -> [XZ_Plane017]
  sketch-geometry (9):
    g0: Circle CenterX=-2.26274 CenterY=2.26274 CenterZ=0 NormalX=0 NormalY=0 NormalZ=1 AngleXU=0 Radius=1.6
    g1: Circle CenterX=2.26274 CenterY=-2.26274 CenterZ=0 NormalX=0 NormalY=0 NormalZ=1 AngleXU=0 Radius=1.6
    g2: LineSegment StartX=-2.26274 StartY=2.26274 StartZ=0 EndX=2.26274 EndY=-2.26274 EndZ=0
    g3: Circle CenterX=0 CenterY=0 CenterZ=0 NormalX=0 NormalY=0 NormalZ=1 AngleXU=0 Radius=6.2
    g4: ArcOfCircle CenterX=0 CenterY=0 CenterZ=0 NormalX=0 NormalY=0 NormalZ=1 AngleXU=0 Radius=9 StartAngle=3.14159 EndAngle=6.1431
    g5: LineSegment StartX=8.91183 StartY=-1.25668 StartZ=0 EndX=9.58034 EndY=3.5 EndZ=0
    g6: LineSegment StartX=5.11762 StartY=3.5 StartZ=0 EndX=9.58034 EndY=3.5 EndZ=0
    g7: LineSegment StartX=-6.07152 StartY=1.25565 StartZ=0 EndX=-9 EndY=0 EndZ=0
    g8: ArcOfCircle CenterX=0 CenterY=0 CenterZ=0 NormalX=0 NormalY=0 NormalZ=1 AngleXU=0 Radius=6.2 StartAngle=2.93766 EndAngle=6.88303
  constraints (22):
    c: Equal(g1,g0)
    c: Coincident(g2,g0)
    c: Coincident(g2,g1)
    c: Angle(g-2,g2) = 0.785398
    c: Diameter(g0) = 3.2
    c: Distance(g0,g1) = 6.4
    c: Diameter(g3) = 12.4
    c: Symmetric(g0,g1,g3)
    c: Coincident(g3,g-1)
    c: Coincident(g4,g3)
    c: Coincident(g5,g4)
    c: Diameter(g4) = 18
    c: PointOnObject(g4,g-1)
    c: Angle(g5,g-1) = 1.71042
    c: PointOnObject(g7,g3)
    c: Coincident(g6,g5)
    c: Coincident(g7,g4)
    c: Coincident(g8,g4)
    c: Coincident(g8,g7)
    c: Coincident(g8,g6)
    c: Horizontal(g6)
    c: DistanceY(g4,g6) = 3.5
FEATURE [PartDesign::Pad] Pad014
  BaseFeature = -> Pad013
  Direction = (0,-1,2e-16)
  Length = 2.9
  Length2 = 10
  Placement = pos=(0,0,0) rot=(1,0,0;1.5708rad)
  Profile = -> Sketch038
  ReferenceAxis = -> Sketch038 [N_Axis]
  Reversed = true
  Type = 0
FEATURE [PartDesign::Body] Body008  label="PivotClamp"
  Group = -> [Sketch037,Pad013,Sketch038,Pad014]
  Origin = -> Origin017
  Placement = pos=(-39.243,-0.0508,0.3302) rot=(0,0,1;0rad)
  Tip = -> Pad014
FEATURE [Sketcher::SketchObject] Sketch039
  FullyConstrained = true
  MapMode = 5
  Support = -> [XY_Plane018]
  sketch-geometry (1):
    g0: Circle CenterX=0 CenterY=0 CenterZ=0 NormalX=0 NormalY=0 NormalZ=1 AngleXU=0 Radius=1.5
  constraints (2):
    c: Coincident(g0,g-1)
    c: Diameter(g0) = 3
FEATURE [PartDesign::Pad] Pad015
  Direction = (0,0,1)
  Length = 9
  Length2 = 10
  Profile = -> Sketch039
  ReferenceAxis = -> Sketch039 [N_Axis]
  Type = 0
FEATURE [PartDesign::Body] Body009  label="BearingPin"
  Group = -> [Sketch039,Pad015]
  Origin = -> Origin018
  Placement = pos=(4.2,9.6,27.9) rot=(0,-1,0;1.5708rad)
  Tip = -> Pad015
FEATURE [Mesh::Feature] NEMA_17  label="NEMA 17"
  Placement = pos=(-25.7604,18.049,-60.4) rot=(0,0,-1;0.872665rad)
FEATURE [Part::FeaturePython] InvoluteGear003  # WARN: FeaturePython — macro-defined, semantics opaque (R4)
  AttacherType = Attacher::AttachEngine3D
  Placement = pos=(-28.8996,28.9131,-12.4) rot=(0,0,-1;1.74533rad)
  angular_backlash = 0
  backlash = 0
  beta = 0
  clearance = 0.25
  da = 20
  df = 15.5
  double_helix = false
  dw = 18
  head = 0
  head_fillet = 0
  height = 5
  module = 1
  numpoints = 6
  pressure_angle = 20
  properties_from_tool = false
  reversed_backlash = false
  root_fillet = 0
  shift = 0
  simple = false
  teeth = 18
  transverse_pitch = 3.14159
  traverse_module = 1
  undercut = false
  version = 0.0.4
  expr: angular_backlash = backlash / dw * 360° / pi
FEATURE [PartDesign::FeatureBase] BaseFeature001
  BaseFeature = -> InvoluteGear003
FEATURE [PartDesign::Pocket] Pocket011
  BaseFeature = -> Pad009
  Direction = (0,0,-1)
  Length = 5
  Length2 = 5
  Profile = -> Sketch024
  ReferenceAxis = -> Sketch024 [N_Axis]
  Reversed = true
  Type = 1
FEATURE [PartDesign::Pocket] Pocket012
  BaseFeature = -> Pocket011
  Direction = (0,1,2e-16)
  Length = 10
  Length2 = 5
  Profile = -> Sketch036
  ReferenceAxis = -> Sketch036 [N_Axis]
  Type = 0
FEATURE [PartDesign::Pocket] Pocket013
  BaseFeature = -> Pocket012
  Direction = (0,0,-1)
  Length = 5
  Length2 = 5
  Profile = -> Sketch030
  ReferenceAxis = -> Sketch030 [N_Axis]
  Reversed = true
  Type = 0
FEATURE [Sketcher::SketchObject] Sketch040
  AttachmentOffset = pos=(0,0,38) rot=(0,0,1;0rad)
  FullyConstrained = false
  MapMode = 5
  Placement = pos=(0,0,38) rot=(0,0,1;0rad)
  Support = -> [XY_Plane]
  sketch-geometry (10):
    g0: Circle CenterX=0 CenterY=0 CenterZ=0 NormalX=0 NormalY=0 NormalZ=1 AngleXU=0 Radius=16.8346
    g1: Circle CenterX=0 CenterY=13.2 CenterZ=0 NormalX=0 NormalY=0 NormalZ=1 AngleXU=0 Radius=2.7
    g2: Circle CenterX=11.4315 CenterY=6.6 CenterZ=0 NormalX=0 NormalY=0 NormalZ=1 AngleXU=0 Radius=2.7
    g3: Circle CenterX=11.4315 CenterY=-6.6 CenterZ=0 NormalX=0 NormalY=0 NormalZ=1 AngleXU=0 Radius=2.7
    g4: Circle CenterX=0 CenterY=-13.2 CenterZ=0 NormalX=0 NormalY=0 NormalZ=1 AngleXU=0 Radius=2.7
    g5: Circle CenterX=-11.4315 CenterY=-6.6 CenterZ=0 NormalX=0 NormalY=0 NormalZ=1 AngleXU=0 Radius=2.7
    g6: Circle CenterX=-11.4315 CenterY=6.6 CenterZ=0 NormalX=0 NormalY=0 NormalZ=1 AngleXU=0 Radius=2.7
    g7: LineSegment StartX=-11.4315 StartY=6.6 StartZ=0 EndX=11.4315 EndY=-6.6 EndZ=0
    g8: LineSegment StartX=11.4315 StartY=6.6 StartZ=0 EndX=-11.4315 EndY=-6.6 EndZ=0
    g9: LineSegment StartX=0 StartY=13.2 StartZ=0 EndX=0 EndY=-13.2 EndZ=0
  constraints (22):
    c: Coincident(g0,g-1)
    c: PointOnObject(g1,g-2)
    c: Coincident(g7,g6)
    c: Coincident(g7,g3)
    c: Coincident(g8,g2)
    c: Coincident(g8,g5)
    c: Coincident(g9,g1)
    c: Coincident(g9,g4)
    c: Symmetric(g1,g4,g0)
    c: Symmetric(g2,g5,g0)
    c: Symmetric(g3,g6,g0)
    c: Equal(g6,g1)
    c: Equal(g1,g2)
    c: Equal(g2,g3)
    c: Equal(g3,g4)
    c: Equal(g4,g5)
    c: Angle(g-1,g7) = 2.61799
    c: DistanceY(g0,g1) = 13.2
    c: Angle(g-1,g8) = 0.523599
    c: Equal(g7,g8)
    c: Equal(g8,g9)
    c: Diameter(g6) = 5.4
FEATURE [Sketcher::SketchObject] Sketch041
  AttachmentOffset = pos=(0,0,5) rot=(0,0,1;0rad)
  FullyConstrained = true
  MapMode = 5
  Placement = pos=(0,0,5) rot=(0,0,1;0rad)
  Support = -> [XY_Plane019]
  sketch-geometry (2):
    g0: Circle CenterX=0 CenterY=0 CenterZ=0 NormalX=0 NormalY=0 NormalZ=1 AngleXU=0 Radius=2.5
    g1: Circle CenterX=0 CenterY=0 CenterZ=0 NormalX=0 NormalY=0 NormalZ=1 AngleXU=0 Radius=7
  constraints (4):
    c: Coincident(g0,g-1)
    c: Coincident(g1,g0)
    c: Diameter(g0) = 5
    c: Diameter(g1) = 14
FEATURE [PartDesign::Pad] Pad017
  BaseFeature = -> BaseFeature001
  Direction = (0,0,1)
  Length = 8
  Length2 = 10
  Profile = -> Sketch041
  ReferenceAxis = -> Sketch041 [N_Axis]
  Type = 0
FEATURE [Sketcher::SketchObject] Sketch042
  FullyConstrained = true
  MapMode = 5
  Support = -> [XY_Plane019]
  sketch-geometry (1):
    g0: Circle CenterX=0 CenterY=0 CenterZ=0 NormalX=0 NormalY=0 NormalZ=1 AngleXU=0 Radius=2.5
  constraints (2):
    c: Coincident(g0,g-1)
    c: Diameter(g0) = 5
FEATURE [PartDesign::Pocket] Pocket014
  BaseFeature = -> Pad017
  Direction = (0,0,-1)
  Length = 5
  Length2 = 5
  Midplane = true
  Profile = -> Sketch042
  ReferenceAxis = -> Sketch042 [N_Axis]
  Type = 1
FEATURE [Sketcher::SketchObject] Sketch043
  FullyConstrained = true
  MapMode = 5
  Placement = pos=(0,0,0) rot=(0.57735,0.57735,0.57735;2.0944rad)
  Support = -> [YZ_Plane019]
  sketch-geometry (1):
    g0: Circle CenterX=0 CenterY=9 CenterZ=0 NormalX=0 NormalY=0 NormalZ=1 AngleXU=0 Radius=2.3
  constraints (3):
    c: PointOnObject(g0,g-2)
    c: DistanceY(g-1,g0) = 9
    c: Diameter(g0) = 4.6
FEATURE [PartDesign::Pocket] Pocket015
  BaseFeature = -> Pocket014
  Direction = (-1,2e-16,-3e-16)
  Length = 5
  Length2 = 5
  Profile = -> Sketch043
  ReferenceAxis = -> Sketch043 [N_Axis]
  Type = 1
FEATURE [PartDesign::Body] Body010  label="SmallGear"
  BaseFeature = -> InvoluteGear003
  Group = -> [BaseFeature001,Sketch041,Pad017,Sketch042,Pocket014,Sketch043,Pocket015]
  Origin = -> Origin019
  Placement = pos=(-28.9,28.9,-12.2) rot=(0,0,1;0.872665rad)
  Tip = -> Pocket015
FEATURE [Part::Feature] Part__Feature058  label="pc4-m012"
  Placement = pos=(-8.7808,-5.0626,-32.481) rot=(0,1,0;3.14159rad)
  shape: bbox 11.55 x 11.55 x 20.8 mm, 84 faces (baked)
FEATURE [Sketcher::SketchObject] Sketch044
  AttachmentOffset = pos=(0,0,2) rot=(0,0,1;0rad)
  FullyConstrained = true
  MapMode = 5
  Placement = pos=(0,0,-2) rot=(0,1,0;3.14159rad)
  Support = -> [XY_Plane021]
  sketch-geometry (3):
    g0: Circle CenterX=8.83346 CenterY=-5.1 CenterZ=0 NormalX=0 NormalY=0 NormalZ=1 AngleXU=0 Radius=1
    g1: Circle CenterX=8.83346 CenterY=-5.1 CenterZ=0 NormalX=0 NormalY=0 NormalZ=1 AngleXU=0 Radius=5
    g2: LineSegment StartX=0 StartY=0 StartZ=0 EndX=8.83346 EndY=-5.1 EndZ=0
  constraints (7):
    c: Diameter(g0) = 2
    c: Coincident(g1,g0)
    c: Distance(g-1,g0) = 10.2
    c: Coincident(g2,g-1)
    c: Coincident(g2,g0)
    c: Angle(g2,g-1) = 0.523599
    c: Diameter(g1) = 10
FEATURE [PartDesign::Pad] Pad018
  Direction = (0,0,-1)
  Length = 13
  Length2 = 10
  Profile = -> Sketch044
  ReferenceAxis = -> Sketch044 [N_Axis]
  Type = 0
FEATURE [Sketcher::SketchObject] Sketch045
  AttachmentOffset = pos=(0,0,10) rot=(0,0,1;0rad)
  FullyConstrained = true
  MapMode = 5
  Placement = pos=(0,0,-10) rot=(0,1,0;3.14159rad)
  Support = -> [XY_Plane021]
  sketch-geometry (2):
    g0: Circle CenterX=8.83346 CenterY=-5.1 CenterZ=0 NormalX=0 NormalY=0 NormalZ=1 AngleXU=0 Radius=2.85
    g1: LineSegment StartX=0 StartY=0 StartZ=0 EndX=8.83346 EndY=-5.1 EndZ=0
  constraints (5):
    c: Diameter(g0) = 5.7
    c: Distance(g-1,g0) = 10.2
    c: Coincident(g1,g-1)
    c: Coincident(g1,g0)
    c: Angle(g1,g-1) = 0.523599
FEATURE [PartDesign::Pocket] Pocket016
  BaseFeature = -> Pad018
  Direction = (0,0,1)
  Length = 10
  Length2 = 5
  Profile = -> Sketch045
  ReferenceAxis = -> Sketch045 [N_Axis]
  Reversed = true
  Type = 0
FEATURE [Part::Feature] Part__Feature059  label="Regular Duty Utility Blade"
  Placement = pos=(-3.16802,-30.8019,1.997) rot=(-0.834817,-0.389282,0.389282;1.75037rad)
  shape: bbox 39.71 x 42.18 x 0.43 mm, 465 faces (baked)
FEATURE [Sketcher::SketchObject] Sketch046
  AttachmentOffset = pos=(0,0,-5.4) rot=(0,0,1;0rad)
  FullyConstrained = false
  MapMode = 5
  Placement = pos=(0,0,5.4) rot=(0,1,0;3.14159rad)
  Support = -> [XY_Plane022]
  sketch-geometry (5):
    g0: LineSegment StartX=-3.53294 StartY=-34.7182 StartZ=0 EndX=34.5516 EndY=-54.4833 EndZ=0
    g1: LineSegment StartX=34.5516 StartY=-54.4833 StartZ=0 EndX=48.5124 EndY=-27.5826 EndZ=0
    g2: LineSegment StartX=48.5124 StartY=-27.5826 StartZ=0 EndX=15.7854 EndY=-10.598 EndZ=0
    g3: LineSegment StartX=15.7854 StartY=-10.598 StartZ=0 EndX=-4.29767 EndY=-28.8365 EndZ=0
    g4: ArcOfCircle CenterX=-1.8686 CenterY=-31.5113 CenterZ=0 NormalX=0 NormalY=0 NormalZ=1 AngleXU=0 Radius=3.61312 StartAngle=2.3081 EndAngle=4.23367
  constraints (7):
    c: Coincident(g1,g0)
    c: Coincident(g2,g1)
    c: Coincident(g3,g2)
    c: Perpendicular(g1,g0)
    c: Perpendicular(g2,g1)
    c: Tangent(g0,g4) = -1.5708
    c: Tangent(g3,g4) = -1.5708
FEATURE [PartDesign::Pad] Pad019
  Direction = (0,0,-1)
  Length = 7
  Length2 = 10
  Profile = -> Sketch046
  ReferenceAxis = -> Sketch046 [N_Axis]
  Type = 0
FEATURE [Sketcher::SketchObject] Sketch047
  AttachmentOffset = pos=(0,0,0.9) rot=(0,0,1;0rad)
  FullyConstrained = false
  MapMode = 5
  Placement = pos=(0,0,-0.9) rot=(0,1,0;3.14159rad)
  Support = -> [XY_Plane022]
  sketch-geometry (13):
    g0: LineSegment StartX=-6.79299 StartY=-20 StartZ=0 EndX=12.4105 EndY=-42.8858 EndZ=0
    g1: LineSegment StartX=12.4105 StartY=-42.8858 StartZ=0 EndX=38.6194 EndY=-43.0059 EndZ=0
    g2: LineSegment StartX=38.6194 StartY=-43.0059 StartZ=0 EndX=8.52789 EndY=-7.14425 EndZ=0
    g3: LineSegment StartX=12.4105 StartY=-42.8858 StartZ=0 EndX=27.7314 EndY=-30.0301 EndZ=0
    g4: LineSegment StartX=-6.79299 StartY=-20 StartZ=0 EndX=8.52789 EndY=-7.14425 EndZ=0
    g5: Circle CenterX=17.8 CenterY=-14.3 CenterZ=0 NormalX=0 NormalY=0 NormalZ=1 AngleXU=0 Radius=4
    g6: Circle CenterX=33.2269 CenterY=-32.6851 CenterZ=0 NormalX=0 NormalY=0 NormalZ=1 AngleXU=0 Radius=4
    g7: LineSegment StartX=17.8 StartY=-14.3 StartZ=0 EndX=33.2269 EndY=-32.6851 EndZ=0
    g8: LineSegment StartX=2.66816 StartY=-26.9971 StartZ=0 EndX=17.8 EndY=-14.3 EndZ=0
    g9: Circle CenterX=2.66816 CenterY=-26.9971 CenterZ=0 NormalX=0 NormalY=0 NormalZ=1 AngleXU=0 Radius=4
    g10: LineSegment StartX=2.66816 StartY=-26.9971 StartZ=0 EndX=7.04734 EndY=-32.216 EndZ=0
    g11: LineSegment StartX=2.66816 StartY=-26.9971 StartZ=0 EndX=0.561536 EndY=-28.7648 EndZ=0
    g12: Circle CenterX=2.66816 CenterY=-26.9971 CenterZ=0 NormalX=0 NormalY=0 NormalZ=1 AngleXU=0 Radius=1.30777
  constraints (31):
    c: Coincident(g1,g0)
    c: Coincident(g2,g1)
    c: Parallel(g2,g0)
    c: Coincident(g3,g0)
    c: PointOnObject(g3,g2)
    c: Perpendicular(g0,g3)
    c: Distance(g3) = 20
    c: Angle(g0,g-2) = 2.44346
    c: Coincident(g4,g2)
    c: Coincident(g4,g0)
    c: DistanceY(g0,g-1) = 20
    c: Perpendicular(g2,g4)
    c: Equal(g6,g5)
    c: Diameter(g5) = 8
    c: Coincident(g7,g5)
    c: Coincident(g7,g6)
    c: Coincident(g5,g8)
    c: Perpendicular(g8,g7)
    c: Coincident(g9,g8)
    c: Coincident(g10,g8)
    c: Perpendicular(g8,g10)
    c: Parallel(g10,g0)
    c: DistanceY(g5,g-1) = 14.3
    c: Distance(g7) = 24
    c: DistanceX(g-1,g5) = 17.8
    c: Equal(g9,g5)
    c: Coincident(g11,g8)
    c: PointOnObject(g11,g0)
    c: Perpendicular(g0,g11)
    c: Coincident(g12,g8)
    c: Distance(g11) = 2.75
FEATURE [PartDesign::Pocket] Pocket017
  BaseFeature = -> Pad019
  Direction = (0,0,1)
  Length = 5
  Length2 = 5
  Profile = -> Sketch047
  ReferenceAxis = -> Sketch047 [N_Axis]
  Reversed = true
  Type = 0
FEATURE [Sketcher::SketchObject] Sketch048
  AttachmentOffset = pos=(0,0,0.9) rot=(0,0,1;0rad)
  FullyConstrained = false
  MapMode = 5
  Placement = pos=(0,0,-0.9) rot=(0,1,0;3.14159rad)
  Support = -> [XY_Plane022]
  sketch-geometry (16):
    g0: LineSegment StartX=-6.34064 StartY=-20 StartZ=0 EndX=11.7 EndY=-41.5 EndZ=0
    g1: LineSegment StartX=11.7 StartY=-41.5 StartZ=0 EndX=35.0541 EndY=-38.2178 EndZ=0
    g2: LineSegment StartX=35.0541 StartY=-38.2178 StartZ=0 EndX=8.98025 EndY=-7.14425 EndZ=0
    g3: LineSegment StartX=11.7 StartY=-41.5 StartZ=0 EndX=27.0209 EndY=-28.6442 EndZ=0
    g4: LineSegment StartX=-6.34064 StartY=-20 StartZ=0 EndX=8.98025 EndY=-7.14425 EndZ=0
    g5: Circle CenterX=2.97842 CenterY=-26.75 CenterZ=0 NormalX=0 NormalY=0 NormalZ=1 AngleXU=0 Radius=1.55
    g6: Circle CenterX=7.02798 CenterY=-31.5761 CenterZ=0 NormalX=0 NormalY=0 NormalZ=1 AngleXU=0 Radius=1.55
    g7: LineSegment StartX=2.97842 StartY=-26.75 StartZ=0 EndX=7.02798 EndY=-31.5761 EndZ=0
    g8: GeomPoint X=0.833496 Y=-28.5498 Z=0
    g9: LineSegment StartX=0.833496 StartY=-28.5498 StartZ=0 EndX=2.97842 EndY=-26.75 EndZ=0
    g10: Circle CenterX=32.9602 CenterY=-32.9221 CenterZ=0 NormalX=0 NormalY=0 NormalZ=1 AngleXU=0 Radius=1.95
    g11: Circle CenterX=32.9602 CenterY=-32.9221 CenterZ=0 NormalX=0 NormalY=0 NormalZ=1 AngleXU=0 Radius=1.95
    g12: Circle CenterX=17.5333 CenterY=-14.537 CenterZ=0 NormalX=0 NormalY=0 NormalZ=1 AngleXU=0 Radius=1.55
    g13: Circle CenterX=17.5333 CenterY=-14.537 CenterZ=0 NormalX=0 NormalY=0 NormalZ=1 AngleXU=0 Radius=1.95
    g14: LineSegment StartX=17.5333 StartY=-14.537 StartZ=0 EndX=32.9602 EndY=-32.9221 EndZ=0
    g15: LineSegment StartX=2.97842 StartY=-26.75 StartZ=0 EndX=17.5333 EndY=-14.537 EndZ=0
  constraints (39):
    c: Coincident(g1,g0)
    c: Coincident(g2,g1)
    c: Parallel(g2,g0)
    c: Coincident(g3,g0)
    c: PointOnObject(g3,g2)
    c: Perpendicular(g0,g3)
    c: Distance(g3) = 20
    c: DistanceX(g-1,g0) = 11.7
    c: DistanceY(g0,g-1) = 41.5
    c: Angle(g0,g-2) = 2.44346
    c: Coincident(g4,g2)
    c: Coincident(g4,g0)
    c: DistanceY(g0,g-1) = 20
    c: Perpendicular(g2,g4)
    c: Angle(g1,g0) = 2.1293
    c: Equal(g5,g6)
    c: Coincident(g7,g5)
    c: Coincident(g7,g6)
    c: Parallel(g7,g0)
    c: PointOnObject(g8,g0)
    c: Coincident(g9,g8)
    c: Coincident(g9,g5)
    c: Perpendicular(g0,g9)
    c: Distance(g9) = 2.8
    c: Distance(g6,g5) = 6.3
    c: Coincident(g11,g10)
    c: Coincident(g13,g12)
    c: Coincident(g14,g12)
    c: Coincident(g14,g10)
    c: Parallel(g14,g2)
    c: Diameter(g5) = 3.1
    c: Distance(g14) = 24
    c: Coincident(g15,g5)
    c: Coincident(g15,g12)
    c: Perpendicular(g14,g15)
    c: Diameter(g12) = 3.1
    c: Diameter(g10) = 3.9
    c: Distance(g15) = 19
    c: DistanceY(g5,g-1) = 26.75
FEATURE [PartDesign::Pocket] Pocket018
  BaseFeature = -> Pocket017
  Direction = (0,0,1)
  Length = 5
  Length2 = 5
  Midplane = true
  Profile = -> Sketch048
  ReferenceAxis = -> Sketch048 [N_Axis]
  Type = 1
FEATURE [Sketcher::SketchObject] Sketch049
  AttachmentOffset = pos=(0,0,0.9) rot=(0,0,1;0rad)
  FullyConstrained = false
  MapMode = 5
  Placement = pos=(0,0,-0.9) rot=(0,1,0;3.14159rad)
  Support = -> [XY_Plane022]
  sketch-geometry (13):
    g0: LineSegment StartX=-6.34064 StartY=-20 StartZ=0 EndX=11.7 EndY=-41.5 EndZ=0
    g1: LineSegment StartX=11.7 StartY=-41.5 StartZ=0 EndX=35.0541 EndY=-38.2178 EndZ=0
    g2: LineSegment StartX=35.0541 StartY=-38.2178 StartZ=0 EndX=8.98025 EndY=-7.14425 EndZ=0
    g3: LineSegment StartX=11.7 StartY=-41.5 StartZ=0 EndX=27.0209 EndY=-28.6442 EndZ=0
    g4: LineSegment StartX=-6.34064 StartY=-20 StartZ=0 EndX=8.98025 EndY=-7.14425 EndZ=0
    g5: Circle CenterX=17.4626 CenterY=-14.5306 CenterZ=0 NormalX=0 NormalY=0 NormalZ=1 AngleXU=0 Radius=5
    g6: Circle CenterX=32.8895 CenterY=-32.9157 CenterZ=0 NormalX=0 NormalY=0 NormalZ=1 AngleXU=0 Radius=4.5
    g7: LineSegment StartX=17.4626 StartY=-14.5306 StartZ=0 EndX=32.8895 EndY=-32.9157 EndZ=0
    g8: LineSegment StartX=2.90774 StartY=-26.7435 StartZ=0 EndX=17.4626 EndY=-14.5306 EndZ=0
    g9: Circle CenterX=2.90774 CenterY=-26.7435 CenterZ=0 NormalX=0 NormalY=0 NormalZ=1 AngleXU=0 Radius=3.5
    g10: LineSegment StartX=2.90774 StartY=-26.7435 StartZ=0 EndX=7.31086 EndY=-31.991 EndZ=0
    g11: LineSegment StartX=2.90774 StartY=-26.7435 StartZ=0 EndX=0.801116 EndY=-28.5112 EndZ=0
    g12: Circle CenterX=2.90774 CenterY=-26.7435 CenterZ=0 NormalX=0 NormalY=0 NormalZ=1 AngleXU=0 Radius=1.30777
  constraints (33):
    c: Coincident(g1,g0)
    c: Coincident(g2,g1)
    c: Parallel(g2,g0)
    c: Coincident(g3,g0)
    c: PointOnObject(g3,g2)
    c: Perpendicular(g0,g3)
    c: Distance(g3) = 20
    c: DistanceX(g-1,g0) = 11.7
    c: DistanceY(g0,g-1) = 41.5
    c: Angle(g0,g-2) = 2.44346
    c: Coincident(g4,g2)
    c: Coincident(g4,g0)
    c: DistanceY(g0,g-1) = 20
    c: Perpendicular(g2,g4)
    c: Angle(g1,g0) = 2.1293
    c: Coincident(g7,g5)
    c: Coincident(g7,g6)
    c: Coincident(g5,g8)
    c: Perpendicular(g8,g7)
    c: Coincident(g9,g8)
    c: Coincident(g10,g8)
    c: Perpendicular(g8,g10)
    c: Parallel(g10,g0)
    c: Distance(g7) = 24
    c: Coincident(g11,g8)
    c: PointOnObject(g11,g0)
    c: Perpendicular(g0,g11)
    c: Coincident(g12,g8)
    c: Distance(g11) = 2.75
    c: Diameter(g5) = 10
    c: Diameter(g9) = 7
    c: Diameter(g6) = 9
    c: Distance(g8) = 19
FEATURE [PartDesign::Pocket] Pocket019
  BaseFeature = -> Pocket018
  Direction = (0,0,1)
  Length = 5
  Length2 = 5
  Profile = -> Sketch049
  ReferenceAxis = -> Sketch049 [N_Axis]
  Reversed = true
  Type = 0
FEATURE [PartDesign::Body] Body012  label="BladeClamp"
  Group = -> [Sketch046,Pad019,Sketch047,Pocket017,Sketch048,Pocket018,Sketch049,Pocket019]
  Origin = -> Origin022
  Tip = -> Pocket019
FEATURE [Part::FeaturePython] Screw  label="M3x10-Screw"  # Fasteners workbench fastener (typed FeaturePython)
  Placement = pos=(-3,-26.7,-2) rot=(0,1,0;3.14159rad)
  diameter = 1
  invert = false
  leftHanded = false
  length = 2
  lengthCustom = 10
  matchOuter = false
  offset = 0
  thread = false
  type = 42
FEATURE [Part::FeaturePython] Screw001  label="M3x10-Screw007"  # Fasteners workbench fastener (typed FeaturePython)
  Placement = pos=(-17.478,-14.551,-5.3) rot=(-0.42305,0.906106,0;3.14159rad)
  diameter = 1
  invert = false
  leftHanded = false
  length = 2
  lengthCustom = 10
  matchOuter = false
  offset = 0
  thread = false
  type = 42
FEATURE [Part::FeaturePython] Screw002  label="M4x6-Screw"  # Fasteners workbench fastener (typed FeaturePython)
  Placement = pos=(-32.905,-32.936,-2) rot=(-0.42305,0.906106,0;3.14159rad)
  diameter = 2
  invert = false
  leftHanded = false
  length = 0
  lengthCustom = 6
  matchOuter = false
  offset = 0
  thread = false
  type = 42
FEATURE [Sketcher::SketchObject] Sketch050
  AttachmentOffset = pos=(0,0,15) rot=(0,0,1;0rad)
  FullyConstrained = false
  MapMode = 5
  Placement = pos=(0,0,-15) rot=(0,1,0;3.14159rad)
  Support = -> [XY_Plane021]
  sketch-geometry (9):
    g0: Circle CenterX=8.83346 CenterY=-5.1 CenterZ=0 NormalX=0 NormalY=0 NormalZ=1 AngleXU=0 Radius=1.5
    g1: LineSegment StartX=0 StartY=0 StartZ=0 EndX=8.83346 EndY=-5.1 EndZ=0
    g2: LineSegment StartX=13.5338 StartY=-3.39517 StartZ=0 EndX=8.50644 EndY=18.3809 EndZ=0
    g3: LineSegment StartX=-5.13651 StartY=20.0928 StartZ=0 EndX=3.83346 EndY=-5.09939 EndZ=0
    g4: LineSegment StartX=3.83346 StartY=-5.09939 StartZ=0 EndX=8.82712 EndY=-5.09939 EndZ=0
    g5: LineSegment StartX=8.83346 StartY=-5.1 StartZ=0 EndX=13.5338 EndY=-3.39517 EndZ=0
    g6: ArcOfCircle CenterX=8.83346 CenterY=-5.1 CenterZ=0 NormalX=0 NormalY=0 NormalZ=1 AngleXU=0 Radius=5 StartAngle=0.347945 EndAngle=3.14147
    g7: ArcOfCircle CenterX=0.0272413 CenterY=6.02577 CenterZ=0 NormalX=0 NormalY=0 NormalZ=1 AngleXU=0 Radius=14.9848 StartAngle=0.969331 EndAngle=1.92261
    g8: GeomPoint X=12.75 Y=0 Z=0
  constraints (19):
    c: Diameter(g0) = 3
    c: Distance(g-1,g0) = 10.2
    c: Coincident(g1,g-1)
    c: Coincident(g1,g0)
    c: Angle(g1,g-1) = 0.523599
    c: Coincident(g4,g3)
    c: Horizontal(g4)
    c: Coincident(g5,g2)
    c: Coincident(g6,g0)
    c: Coincident(g6,g3)
    c: Coincident(g6,g2)
    c: Diameter(g6) = 10
    c: Coincident(g5,g6)
    c: Angle(g2,g-1) = 1.3439
    c: Coincident(g7,g3)
    c: Coincident(g7,g2)
    c: PointOnObject(g8,g2)
    c: PointOnObject(g8,g-1)
    c: DistanceX(g1,g8) = 12.75
FEATURE [PartDesign::Pad] Pad020
  BaseFeature = -> Pocket016
  Direction = (0,0,-1)
  Length = 5
  Length2 = 10
  Profile = -> Sketch050
  ReferenceAxis = -> Sketch050 [N_Axis]
  Reversed = true
  Type = 0
FEATURE [Sketcher::SketchObject] Sketch051
  AttachmentOffset = pos=(0,0,-5) rot=(0,0,1;0rad)
  FullyConstrained = false
  MapMode = 5
  Placement = pos=(0,0,5) rot=(0,1,0;3.14159rad)
  Support = -> [XY_Plane021]
  sketch-geometry (7):
    g0: ArcOfCircle CenterX=0 CenterY=0 CenterZ=0 NormalX=0 NormalY=0 NormalZ=1 AngleXU=0 Radius=21.9404 StartAngle=1.19577 EndAngle=2.14643
    g1: LineSegment StartX=8.0367 StartY=20.4156 StartZ=0 EndX=12.75 EndY=0 EndZ=0
    g2: ArcOfCircle CenterX=0 CenterY=0 CenterZ=0 NormalX=0 NormalY=0 NormalZ=1 AngleXU=0 Radius=32.4633 StartAngle=1.40499 EndAngle=2.12098
    g3: LineSegment StartX=5.35804 StartY=32.0181 StartZ=0 EndX=8.0367 EndY=20.4156 EndZ=0
    g4: LineSegment StartX=-16.9731 StartY=27.6727 StartZ=0 EndX=-11.9437 EndY=18.4047 EndZ=0
    g5: Circle CenterX=-12.2657 CenterY=25.6173 CenterZ=0 NormalX=0 NormalY=0 NormalZ=1 AngleXU=0 Radius=1.55
    g6: Circle CenterX=2.47211 CenterY=28.4094 CenterZ=0 NormalX=0 NormalY=0 NormalZ=1 AngleXU=0 Radius=1.55
  constraints (14):
    c: Coincident(g0,g-1)
    c: Coincident(g1,g0)
    c: PointOnObject(g1,g-1)
    c: Angle(g1,g-1) = 1.3439
    c: Coincident(g2,g0)
    c: Coincident(g3,g2)
    c: Coincident(g3,g0)
    c: Coincident(g4,g2)
    c: Coincident(g4,g0)
    c: Equal(g6,g5)
    c: Diameter(g5) = 3.1
    c: Distance(g5,g6) = 15
    c: Parallel(g3,g1)
    c: DistanceX(g0,g1) = 12.75
FEATURE [Sketcher::SketchObject] Sketch052
  AttachmentOffset = pos=(0,0,15) rot=(0,0,1;0rad)
  FullyConstrained = false
  MapMode = 5
  Placement = pos=(0,0,-15) rot=(0,1,0;3.14159rad)
  Support = -> [XY_Plane021]
  expr: Constraints[0] = Sketch050.Constraints[0]
  expr: Constraints[11] = Sketch050.Constraints[11]
  expr: Constraints[13] = Sketch050.Constraints[13]
  expr: Constraints[1] = Sketch050.Constraints[1]
  expr: Constraints[4] = Sketch050.Constraints[4]
  sketch-geometry (12):
    g0: Circle CenterX=8.83346 CenterY=-5.1 CenterZ=0 NormalX=0 NormalY=0 NormalZ=1 AngleXU=0 Radius=1.5
    g1: LineSegment StartX=0 StartY=0 StartZ=0 EndX=8.83346 EndY=-5.1 EndZ=0
    g2: LineSegment StartX=13.5338 StartY=-3.39517 StartZ=0 EndX=9.79821 EndY=12.7856 EndZ=0
    g3: LineSegment StartX=-3.72421 StartY=16.2074 StartZ=0 EndX=3.83346 EndY=-5.09939 EndZ=0
    g4: LineSegment StartX=3.83346 StartY=-5.09939 StartZ=0 EndX=8.82712 EndY=-5.09939 EndZ=0
    g5: LineSegment StartX=8.83346 StartY=-5.1 StartZ=0 EndX=13.5338 EndY=-3.39517 EndZ=0
    g6: ArcOfCircle CenterX=8.83346 CenterY=-5.1 CenterZ=0 NormalX=0 NormalY=0 NormalZ=1 AngleXU=0 Radius=5 StartAngle=0.347945 EndAngle=3.14147
    g7: ArcOfCircle CenterX=0.809584 CenterY=5.6942 CenterZ=0 NormalX=0 NormalY=0 NormalZ=1 AngleXU=0 Radius=11.4492 StartAngle=0.667955 EndAngle=1.97795
    g8: ArcOfCircle CenterX=-0.51389 CenterY=-2.11697 CenterZ=0 NormalX=0 NormalY=0 NormalZ=1 AngleXU=0 Radius=23.576 StartAngle=1.19315 EndAngle=1.78597
    g9: LineSegment StartX=-5.54766 StartY=20.9154 StartZ=0 EndX=-3.72421 EndY=16.2074 EndZ=0
    g10: LineSegment StartX=8.17933 StartY=19.7978 StartZ=0 EndX=9.79821 EndY=12.7856 EndZ=0
    g11: GeomPoint X=12.75 Y=0 Z=0
  constraints (24):
    c: Diameter(g0) = 3
    c: Distance(g-1,g0) = 10.2
    c: Coincident(g1,g-1)
    c: Coincident(g1,g0)
    c: Angle(g1,g-1) = 0.523599
    c: Coincident(g4,g3)
    c: Horizontal(g4)
    c: Coincident(g5,g2)
    c: Coincident(g6,g0)
    c: Coincident(g6,g3)
    c: Coincident(g6,g2)
    c: Diameter(g6) = 10
    c: Coincident(g5,g6)
    c: Angle(g2,g-1) = 1.3439
    c: Coincident(g7,g3)
    c: Coincident(g7,g2)
    c: Coincident(g9,g8)
    c: Coincident(g9,g7)
    c: Coincident(g10,g8)
    c: Coincident(g10,g7)
    c: Parallel(g10,g2)
    c: PointOnObject(g11,g2)
    c: PointOnObject(g11,g-1)
    c: DistanceX(g1,g11) = 12.75
FEATURE [Sketcher::SketchObject] Sketch053
  AttachmentOffset = pos=(0,0,5) rot=(0,0,1;0rad)
  FullyConstrained = false
  MapMode = 5
  Placement = pos=(0,0,-5) rot=(0,1,0;3.14159rad)
  Support = -> [XY_Plane021]
  expr: Constraints[0] = Sketch050.Constraints[0]
  expr: Constraints[11] = Sketch050.Constraints[11]
  expr: Constraints[13] = Sketch050.Constraints[13]
  expr: Constraints[1] = Sketch050.Constraints[1]
  expr: Constraints[4] = Sketch050.Constraints[4]
  sketch-geometry (12):
    g0: Circle CenterX=8.83346 CenterY=-5.1 CenterZ=0 NormalX=0 NormalY=0 NormalZ=1 AngleXU=0 Radius=1.5
    g1: LineSegment StartX=0 StartY=0 StartZ=0 EndX=8.83346 EndY=-5.1 EndZ=0
    g2: LineSegment StartX=13.8055 StartY=-4.57178 StartZ=0 EndX=8.02315 EndY=20.4742 EndZ=0
    g3: LineSegment StartX=-11.9134 StartY=18.4834 StartZ=0 EndX=3.83346 EndY=-5.09939 EndZ=0
    g4: LineSegment StartX=3.83346 StartY=-5.09939 StartZ=0 EndX=8.82712 EndY=-5.09939 EndZ=0
    g5: LineSegment StartX=8.83346 StartY=-5.1 StartZ=0 EndX=13.8055 EndY=-4.57178 EndZ=0
    g6: ArcOfCircle CenterX=8.83346 CenterY=-5.1 CenterZ=0 NormalX=0 NormalY=0 NormalZ=1 AngleXU=0 Radius=5 StartAngle=0.105841 EndAngle=3.14147
    g7: ArcOfCircle CenterX=0 CenterY=0 CenterZ=0 NormalX=0 NormalY=0 NormalZ=1 AngleXU=0 Radius=21.9901 StartAngle=1.19732 EndAngle=2.14333
    g8: ArcOfCircle CenterX=0 CenterY=0 CenterZ=0 NormalX=0 NormalY=0 NormalZ=1 AngleXU=0 Radius=32.4253 StartAngle=1.4045 EndAngle=2.12159
    g9: LineSegment StartX=-16.9702 StartY=27.6299 StartZ=0 EndX=-11.9134 EndY=18.4834 EndZ=0
    g10: LineSegment StartX=5.36731 StartY=31.978 StartZ=0 EndX=8.02315 EndY=20.4742 EndZ=0
    g11: GeomPoint X=12.75 Y=0 Z=0
  constraints (26):
    c: Diameter(g0) = 3
    c: Distance(g-1,g0) = 10.2
    c: Coincident(g1,g-1)
    c: Coincident(g1,g0)
    c: Angle(g1,g-1) = 0.523599
    c: Coincident(g4,g3)
    c: Horizontal(g4)
    c: Coincident(g5,g2)
    c: Coincident(g6,g0)
    c: Coincident(g6,g3)
    c: Coincident(g6,g2)
    c: Diameter(g6) = 10
    c: Coincident(g5,g6)
    c: Angle(g2,g-1) = 1.3439
    c: Coincident(g7,g3)
    c: Coincident(g7,g2)
    c: Coincident(g9,g8)
    c: Coincident(g9,g7)
    c: Coincident(g10,g8)
    c: Coincident(g10,g7)
    c: Coincident(g7,g1)
    c: Coincident(g8,g7)
    c: Parallel(g2,g10)
    c: PointOnObject(g11,g2)
    c: PointOnObject(g11,g-1)
    c: DistanceX(g7,g11) = 12.75
FEATURE [PartDesign::AdditiveLoft] AdditiveLoft
  BaseFeature = -> Pad020
  Closed = false
  Profile = -> Sketch053
  Ruled = false
  Sections = -> [Sketch052]
FEATURE [PartDesign::Pad] Pad021
  BaseFeature = -> AdditiveLoft
  Direction = (0,0,-1)
  Length = 10
  Length2 = 10
  Profile = -> Sketch051
  ReferenceAxis = -> Sketch051 [N_Axis]
  Type = 0
FEATURE [Part::Feature] Part__Feature060  label="H-64B, Utility Blade v2"
  Placement = pos=(-37.2464,-41.5883,-0.9) rot=(-0.834817,-0.389282,0.389282;1.75037rad)
  shape: bbox 43.68 x 46.96 x 0.635 mm, 16 faces (baked)
FEATURE [Sketcher::SketchObject] Sketch054
  FullyConstrained = false
  MapMode = 5
  Placement = pos=(0,0,0) rot=(0,1,0;3.14159rad)
  Support = -> [XY_Plane011]
  sketch-geometry (8):
    g0: Circle CenterX=22.3661 CenterY=-3.85529 CenterZ=0 NormalX=0 NormalY=0 NormalZ=1 AngleXU=0 Radius=2.1
    g1: Circle CenterX=15.8042 CenterY=-21.6862 CenterZ=0 NormalX=0 NormalY=0 NormalZ=1 AngleXU=0 Radius=2.1
    g2: Circle CenterX=44.8894 CenterY=-12.1439 CenterZ=0 NormalX=0 NormalY=0 NormalZ=1 AngleXU=0 Radius=1.70372
    g3: LineSegment StartX=22.3661 StartY=-3.85529 StartZ=0 EndX=15.8042 EndY=-21.6862 EndZ=0
    g4: LineSegment StartX=22.3661 StartY=-3.85529 StartZ=0 EndX=44.8894 EndY=-12.1439 EndZ=0
    g5: Circle CenterX=-23.1789 CenterY=16.186 CenterZ=0 NormalX=0 NormalY=0 NormalZ=1 AngleXU=0 Radius=2.1
    g6: Circle CenterX=-11.8552 CenterY=26.0233 CenterZ=0 NormalX=0 NormalY=0 NormalZ=1 AngleXU=0 Radius=2.1
    g7: LineSegment StartX=-23.1789 StartY=16.186 StartZ=0 EndX=-11.8552 EndY=26.0233 EndZ=0
  constraints (14):
    c: Coincident(g3,g0)
    c: Coincident(g3,g1)
    c: Coincident(g4,g0)
    c: Coincident(g4,g2)
    c: Distance(g3) = 19
    c: Distance(g4) = 24
    c: Perpendicular(g4,g3)
    c: Coincident(g7,g5)
    c: Coincident(g7,g6)
    c: Distance(g7) = 15
    c: Equal(g5,g6)
    c: Equal(g6,g0)
    c: Equal(g0,g1)
    c: Diameter(g6) = 4.2
FEATURE [Part::FeaturePython] Screw003  label="M3x10-Screw006"  # Fasteners workbench fastener (typed FeaturePython)
  Placement = pos=(-3,28.4,1.8) rot=(0,1,0;3.14159rad)
  diameter = 1
  invert = false
  leftHanded = false
  length = 2
  lengthCustom = 10
  matchOuter = false
  offset = 0
  thread = false
  type = 42
FEATURE [Part::FeaturePython] Screw004  label="M3x10-Screw003"  # Fasteners workbench fastener (typed FeaturePython)
  Placement = pos=(11.9,25.6,1.8) rot=(0,1,0;3.14159rad)
  diameter = 1
  invert = false
  leftHanded = false
  length = 2
  lengthCustom = 10
  matchOuter = false
  offset = 0
  thread = false
  type = 42
FEATURE [App::Part] Part005  label="Bolts"
  Group = -> [Screw,Screw001,Screw002,Screw003,Screw004]
  Origin = -> Origin023
FEATURE [PartDesign::Pocket] Pocket020
  BaseFeature = -> Pocket013
  Direction = (0,0,1)
  Length = 5
  Length2 = 5
  Profile = -> Sketch054
  ReferenceAxis = -> Sketch054 [N_Axis]
  Type = 0
FEATURE [Sketcher::SketchObject] Sketch055
  FullyConstrained = true
  MapMode = 5
  Support = -> [XY_Plane024]
  sketch-geometry (1):
    g0: Circle CenterX=0 CenterY=0 CenterZ=0 NormalX=0 NormalY=0 NormalZ=1 AngleXU=0 Radius=0.875
  constraints (2):
    c: Coincident(g0,g-1)
    c: Diameter(g0) = 1.75
FEATURE [PartDesign::Pad] Pad022
  Direction = (0,0,1)
  Length = 20
  Length2 = 10
  Profile = -> Sketch055
  ReferenceAxis = -> Sketch055 [N_Axis]
  Type = 0
FEATURE [PartDesign::Body] Body013  label="Filament"
  Group = -> [Sketch055,Pad022]
  Origin = -> Origin024
  Placement = pos=(-11.6981,-6.70326,18.6) rot=(0,0,1;1.22173rad)
  Tip = -> Pad022
FEATURE [Part::FeaturePython] Screw005  label="M3x10-Screw004"  # Fasteners workbench fastener (typed FeaturePython)
  Placement = pos=(-21.3,0,20.9) rot=(0,0,1;0rad)
  diameter = 1
  invert = false
  leftHanded = false
  length = 2
  lengthCustom = 10
  matchOuter = false
  offset = 0
  thread = false
  type = 42
FEATURE [Sketcher::SketchObject] Sketch056
  AttachmentOffset = pos=(0,0,21) rot=(0,0,1;0rad)
  FullyConstrained = false
  MapMode = 5
  Placement = pos=(0,0,21) rot=(0,0,1;0rad)
  Support = -> [XY_Plane002]
  expr: .AttachmentOffset.Base.z = 17mm + 4mm
  sketch-geometry (8):
    g0: ArcOfCircle CenterX=-22.3614 CenterY=0 CenterZ=0 NormalX=0 NormalY=0 NormalZ=1 AngleXU=0 Radius=4.28262 StartAngle=4.53905 EndAngle=8.18976
    g1: LineSegment StartX=-23.1 StartY=-4.21844 StartZ=0 EndX=-28.0552 EndY=-7.62 EndZ=0
    g2: LineSegment StartX=-23.7725 StartY=4.04345 StartZ=0 EndX=-34.363 EndY=1.22293 EndZ=0
    g3: LineSegment StartX=-28.0552 StartY=-7.62 StartZ=0 EndX=-39.3482 EndY=-7.62 EndZ=0
    g4: LineSegment StartX=-39.3482 StartY=-7.62 StartZ=0 EndX=-39.1891 EndY=-5.07912 EndZ=0
    g5: LineSegment StartX=-39.1891 StartY=-5.07912 StartZ=0 EndX=-34.363 EndY=1.22293 EndZ=0
    g6: Circle CenterX=-22.3614 CenterY=0 CenterZ=0 NormalX=0 NormalY=0 NormalZ=1 AngleXU=0 Radius=3.05
    g7: Circle CenterX=-22.3614 CenterY=0 CenterZ=0 NormalX=0 NormalY=0 NormalZ=1 AngleXU=0 Radius=5.0229
  constraints (12):
    c: PointOnObject(g0,g-1)
    c: Coincident(g1,g0)
    c: Coincident(g2,g0)
    c: Coincident(g3,g1)
    c: DistanceY(g3,g-1) = 7.62
    c: Horizontal(g3)
    c: Coincident(g4,g3)
    c: Coincident(g5,g4)
    c: Coincident(g5,g2)
    c: Coincident(g6,g0)
    c: Coincident(g7,g0)
    c: Diameter(g6) = 6.1
FEATURE [Part::FeaturePython] Nut  label="M3-Nut"  # Fasteners workbench fastener (typed FeaturePython)
  Placement = pos=(-21.3,0,10.4) rot=(0,0,1;0rad)
  diameter = 4
  invert = false
  leftHanded = false
  matchOuter = false
  offset = 0
  thread = false
  type = 9
FEATURE [Part::Feature] Part__Feature061  label="14HR05-0504S (STEP) v1"
  Placement = pos=(-14.0134,-47.1,21.9963) rot=(-0.889126,-0.323616,-0.323616;1.68804rad)
  shape: bbox 39.59 x 24 x 36.5 mm, 29 faces (baked)
FEATURE [Sketcher::SketchObject] Sketch057
  FullyConstrained = true
  MapMode = 5
  Placement = pos=(0,0,0) rot=(1,0,0;1.5708rad)
  Support = -> [XZ_Plane025]
  sketch-geometry (2):
    g0: Circle CenterX=0 CenterY=0 CenterZ=0 NormalX=0 NormalY=0 NormalZ=1 AngleXU=0 Radius=2.5
    g1: Circle CenterX=0 CenterY=0 CenterZ=0 NormalX=0 NormalY=0 NormalZ=1 AngleXU=0 Radius=5.5
  constraints (4):
    c: Coincident(g0,g-1)
    c: Diameter(g0) = 5
    c: Coincident(g1,g0)
    c: Diameter(g1) = 11
FEATURE [PartDesign::Pad] Pad023
  Direction = (0,-1,2e-16)
  Length = 11
  Length2 = 10
  Placement = pos=(0,0,0) rot=(1,0,0;1.5708rad)
  Profile = -> Sketch057
  ReferenceAxis = -> Sketch057 [N_Axis]
  Type = 0
FEATURE [PartDesign::Body] Body014
  Group = -> [Sketch057,Pad023]
  Origin = -> Origin025
  Placement = pos=(0,32.7,0) rot=(0,0,1;0rad)
  Tip = -> Pad023
FEATURE [App::Part] _mm_e3d_hobbed_drive_gear__5mm_ID_v2  label="Drive Gear"
  Group = -> [Part__Feature,Body014]
  Origin = -> Origin001
  Placement = pos=(-17.7086,25.1742,27.784) rot=(0,0,1;3.14159rad)
FEATURE [Sketcher::SketchObject] Sketch058
  AttachmentOffset = pos=(0,0,7.62) rot=(0,0,1;0rad)
  FullyConstrained = false
  MapMode = 5
  Placement = pos=(0,-7.62,-1.7e-15) rot=(1,0,0;1.5708rad)
  Support = -> [XZ_Plane002]
  sketch-geometry (20):
    g0: ArcOfCircle CenterX=-39.2362 CenterY=0.297645 CenterZ=0 NormalX=0 NormalY=0 NormalZ=1 AngleXU=0 Radius=8.97278 StartAngle=2.89527 EndAngle=6.14074
    g1: LineSegment StartX=-41.3063 StartY=28.862 StartZ=0 EndX=-47.9381 EndY=2.48557 EndZ=0
    g2: LineSegment StartX=-30.3543 StartY=-0.976169 StartZ=0 EndX=-27.6367 EndY=17.9726 EndZ=0
    g3: Circle CenterX=-39.2362 CenterY=0.297645 CenterZ=0 NormalX=0 NormalY=0 NormalZ=1 AngleXU=0 Radius=6.05
    g4: Circle CenterX=-17.75 CenterY=27.75 CenterZ=0 NormalX=0 NormalY=0 NormalZ=1 AngleXU=0 Radius=2.56662
    g5: Circle CenterX=-8.40876 CenterY=42.3503 CenterZ=0 NormalX=0 NormalY=0 NormalZ=1 AngleXU=0 Radius=2.032
    g6: Circle CenterX=-11.4193 CenterY=18.5398 CenterZ=0 NormalX=0 NormalY=0 NormalZ=1 AngleXU=0 Radius=2.032
    g7: Circle CenterX=-32.2192 CenterY=45.3608 CenterZ=0 NormalX=0 NormalY=0 NormalZ=1 AngleXU=0 Radius=2.032
    g8: Circle CenterX=-35.2297 CenterY=21.5503 CenterZ=0 NormalX=0 NormalY=0 NormalZ=1 AngleXU=0 Radius=2.032
    g9: LineSegment StartX=-32.2192 StartY=45.3608 StartZ=0 EndX=-8.40876 EndY=42.3503 EndZ=0
    g10: LineSegment StartX=-8.40876 StartY=42.3503 StartZ=0 EndX=-11.4193 EndY=18.5398 EndZ=0
    g11: LineSegment StartX=-11.4193 StartY=18.5398 StartZ=0 EndX=-35.2297 EndY=21.5503 EndZ=0
    g12: LineSegment StartX=-35.2297 StartY=21.5503 StartZ=0 EndX=-32.2192 EndY=45.3608 EndZ=0
    g13: LineSegment StartX=-27.6367 StartY=17.9726 StartZ=0 EndX=-14.5474 EndY=23.3304 EndZ=0
    g14: LineSegment StartX=-17.6166 StartY=33.2063 StartZ=0 EndX=-41.3063 EndY=28.862 EndZ=0
    g15: ArcOfCircle CenterX=-17.75 CenterY=27.75 CenterZ=0 NormalX=0 NormalY=0 NormalZ=1 AngleXU=0 Radius=5.45795 StartAngle=5.33945 EndAngle=7.82954
    g16: LineSegment StartX=-25.7572 StartY=36.4231 StartZ=0 EndX=0.882739 EndY=36.4231 EndZ=0
    g17: LineSegment StartX=0.882739 StartY=36.4231 StartZ=0 EndX=0.882739 EndY=17.1981 EndZ=0
    g18: LineSegment StartX=0.882739 StartY=17.1981 StartZ=0 EndX=-25.7572 EndY=17.1981 EndZ=0
    g19: LineSegment StartX=-25.7572 StartY=17.1981 StartZ=0 EndX=-25.7572 EndY=36.4231 EndZ=0
  constraints (36):
    c: Tangent(g1,g0) = -1.5708
    c: Tangent(g0,g2) = -1.5708
    c: Coincident(g3,g0)
    c: Diameter(g3) = 12.1
    c: Coincident(g9,g7)
    c: Coincident(g9,g5)
    c: Coincident(g10,g5)
    c: Coincident(g10,g6)
    c: Coincident(g10,g11)
    c: Coincident(g11,g8)
    c: Coincident(g11,g12)
    c: Coincident(g12,g7)
    c: Equal(g5,g7)
    c: Equal(g7,g6)
    c: Equal(g6,g8)
    c: Perpendicular(g9,g10)
    c: Perpendicular(g11,g10)
    c: Perpendicular(g9,g12)
    c: Equal(g9,g12)
    c: Distance(g10) = 24
    c: Diameter(g6) = 4.064
    c: Coincident(g13,g2)
    c: Coincident(g14,g1)
    c: Coincident(g15,g4)
    c: Coincident(g15,g14)
    c: Coincident(g15,g13)
    c: DistanceY(g-1,g4) = 27.75
    c: DistanceX(g4,g-1) = 17.75
    c: Coincident(g16,g17)
    c: Coincident(g17,g18)
    c: Coincident(g18,g19)
    c: Coincident(g19,g16)
    c: Horizontal(g16)
    c: Horizontal(g18)
    c: Vertical(g17)
    c: Vertical(g19)
FEATURE [PartDesign::Pocket] Pocket021
  BaseFeature = -> Pocket010
  Direction = (0,1,2e-16)
  Length = 1
  Length2 = 5
  Placement = pos=(0,0,0) rot=(1,0,0;1.5708rad)
  Profile = -> Sketch058
  ReferenceAxis = -> Sketch058 [N_Axis]
  Reversed = true
  Type = 0
FEATURE [Sketcher::SketchObject] Sketch059
  AttachmentOffset = pos=(0,0,46) rot=(0,0,1;0rad)
  FullyConstrained = false
  MapMode = 5
  Placement = pos=(-46,1.02e-14,-1.02e-14) rot=(-0.57735,0.57735,0.57735;4.18879rad)
  Support = -> [YZ_Plane002]
  sketch-geometry (1):
    g0: Circle CenterX=16.0537 CenterY=15.0244 CenterZ=0 NormalX=0 NormalY=0 NormalZ=1 AngleXU=0 Radius=5
  constraints (1):
    c: Diameter(g0) = 10
FEATURE [PartDesign::Pocket] Pocket022
  BaseFeature = -> Pocket021
  Direction = (1,-2e-16,3e-16)
  Length = 3
  Length2 = 5
  Placement = pos=(0,0,0) rot=(1,0,0;1.5708rad)
  Profile = -> Sketch059
  ReferenceAxis = -> Sketch059 [N_Axis]
  Type = 0
FEATURE [PartDesign::Body] Body001  label="Lever"
  Group = -> [Sketch003,Pad001,Sketch028,Pad011,Sketch029,Sketch032,Pocket007,Sketch033,Pocket008,Sketch034,Pad012,Pocket009,Sketch035,Pocket010,Sketch056,Sketch058,Pocket021,Sketch059,Pocket022]
  Origin = -> Origin002
  Tip = -> Pocket022
FEATURE [App::Part] Part006  label="LeverGroup"
  Group = -> [Nut,Screw005,Part__Feature056,bearing_623_2_1,_mm_e3d_hobbed_drive_gear__5mm_ID_v2,Body001]
  Origin = -> Origin026
  Placement = pos=(-0.118878,0,2.26519) rot=(0,1,0;6.23083rad)
FEATURE [Sketcher::SketchObject] Sketch062
  FullyConstrained = false
  MapMode = 5
  Support = -> [XY_Plane011]
  sketch-geometry (4):
    g0: LineSegment StartX=-61.0267 StartY=0 StartZ=0 EndX=-63.4441 EndY=-23 EndZ=0
    g1: LineSegment StartX=-52.9704 StartY=0 StartZ=0 EndX=-52.9704 EndY=-23 EndZ=0
    g2: LineSegment StartX=-52.9704 StartY=-23 StartZ=0 EndX=-63.4441 EndY=-23 EndZ=0
    g3: LineSegment StartX=-61.0267 StartY=0 StartZ=0 EndX=-52.9704 EndY=0 EndZ=0
  constraints (10):
    c: Vertical(g1)
    c: Coincident(g2,g1)
    c: Coincident(g2,g0)
    c: Horizontal(g2)
    c: DistanceY(g1,g-1) = 23
    c: PointOnObject(g0,g-1)
    c: Angle(g0,g-1) = 1.67552
    c: Coincident(g3,g0)
    c: Coincident(g3,g1)
    c: Horizontal(g3)
FEATURE [PartDesign::Chamfer] Chamfer004
  Angle = 55
  Base = -> PolarPattern002 [Edge49,Edge78,Edge60,Edge66,Edge72]
  BaseFeature = -> PolarPattern002
  ChamferType = 2
  FlipDirection = false
  Size = 1.4
  Size2 = 1
  SupportTransform = false
  UseAllEdges = false
FEATURE [PartDesign::Chamfer] Chamfer005
  Angle = 55
  Base = -> Chamfer004 [Edge17,Edge19]
  BaseFeature = -> Chamfer004
  ChamferType = 2
  FlipDirection = false
  Size = 1.4
  Size2 = 1
  SupportTransform = false
  UseAllEdges = false
FEATURE [PartDesign::Body] Body003  label="SelectorBumps"
  Group = -> [Sketch006,Pad004,Sketch007,Pocket001,PolarPattern002,Chamfer004,Chamfer005]
  Origin = -> Origin007
  Tip = -> Chamfer005
FEATURE [PartDesign::Pad] Pad024
  BaseFeature = -> Pocket020
  Direction = (0,0,1)
  Length = 44
  Length2 = 10
  Profile = -> Sketch062
  ReferenceAxis = -> Sketch062 [N_Axis]
  Type = 0
FEATURE [Sketcher::SketchObject] Sketch063
  AttachmentOffset = pos=(-15,0,-52) rot=(0,0,1;0rad)
  FullyConstrained = true
  MapMode = 5
  Placement = pos=(-52,-15,-8.2e-15) rot=(0.57735,0.57735,0.57735;2.0944rad)
  Support = -> [YZ_Plane011]
  sketch-geometry (1):
    g0: Circle CenterX=0 CenterY=36 CenterZ=0 NormalX=0 NormalY=0 NormalZ=1 AngleXU=0 Radius=5.5
  constraints (3):
    c: PointOnObject(g0,g-2)
    c: DistanceY(g-1,g0) = 36
    c: Diameter(g0) = 11
FEATURE [PartDesign::Pocket] Pocket023
  BaseFeature = -> Pad024
  Direction = (-1,2e-16,-3e-16)
  Length = 3
  Length2 = 5
  Profile = -> Sketch063
  ReferenceAxis = -> Sketch063 [N_Axis]
  Type = 0
FEATURE [Sketcher::SketchObject] Sketch064
  AttachmentOffset = pos=(0,0,-25) rot=(0,0,1;1.5708rad)
  FullyConstrained = true
  MapMode = 5
  Placement = pos=(0,0,-25) rot=(0,0,1;1.5708rad)
  Support = -> [XY_Plane]
  expr: Constraints[2] = Spreadsheet.FilamentBottomPathOffset
  sketch-geometry (1):
    g0: Circle CenterX=-10.16 CenterY=0 CenterZ=0 NormalX=0 NormalY=0 NormalZ=1 AngleXU=0 Radius=1.5
  constraints (3):
    c: PointOnObject(g0,g-1)
    c: Diameter(g0) = 3
    c: DistanceX(g0,g-1) = 10.16
FEATURE [Sketcher::SketchObject] Sketch065
  AttachmentOffset = pos=(0,0,32) rot=(0,0,1;1.5708rad)
  FullyConstrained = true
  MapMode = 5
  Placement = pos=(0,0,32) rot=(0,0,1;1.5708rad)
  Support = -> [XY_Plane]
  expr: Constraints[2] = Spreadsheet.FilamentTopPathOffset
  sketch-geometry (1):
    g0: Circle CenterX=-13.208 CenterY=0 CenterZ=0 NormalX=0 NormalY=0 NormalZ=1 AngleXU=0 Radius=1.5
  constraints (3):
    c: PointOnObject(g0,g-1)
    c: Diameter(g0) = 3
    c: DistanceX(g0,g-1) = 13.208
FEATURE [Sketcher::SketchObject] Sketch066
  AttachmentOffset = pos=(0,0,25) rot=(0,0,1;1.5708rad)
  FullyConstrained = true
  MapMode = 5
  Placement = pos=(0,0,25) rot=(0,0,1;1.5708rad)
  Support = -> [XY_Plane]
  expr: Constraints[2] = Spreadsheet.FilamentTopPathOffset
  sketch-geometry (1):
    g0: Circle CenterX=-13.208 CenterY=0 CenterZ=0 NormalX=0 NormalY=0 NormalZ=1 AngleXU=0 Radius=1.5
  constraints (3):
    c: PointOnObject(g0,g-1)
    c: Diameter(g0) = 3
    c: DistanceX(g0,g-1) = 13.208
FEATURE [Sketcher::SketchObject] Sketch067
  FullyConstrained = false
  MapMode = 5
  Placement = pos=(0,0,0) rot=(0.57735,0.57735,0.57735;2.0944rad)
  Support = -> [YZ_Plane]
  sketch-geometry (14):
    g0: LineSegment StartX=-11.67 StartY=39.2588 StartZ=0 EndX=-11.67 EndY=35.19 EndZ=0
    g1-g5: Circle x5 (B-spline internal-alignment scaffolding for g6; pole/knot coordinates omitted)
    g6: BSplineCurve PolesCount=5 KnotsCount=3 Degree=3 IsPeriodic=0
    g7: GeomPoint X=-11.67 Y=35.19 Z=0
    g8: GeomPoint X=-10.7578 Y=21.2778 Z=0
    g9: GeomPoint X=-8.66 Y=-10.5318 Z=0
    g10: LineSegment StartX=-8.66 StartY=-10.5318 StartZ=0 EndX=-8.66 EndY=-30.3032 EndZ=0
    g11: LineSegment StartX=-8.66 StartY=-30.3032 StartZ=0 EndX=-11.66 EndY=-30.3032 EndZ=0
    g12: GeomPoint X=-10.16 Y=-30.3032 Z=0
    g13: LineSegment StartX=-8.75045 StartY=11.377 StartZ=0 EndX=-11.7504 EndY=11.377 EndZ=0
  constraints (19):
    c: Vertical(g0)
    c: DistanceX(g0,g-1) = 11.67
    c: Weight(g1) = 1
    c: Coincident(g6,g0)
    c: Equal(g1, g2-g5) x4
    c: InternalAlignment(g1-g5 -> g6) x5
    c: InternalAlignment(g7,g6)
    c: InternalAlignment(g8,g6)
    c: InternalAlignment(g9,g6)
    c: Coincident(g10,g6)
    c: Vertical(g10)
    c: Horizontal(g11)
    c: DistanceX(g11,g11) = 3
    c: PointOnObject(g12,g11)
    c: DistanceX(g12,g-1) = 10.16
    c: Coincident(g11,g10)
    c: DistanceX(g12,g10) = 1.5
    c: Horizontal(g13)
    c: DistanceX(g13,g13) = 3
FEATURE [PartDesign::Pad] Pad025
  BaseFeature = -> PolarPattern004
  Direction = (0,0,1)
  Length = 28
  Length2 = 10
  Profile = -> Sketch025
  ReferenceAxis = -> Sketch025 [N_Axis]
  Reversed = true
  Type = 0
FEATURE [PartDesign::SubtractivePipe] SubtractivePipe
  AuxilleryCurvelinear = true
  AuxillerySpineTangent = false
  BaseFeature = -> Pad025
  Binormal = (0,0,0)
  Mode = 0
  Profile = -> Sketch019
  Spine = -> Sketch067
  SpineTangent = false
  Transformation = 0
  Transition = 0
FEATURE [PartDesign::PolarPattern] PolarPattern005
  Angle = 360
  Axis = -> Sketch019 [N_Axis]
  BaseFeature = -> SubtractivePipe
  Occurrences = 6
  Originals = -> [SubtractivePipe]
FEATURE [PartDesign::Pad] Pad026
  BaseFeature = -> PolarPattern005
  Direction = (0,0,1)
  Length = 5
  Length2 = 10
  Profile = -> Sketch040
  ReferenceAxis = -> Sketch040 [N_Axis]
  Type = 0
FEATURE [PartDesign::Body] Body  label="Chambers"
  Group = -> [Sketch,Pad,Sketch001,Groove,Sketch002,Pocket,PolarPattern,Sketch008,Pocket002,Sketch014,Pocket003,PolarPattern004,Sketch019,Sketch020,Sketch021,Sketch022,Sketch025,Sketch040,Sketch064,Sketch065,Sketch066,Sketch067,Pad025,SubtractivePipe,PolarPattern005,Pad026]
  Origin = -> Origin
  Tip = -> Pad026
FEATURE [Sketcher::SketchObject] Sketch068
  FullyConstrained = true
  MapMode = 5
  Support = -> [XY_Plane027]
  sketch-geometry (1):
    g0: Circle CenterX=-12.954 CenterY=0 CenterZ=0 NormalX=0 NormalY=0 NormalZ=1 AngleXU=0 Radius=12.954
  constraints (3):
    c: PointOnObject(g0,g-1)
    c: Radius(g0) = 12.954
    c: PointOnObject(g-1,g0)
FEATURE [PartDesign::Pad] Pad027
  Direction = (1,1,1)
  Length = 203.2
  Length2 = 99.9998
  Midplane = true
  Profile = -> Sketch068
  Type = 0
FEATURE [PartDesign::Body] Body015  label="BarExample"
  Group = -> [Sketch068,Pad027]
  Origin = -> Origin027
  Placement = pos=(55.26,46.6,0) rot=(0,0,1;0rad)
  Tip = -> Pad027
FEATURE [Sketcher::SketchObject] Sketch069
  FullyConstrained = true
  MapMode = 5
  Support = -> [XY_Plane028]
  sketch-geometry (11):
    g0: Circle CenterX=-15.24 CenterY=0 CenterZ=0 NormalX=0 NormalY=0 NormalZ=1 AngleXU=0 Radius=13.081
    g1: ArcOfCircle CenterX=-15.24 CenterY=0 CenterZ=0 NormalX=0 NormalY=0 NormalZ=1 AngleXU=0 Radius=13.081 StartAngle=1.66804 EndAngle=4.61515
    g2: LineSegment StartX=-16.51 StartY=13.0192 StartZ=0 EndX=-16.51 EndY=20.6392 EndZ=0
    g3: LineSegment StartX=-16.51 StartY=20.6392 StartZ=0 EndX=-20.32 EndY=20.6392 EndZ=0
    g4: LineSegment StartX=-20.32 StartY=20.6392 StartZ=0 EndX=-20.32 EndY=16.109 EndZ=0
    g5: LineSegment StartX=-16.51 StartY=-13.0192 StartZ=0 EndX=-16.51 EndY=-20.6392 EndZ=0
    g6: LineSegment StartX=-16.51 StartY=-20.6392 StartZ=0 EndX=-20.32 EndY=-20.6392 EndZ=0
    g7: LineSegment StartX=-20.32 StartY=-20.6392 StartZ=0 EndX=-20.32 EndY=-16.109 EndZ=0
    g8: ArcOfCircle CenterX=-15.24 CenterY=0 CenterZ=0 NormalX=0 NormalY=0 NormalZ=1 AngleXU=0 Radius=16.891 StartAngle=1.87628 EndAngle=4.40691
    g9: GeomPoint X=-32.131 Y=0 Z=0
    g10: GeomPoint X=-28.321 Y=0 Z=0
  constraints (31):
    c: PointOnObject(g0,g-1)
    c: Diameter(g0) = 26.162
    c: Coincident(g1,g0)
    c: PointOnObject(g1,g0)
    c: DistanceX(g1,g1) = 1.27
    c: Vertical(g1,g1)
    c: Coincident(g2,g1)
    c: Vertical(g2)
    c: Coincident(g3,g2)
    c: Horizontal(g3)
    c: Coincident(g4,g3)
    c: Vertical(g4)
    c: Coincident(g5,g1)
    c: Vertical(g5)
    c: Coincident(g6,g5)
    c: Horizontal(g6)
    c: Coincident(g7,g6)
    c: Vertical(g7)
    c: Coincident(g8,g1)
    c: Coincident(g8,g4)
    c: Coincident(g8,g7)
    c: Equal(g5,g2)
    c: Equal(g4,g7)
    c: PointOnObject(g9,g8)
    c: PointOnObject(g10,g1)
    c: Horizontal(g10,g9)
    c: PointOnObject(g9,g-1)
    c: DistanceX(g9,g10) = 3.81
    c: DistanceX(g1,g-1) = 15.24
    c: DistanceX(g6,g6) = 3.81
    c: DistanceY(g5,g5) = 7.62
FEATURE [PartDesign::Pad] Pad028
  Direction = (1,1,1)
  Length = 63.5
  Length2 = 99.9998
  Profile = -> Sketch069
  Type = 0
FEATURE [Sketcher::SketchObject] Sketch070
  AttachmentOffset = pos=(0,0,15.24) rot=(0,0,1;0rad)
  FullyConstrained = true
  MapMode = 5
  Placement = pos=(-15.24,3.4e-15,-3.4e-15) rot=(-0.57735,0.57735,0.57735;4.18879rad)
  Support = -> [YZ_Plane028]
  expr: Constraints[17] = 3.1mm
  sketch-geometry (14):
    g0: Circle CenterX=-17.145 CenterY=7.62 CenterZ=0 NormalX=0 NormalY=0 NormalZ=1 AngleXU=0 Radius=1.55
    g1: Circle CenterX=17.145 CenterY=7.62 CenterZ=0 NormalX=0 NormalY=0 NormalZ=1 AngleXU=0 Radius=1.55
    g2: Circle CenterX=17.145 CenterY=33.02 CenterZ=0 NormalX=0 NormalY=0 NormalZ=1 AngleXU=0 Radius=1.55
    g3: Circle CenterX=17.145 CenterY=58.42 CenterZ=0 NormalX=0 NormalY=0 NormalZ=1 AngleXU=0 Radius=1.55
    g4: Circle CenterX=-17.145 CenterY=58.42 CenterZ=0 NormalX=0 NormalY=0 NormalZ=1 AngleXU=0 Radius=1.55
    g5: Circle CenterX=-17.145 CenterY=33.02 CenterZ=0 NormalX=0 NormalY=0 NormalZ=1 AngleXU=0 Radius=1.55
    g6: LineSegment StartX=-17.145 StartY=33.02 StartZ=0 EndX=-17.145 EndY=58.42 EndZ=0
    g7: LineSegment StartX=-17.145 StartY=33.02 StartZ=0 EndX=-17.145 EndY=7.62 EndZ=0
    g8: Circle CenterX=-17.145 CenterY=20.32 CenterZ=0 NormalX=0 NormalY=0 NormalZ=1 AngleXU=0 Radius=1.55
    g9: Circle CenterX=17.145 CenterY=20.32 CenterZ=0 NormalX=0 NormalY=0 NormalZ=1 AngleXU=0 Radius=1.55
    g10: Circle CenterX=17.145 CenterY=45.72 CenterZ=0 NormalX=0 NormalY=0 NormalZ=1 AngleXU=0 Radius=1.55
    g11: Circle CenterX=-17.145 CenterY=45.72 CenterZ=0 NormalX=0 NormalY=0 NormalZ=1 AngleXU=0 Radius=1.55
    g12: LineSegment StartX=17.145 StartY=45.72 StartZ=0 EndX=17.145 EndY=33.02 EndZ=0
    g13: LineSegment StartX=17.145 StartY=20.32 StartZ=0 EndX=17.145 EndY=33.02 EndZ=0
  constraints (37):
    c: Horizontal(g0,g1)
    c: Horizontal(g4,g3)
    c: Vertical(g3,g2)
    c: Vertical(g2,g1)
    c: Vertical(g0,g5)
    c: Vertical(g5,g4)
    c: Equal(g5,g4)
    c: Equal(g4,g3)
    c: Equal(g3,g2)
    c: Equal(g2,g1)
    c: Equal(g1,g0)
    c: Symmetric(g5,g2,g-2)
    c: Coincident(g6,g5)
    c: Coincident(g6,g4)
    c: Coincident(g7,g5)
    c: Coincident(g7,g0)
    c: Equal(g7,g6)
    c: Diameter(g5) = 3.1
    c: DistanceY(g-1,g5) = 33.02
    c: DistanceX(g0,g1) = 34.29
    c: DistanceY(g7,g7) = 25.4
    c: PointOnObject(g8,g7)
    c: PointOnObject(g11,g6)
    c: Equal(g11,g10)
    c: Equal(g10,g9)
    c: Equal(g9,g8)
    c: Equal(g8,g2)
    c: Horizontal(g11,g10)
    c: Horizontal(g9,g8)
    c: Vertical(g9,g2)
    c: Vertical(g2,g10)
    c: Coincident(g12,g10)
    c: Coincident(g12,g2)
    c: Coincident(g13,g9)
    c: Coincident(g13,g2)
    c: Equal(g12,g13)
    c: DistanceY(g13,g13) = 12.7
FEATURE [PartDesign::Pocket] Pocket024
  BaseFeature = -> Pad028
  Direction = (1,1,1)
  Length = 5.0038
  Length2 = 99.9998
  Profile = -> Sketch070
  Reversed = true
  Type = 1
FEATURE [Sketcher::SketchObject] Sketch071
  AttachmentOffset = pos=(0,0,20.32) rot=(0,0,1;0rad)
  FullyConstrained = true
  MapMode = 5
  Placement = pos=(-20.32,4.5e-15,-4.5e-15) rot=(-0.57735,0.57735,0.57735;4.18879rad)
  Support = -> [YZ_Plane028]
  expr: Constraints[17] = 5.2mm
  sketch-geometry (14):
    g0: Circle CenterX=-17.145 CenterY=7.62 CenterZ=0 NormalX=0 NormalY=0 NormalZ=1 AngleXU=0 Radius=2.6
    g1: Circle CenterX=17.145 CenterY=7.62 CenterZ=0 NormalX=0 NormalY=0 NormalZ=1 AngleXU=0 Radius=2.6
    g2: Circle CenterX=17.145 CenterY=33.02 CenterZ=0 NormalX=0 NormalY=0 NormalZ=1 AngleXU=0 Radius=2.6
    g3: Circle CenterX=17.145 CenterY=58.42 CenterZ=0 NormalX=0 NormalY=0 NormalZ=1 AngleXU=0 Radius=2.6
    g4: Circle CenterX=-17.145 CenterY=58.42 CenterZ=0 NormalX=0 NormalY=0 NormalZ=1 AngleXU=0 Radius=2.6
    g5: Circle CenterX=-17.145 CenterY=33.02 CenterZ=0 NormalX=0 NormalY=0 NormalZ=1 AngleXU=0 Radius=2.6
    g6: LineSegment StartX=-17.145 StartY=33.02 StartZ=0 EndX=-17.145 EndY=58.42 EndZ=0
    g7: LineSegment StartX=-17.145 StartY=33.02 StartZ=0 EndX=-17.145 EndY=7.62 EndZ=0
    g8: Circle CenterX=-17.145 CenterY=20.32 CenterZ=0 NormalX=0 NormalY=0 NormalZ=1 AngleXU=0 Radius=2.6
    g9: Circle CenterX=17.145 CenterY=20.32 CenterZ=0 NormalX=0 NormalY=0 NormalZ=1 AngleXU=0 Radius=2.6
    g10: Circle CenterX=17.145 CenterY=45.72 CenterZ=0 NormalX=0 NormalY=0 NormalZ=1 AngleXU=0 Radius=2.6
    g11: Circle CenterX=-17.145 CenterY=45.72 CenterZ=0 NormalX=0 NormalY=0 NormalZ=1 AngleXU=0 Radius=2.6
    g12: LineSegment StartX=17.145 StartY=45.72 StartZ=0 EndX=17.145 EndY=33.02 EndZ=0
    g13: LineSegment StartX=17.145 StartY=20.32 StartZ=0 EndX=17.145 EndY=33.02 EndZ=0
  constraints (37):
    c: Horizontal(g0,g1)
    c: Horizontal(g4,g3)
    c: Vertical(g3,g2)
    c: Vertical(g2,g1)
    c: Vertical(g0,g5)
    c: Vertical(g5,g4)
    c: Equal(g5,g4)
    c: Equal(g4,g3)
    c: Equal(g3,g2)
    c: Equal(g2,g1)
    c: Equal(g1,g0)
    c: Symmetric(g5,g2,g-2)
    c: Coincident(g6,g5)
    c: Coincident(g6,g4)
    c: Coincident(g7,g5)
    c: Coincident(g7,g0)
    c: Equal(g7,g6)
    c: Diameter(g5) = 5.2
    c: DistanceY(g-1,g5) = 33.02
    c: DistanceX(g0,g1) = 34.29
    c: DistanceY(g7,g7) = 25.4
    c: PointOnObject(g8,g7)
    c: PointOnObject(g11,g6)
    c: Equal(g11,g10)
    c: Equal(g10,g9)
    c: Equal(g9,g8)
    c: Equal(g8,g2)
    c: Horizontal(g11,g10)
    c: Horizontal(g9,g8)
    c: Vertical(g9,g2)
    c: Vertical(g2,g10)
    c: Coincident(g12,g10)
    c: Coincident(g12,g2)
    c: Coincident(g13,g9)
    c: Coincident(g13,g2)
    c: Equal(g12,g13)
    c: DistanceY(g13,g13) = 12.7
FEATURE [PartDesign::Pocket] Pocket025
  BaseFeature = -> Pocket024
  Direction = (1,1,1)
  Length = 5.0038
  Length2 = 99.9998
  Profile = -> Sketch071
  Reversed = true
  Type = 1
FEATURE [PartDesign::Fillet] Fillet002
  Base = -> Pocket025 [Edge95,Edge96,Edge98,Edge99,Edge101,Edge102,Edge104,Edge105,Edge107,Edge108,Edge89,Edge90,Edge91,Edge92,Edge93]
  BaseFeature = -> Pocket025
  Radius = 1.27
  SupportTransform = false
  UseAllEdges = false
FEATURE [PartDesign::Body] Body005  label="BarClamp2"
  Group = -> [Sketch069,Pad028,Sketch070,Pocket024,Sketch071,Pocket025,Fillet002]
  Origin = -> Origin028
  Placement = pos=(27.2,46.6,-38.1) rot=(0,0,1;3.14159rad)
  Tip = -> Fillet002
FEATURE [Sketcher::SketchObject] Sketch072
  FullyConstrained = true
  MapMode = 5
  Support = -> [XY_Plane029]
  sketch-geometry (6):
    g0: ArcOfCircle CenterX=-15.24 CenterY=0 CenterZ=0 NormalX=0 NormalY=0 NormalZ=1 AngleXU=0 Radius=12.827 StartAngle=4.71239 EndAngle=7.85398
    g1: LineSegment StartX=-15.24 StartY=12.827 StartZ=0 EndX=-15.24 EndY=20.827 EndZ=0
    g2: LineSegment StartX=-15.24 StartY=-12.827 StartZ=0 EndX=-15.24 EndY=-20.827 EndZ=0
    g3: LineSegment StartX=-15.24 StartY=-20.827 StartZ=0 EndX=0 EndY=-18.0086 EndZ=0
    g4: LineSegment StartX=-15.24 StartY=20.827 StartZ=0 EndX=0 EndY=18.0086 EndZ=0
    g5: LineSegment StartX=0 StartY=18.0086 StartZ=0 EndX=0 EndY=-18.0086 EndZ=0
  constraints (18):
    c: PointOnObject(g0,g-1)
    c: Diameter(g0) = 25.654
    c: Vertical(g0,g0)
    c: Vertical(g0,g0)
    c: Coincident(g1,g0)
    c: Vertical(g1)
    c: Coincident(g2,g0)
    c: Vertical(g2)
    c: Coincident(g3,g2)
    c: PointOnObject(g3,g-2)
    c: Coincident(g4,g1)
    c: DistanceY(g3,g4) = 36.0172
    c: Symmetric(g3,g4,g-1)
    c: Coincident(g5,g4)
    c: Coincident(g5,g3)
    c: Equal(g1,g2)
    c: DistanceX(g0,g-1) = 15.24
    c: DistanceY(g2,g2) = 8
FEATURE [PartDesign::Pad] Pad029
  Direction = (0,0,1)
  Length = 63.5
  Length2 = 99.9998
  Profile = -> Sketch072
  Type = 0
FEATURE [Sketcher::SketchObject] Sketch073
  AttachmentOffset = pos=(0,0,15.24) rot=(0,0,1;0rad)
  FullyConstrained = true
  MapMode = 5
  Placement = pos=(-15.24,3.4e-15,-3.4e-15) rot=(-0.57735,0.57735,0.57735;4.18879rad)
  Support = -> [YZ_Plane029]
  expr: Constraints[17] = 4mm
  sketch-geometry (14):
    g0: Circle CenterX=-17.145 CenterY=7.62 CenterZ=0 NormalX=0 NormalY=0 NormalZ=1 AngleXU=0 Radius=2
    g1: Circle CenterX=17.145 CenterY=7.62 CenterZ=0 NormalX=0 NormalY=0 NormalZ=1 AngleXU=0 Radius=2
    g2: Circle CenterX=17.145 CenterY=33.02 CenterZ=0 NormalX=0 NormalY=0 NormalZ=1 AngleXU=0 Radius=2
    g3: Circle CenterX=17.145 CenterY=58.42 CenterZ=0 NormalX=0 NormalY=0 NormalZ=1 AngleXU=0 Radius=2
    g4: Circle CenterX=-17.145 CenterY=58.42 CenterZ=0 NormalX=0 NormalY=0 NormalZ=1 AngleXU=0 Radius=2
    g5: Circle CenterX=-17.145 CenterY=33.02 CenterZ=0 NormalX=0 NormalY=0 NormalZ=1 AngleXU=0 Radius=2
    g6: LineSegment StartX=-17.145 StartY=33.02 StartZ=0 EndX=-17.145 EndY=58.42 EndZ=0
    g7: LineSegment StartX=-17.145 StartY=33.02 StartZ=0 EndX=-17.145 EndY=7.62 EndZ=0
    g8: Circle CenterX=-17.145 CenterY=20.32 CenterZ=0 NormalX=0 NormalY=0 NormalZ=1 AngleXU=0 Radius=2
    g9: Circle CenterX=17.145 CenterY=20.32 CenterZ=0 NormalX=0 NormalY=0 NormalZ=1 AngleXU=0 Radius=2
    g10: Circle CenterX=17.145 CenterY=45.72 CenterZ=0 NormalX=0 NormalY=0 NormalZ=1 AngleXU=0 Radius=2
    g11: Circle CenterX=-17.145 CenterY=45.72 CenterZ=0 NormalX=0 NormalY=0 NormalZ=1 AngleXU=0 Radius=2
    g12: LineSegment StartX=17.145 StartY=45.72 StartZ=0 EndX=17.145 EndY=33.02 EndZ=0
    g13: LineSegment StartX=17.145 StartY=20.32 StartZ=0 EndX=17.145 EndY=33.02 EndZ=0
  constraints (37):
    c: Horizontal(g0,g1)
    c: Horizontal(g4,g3)
    c: Vertical(g3,g2)
    c: Vertical(g2,g1)
    c: Vertical(g0,g5)
    c: Vertical(g5,g4)
    c: Equal(g5,g4)
    c: Equal(g4,g3)
    c: Equal(g3,g2)
    c: Equal(g2,g1)
    c: Equal(g1,g0)
    c: Symmetric(g5,g2,g-2)
    c: Coincident(g6,g5)
    c: Coincident(g6,g4)
    c: Coincident(g7,g5)
    c: Coincident(g7,g0)
    c: Equal(g7,g6)
    c: Diameter(g5) = 4
    c: DistanceY(g-1,g5) = 33.02
    c: DistanceX(g0,g1) = 34.29
    c: DistanceY(g7,g7) = 25.4
    c: PointOnObject(g8,g7)
    c: PointOnObject(g11,g6)
    c: Equal(g11,g10)
    c: Equal(g10,g9)
    c: Equal(g9,g8)
    c: Equal(g8,g2)
    c: Horizontal(g11,g10)
    c: Horizontal(g9,g8)
    c: Vertical(g9,g2)
    c: Vertical(g2,g10)
    c: Coincident(g12,g10)
    c: Coincident(g12,g2)
    c: Coincident(g13,g9)
    c: Coincident(g13,g2)
    c: Equal(g12,g13)
    c: DistanceY(g13,g13) = 12.7
FEATURE [PartDesign::Pocket] Pocket026
  BaseFeature = -> Pad029
  Direction = (1,-2e-16,3e-16)
  Length = 7.62
  Length2 = 99.9998
  Profile = -> Sketch073
  Type = 0
FEATURE [PartDesign::Body] Body016  label="BarClamp"
  Group = -> [Sketch072,Pad029,Sketch073,Pocket026]
  Origin = -> Origin029
  Placement = pos=(27.3799,20.3008,-21.7) rot=(0,0,1;3.66519rad)
  Tip = -> Pocket026
FEATURE [Sketcher::SketchObject] Sketch074
  FullyConstrained = false
  MapMode = 5
  Placement = pos=(0,0,0) rot=(0,1,0;3.14159rad)
  Support = -> [XY_Plane021]
  sketch-geometry (7):
    g0: ArcOfCircle CenterX=0 CenterY=0 CenterZ=0 NormalX=0 NormalY=0 NormalZ=1 AngleXU=0 Radius=21.9404 StartAngle=1.19577 EndAngle=2.14643
    g1: LineSegment StartX=8.0367 StartY=20.4156 StartZ=0 EndX=12.75 EndY=0 EndZ=0
    g2: ArcOfCircle CenterX=0 CenterY=0 CenterZ=0 NormalX=0 NormalY=0 NormalZ=1 AngleXU=0 Radius=32.4633 StartAngle=1.40499 EndAngle=2.12098
    g3: LineSegment StartX=5.35804 StartY=32.0181 StartZ=0 EndX=8.0367 EndY=20.4156 EndZ=0
    g4: LineSegment StartX=-16.9731 StartY=27.6727 StartZ=0 EndX=-11.9437 EndY=18.4047 EndZ=0
    g5: Circle CenterX=-12.2657 CenterY=25.6173 CenterZ=0 NormalX=0 NormalY=0 NormalZ=1 AngleXU=0 Radius=5.5
    g6: Circle CenterX=2.47211 CenterY=28.4094 CenterZ=0 NormalX=0 NormalY=0 NormalZ=1 AngleXU=0 Radius=5.5
  constraints (14):
    c: Coincident(g0,g-1)
    c: Coincident(g1,g0)
    c: PointOnObject(g1,g-1)
    c: Angle(g1,g-1) = 1.3439
    c: Coincident(g2,g0)
    c: Coincident(g3,g2)
    c: Coincident(g3,g0)
    c: Coincident(g4,g2)
    c: Coincident(g4,g0)
    c: Equal(g6,g5)
    c: Diameter(g5) = 11
    c: Distance(g5,g6) = 15
    c: Parallel(g3,g1)
    c: DistanceX(g0,g1) = 12.75
FEATURE [PartDesign::Pocket] Pocket027
  BaseFeature = -> Pad021
  Direction = (0,0,1)
  Length = 5
  Length2 = 5
  Profile = -> Sketch074
  ReferenceAxis = -> Sketch074 [N_Axis]
  Reversed = true
  Type = 1
FEATURE [PartDesign::Chamfer] Chamfer007
  Angle = 80
  Base = -> Pocket027 [Edge8]
  BaseFeature = -> Pocket027
  ChamferType = 2
  FlipDirection = false
  Size = 0.8
  Size2 = 1
  SupportTransform = false
  UseAllEdges = false
FEATURE [Sketcher::SketchObject] Sketch075
  AttachmentOffset = pos=(0,0,2) rot=(0,0,1;0rad)
  FullyConstrained = false
  MapMode = 5
  Placement = pos=(0,0,-2) rot=(0,1,0;3.14159rad)
  Support = -> [XY_Plane021]
  sketch-geometry (9):
    g0: Circle CenterX=8.83346 CenterY=-5.1 CenterZ=0 NormalX=0 NormalY=0 NormalZ=1 AngleXU=0 Radius=1
    g1: LineSegment StartX=0 StartY=0 StartZ=0 EndX=8.83346 EndY=-5.1 EndZ=0
    g2: LineSegment StartX=5.06782 StartY=-8.31285 StartZ=0 EndX=13.998 EndY=-17.2547 EndZ=0
    g3: LineSegment StartX=20.9442 StartY=-10.3175 StartZ=0 EndX=12.8648 EndY=-2.22757 EndZ=0
    g4: ArcOfCircle CenterX=17.4711 CenterY=-13.7861 CenterZ=0 NormalX=0 NormalY=0 NormalZ=1 AngleXU=0 Radius=4.90851 StartAngle=3.92634 EndAngle=7.06793
    g5: LineSegment StartX=5.06782 StartY=-8.31285 StartZ=0 EndX=8.83346 EndY=-5.1 EndZ=0
    g6: LineSegment StartX=8.83346 StartY=-5.1 StartZ=0 EndX=12.8648 EndY=-2.22757 EndZ=0
    g7: Circle CenterX=17.7692 CenterY=-14.2059 CenterZ=0 NormalX=0 NormalY=0 NormalZ=1 AngleXU=0 Radius=2.25
    g8: ArcOfCircle CenterX=8.83346 CenterY=-5.1 CenterZ=0 NormalX=0 NormalY=0 NormalZ=1 AngleXU=0 Radius=4.95 StartAngle=3.84794 EndAngle=6.90227
  constraints (19):
    c: Diameter(g0) = 2
    c: Distance(g-1,g0) = 10.2
    c: Coincident(g1,g-1)
    c: Coincident(g1,g0)
    c: Angle(g1,g-1) = 0.523599
    c: PointOnObject(g4,g3)
    c: Coincident(g6,g3) = -1.5708
    c: Parallel(g3,g2)
    c: Tangent(g4,g2) = -1.5708
    c: Tangent(g3,g4) = -1.5708
    c: Diameter(g7) = 4.5
    c: Coincident(g8,g3)
    c: Coincident(g2,g5)
    c: Coincident(g2,g8)
    c: Diameter(g8) = 9.9
    c: Coincident(g0,g5)
    c: Coincident(g0,g6)
    c: Coincident(g0,g8)
    c: Angle(g5,g6) = 3.05433
FEATURE [PartDesign::Pad] Pad030
  BaseFeature = -> Chamfer007
  Direction = (0,0,-1)
  Length = 4
  Length2 = 10
  Profile = -> Sketch075
  ReferenceAxis = -> Sketch075 [N_Axis]
  Type = 0
FEATURE [PartDesign::Chamfer] Chamfer008
  Angle = 30
  Base = -> Pad030 [Edge21]
  BaseFeature = -> Pad030
  ChamferType = 2
  FlipDirection = false
  Size = 2.8
  Size2 = 1
  SupportTransform = false
  UseAllEdges = false
FEATURE [PartDesign::Chamfer] Chamfer009
  Angle = 60
  Base = -> Chamfer008 [Edge33]
  BaseFeature = -> Chamfer008
  ChamferType = 2
  FlipDirection = false
  Size = 1
  Size2 = 1
  SupportTransform = false
  UseAllEdges = false
FEATURE [PartDesign::Body] Body011  label="OldFunnel"
  Group = -> [Sketch044,Pad018,Sketch045,Pocket016,Sketch050,Pad020,Sketch051,Sketch052,Sketch053,AdditiveLoft,Pad021,Sketch074,Pocket027,Chamfer007,Sketch075,Pad030,Chamfer008,Chamfer009]
  Origin = -> Origin021
  Placement = pos=(0,0,0) rot=(0,0,1;0.017453rad)
  Tip = -> Chamfer009
FEATURE [Part::FeaturePython] InvoluteGear004  # WARN: FeaturePython — macro-defined, semantics opaque (R4)
  AttacherType = Attacher::AttachEngine3D
  Placement = pos=(0,0,-12.4) rot=(0,0,1;0rad)
  angular_backlash = 0
  backlash = 0
  beta = 0
  clearance = 0.25
  da = 65
  df = 60.5
  double_helix = false
  dw = 63
  head = 0
  head_fillet = 0
  height = 5
  module = 1
  numpoints = 6
  pressure_angle = 20
  properties_from_tool = false
  reversed_backlash = false
  root_fillet = 0
  shift = 0
  simple = false
  teeth = 63
  transverse_pitch = 3.14159
  traverse_module = 1
  undercut = false
  version = 0.0.4
  expr: angular_backlash = backlash / dw * 360° / pi
FEATURE [PartDesign::FeatureBase] BaseFeature
  BaseFeature = -> InvoluteGear004
FEATURE [PartDesign::Pocket] Pocket004
  BaseFeature = -> BaseFeature
  Direction = (0,0,-1)
  Length = 12.7
  Length2 = 5.08
  Profile = -> Sketch023
  ReferenceAxis = -> Sketch023 [N_Axis]
  Reversed = true
  Type = 0
FEATURE [PartDesign::Body] Body006  label="BigGear"
  BaseFeature = -> InvoluteGear004
  Group = -> [BaseFeature,Sketch023,Pocket004]
  Origin = -> Origin014
  Placement = pos=(0,0,-12.1412) rot=(0,0,-1;0.174533rad)
  Tip = -> Pocket004
FEATURE [Sketcher::SketchObject] Sketch076
  AttachmentOffset = pos=(0,0,29.21) rot=(0,0,1;0rad)
  FullyConstrained = false
  MapMode = 5
  Placement = pos=(0,0,29.21) rot=(0,0,1;0rad)
  Support = -> [XY_Plane030]
  expr: Constraints[7] = Spreadsheet.PivotFrameRadius
  sketch-geometry (15):
    g0: Circle CenterX=0 CenterY=0 CenterZ=0 NormalX=0 NormalY=0 NormalZ=1 AngleXU=0 Radius=15.9
    g1: ArcOfCircle CenterX=0 CenterY=0 CenterZ=0 NormalX=0 NormalY=0 NormalZ=1 AngleXU=0 Radius=41.91 StartAngle=4.71239 EndAngle=6.46427
    g2: LineSegment StartX=41.2247 StartY=7.54784 StartZ=0 EndX=40.5483 EndY=11.2423 EndZ=0
    g3: LineSegment StartX=-4.4308 StartY=21.4434 StartZ=0 EndX=-17.2122 EndY=15.3247 EndZ=0
    g4: LineSegment StartX=40.5483 StartY=11.2423 StartZ=0 EndX=-4.4308 EndY=21.4434 EndZ=0
    g5: LineSegment StartX=-17.2122 StartY=15.3247 StartZ=0 EndX=-22.6585 EndY=-20.3025 EndZ=0
    g6: LineSegment StartX=-22.6585 StartY=-20.3025 StartZ=0 EndX=-7.1e-15 EndY=-41.91 EndZ=0
    g7: Circle CenterX=38.9941 CenterY=-0.680644 CenterZ=0 NormalX=0 NormalY=0 NormalZ=1 AngleXU=0 Radius=1.6
    g8: Circle CenterX=33.4295 CenterY=-20.0865 CenterZ=0 NormalX=0 NormalY=0 NormalZ=1 AngleXU=0 Radius=1.6
    g9: Circle CenterX=-0.680644 CenterY=-38.9941 CenterZ=0 NormalX=0 NormalY=0 NormalZ=1 AngleXU=0 Radius=1.6
    g10: Circle CenterX=18.9076 CenterY=-34.1102 CenterZ=0 NormalX=0 NormalY=0 NormalZ=1 AngleXU=0 Radius=1.6
    g11: LineSegment StartX=0 StartY=0 StartZ=0 EndX=38.9941 EndY=-0.680644 EndZ=0
    g12: LineSegment StartX=0 StartY=0 StartZ=0 EndX=33.4295 EndY=-20.0865 EndZ=0
    g13: LineSegment StartX=0 StartY=0 StartZ=0 EndX=18.9076 EndY=-34.1102 EndZ=0
    g14: LineSegment StartX=0 StartY=0 StartZ=0 EndX=-0.680644 EndY=-38.9941 EndZ=0
  constraints (31):
    c: Coincident(g0,g-1)
    c: Diameter(g0) = 31.8
    c: Tangent(g1,g2) = -1.5708
    c: Coincident(g1,g0)
    c: Coincident(g4,g2)
    c: Coincident(g4,g3)
    c: Coincident(g5,g3)
    c: Diameter(g1) = 83.82
    c: PointOnObject(g1,g-2)
    c: Coincident(g5,g6)
    c: Coincident(g6,g1)
    c: Coincident(g11,g0)
    c: Coincident(g11,g7)
    c: Coincident(g12,g0)
    c: Coincident(g12,g8)
    c: Coincident(g13,g0)
    c: Coincident(g13,g10)
    c: Coincident(g14,g0)
    c: Coincident(g14,g9)
    c: Equal(g14,g13)
    c: Equal(g13,g12)
    c: Equal(g12,g11)
    c: Equal(g10,g7)
    c: Equal(g7,g8)
    c: Equal(g8,g9)
    c: Diameter(g7) = 3.2
    c: Distance(g11) = 39
    c: Angle(g12,g11) = 0.523599
    c: Angle(g13,g12) = 0.523599
    c: Angle(g14,g13) = 0.523599
    c: Angle(g11,g-1) = 0.0174533
FEATURE [PartDesign::Pocket] Pocket028
  BaseFeature = -> Pocket023
  Direction = (0,0,-1)
  Length = 6
  Length2 = 5
  Profile = -> Sketch027
  ReferenceAxis = -> Sketch027 [N_Axis]
  TaperAngle = -2
  Type = 0
FEATURE [PartDesign::Body] Body004  label="PivotFrame"
  Group = -> [Sketch009,Pad005,Sketch010,Pad006,Sketch011,Pad007,Sketch024,Sketch026,Pad009,Sketch027,Sketch030,Sketch036,Pocket011,Pocket012,Pocket013,Sketch054,Pocket020,Sketch062,Pad024,Sketch063,Pocket023,Pocket028]
  Origin = -> Origin011
  Placement = pos=(0,0,-21.6916) rot=(0,0,1;0rad)
  Tip = -> Pocket028
FEATURE [PartDesign::Pad] Pad031
  Direction = (0,0,1)
  Length = 3.5
  Length2 = 10
  Profile = -> Sketch076
  ReferenceAxis = -> Sketch076 [N_Axis]
  Type = 0
FEATURE [PartDesign::Body] Body017  label="PivotTop"
  Group = -> [Sketch076,Pad031]
  Origin = -> Origin030
  Placement = pos=(0,0,-21.5) rot=(0,0,1;0rad)
  Tip = -> Pad031
FEATURE [Part::Feature] Part__Feature062  label="serv.Part4"
  Placement = pos=(-4.02078,15.6669,12.738) rot=(1,0,0;3.14159rad)
  shape: bbox 23 x 11.2 x 12 mm, 86 faces, 3 solids (baked)
FEATURE [Part::Feature] Part__Feature063  label="serv.Part1_2"
  Placement = pos=(-4.97345,17.9768,13.1998) rot=(0.707107,0,0.707107;3.14159rad)
  shape: bbox 9.5 x 4.826 x 9.5 mm, 79 faces (baked)
FEATURE [Part::Feature] Part__Feature064  label="serv.Part2"
  Placement = pos=(1.97922,11.6669,18.738) rot=(-0.180943,-0.180943,0.966705;1.60465rad)
  shape: bbox 8.458 x 14 x 8.332 mm, 65 faces (baked)
FEATURE [Part::Feature] Part__Feature065  label="serv.Part1_1"
  Placement = pos=(7.57184,13.1764,20.0943) rot=(0.074955,0.510274,0.85674;4.08526rad)
  shape: bbox 1.75 x 1.576 x 1.638 mm, 27 faces (baked)
FEATURE [Part::Feature] Part__Feature066  label="scrow"
  Placement = pos=(3.63518,0.48995,7.54294) rot=(0,0,1;0rad)
  shape: bbox 1 x 10.78 x 1 mm, 8 faces (baked)
FEATURE [Part::Feature] Part__Feature067  label="spur gear_iso_ISO - Spur gear 0.25M 39T 20PA 1FW ---S39A75H50L1.0N"
  Placement = pos=(3.63518,0.48995,7.54294) rot=(-0.402145,-0.402145,0.822531;1.76493rad)
  shape: bbox 10.25 x 1 x 10.24 mm, 164 faces (baked)
FEATURE [Part::Feature] Part__Feature068  label="spur gear_iso_ISO - Spur gear 0.25M 10T 20PA 1.75FW ---S10A75H50L1.0N"
  Placement = pos=(3.63518,1.48995,7.54294) rot=(-0.566707,-0.566707,0.59807;2.06359rad)
  shape: bbox 2.998 x 1.75 x 2.915 mm, 49 faces (baked)
FEATURE [App::Part] gear_sub1
  Group = -> [Part__Feature066,Part__Feature067,Part__Feature068]
  Origin = -> Origin031
  Placement = pos=(5.13569,15.652,26.5654) rot=(0,1,0;2.32946rad)
FEATURE [Part::Feature] Part__Feature069  label="spur gear_iso_ISO - Spur gear 0.25M 39T 20PA 1FW ---S39A75H50L1.0N001"
  Placement = pos=(3.63518,0.58995,7.54294) rot=(-0.566707,-0.566707,0.59807;2.06359rad)
  shape: bbox 10.24 x 1 x 10.25 mm, 164 faces (baked)
FEATURE [Part::Feature] Part__Feature070  label="spur gear_iso_ISO - Spur gear 0.25M 10T 20PA 1.75FW ---S10A75H50L1.0N001"
  Placement = pos=(3.63518,1.58995,7.54294) rot=(-0.566707,-0.566707,0.59807;2.06359rad)
  shape: bbox 2.998 x 1.75 x 2.915 mm, 49 faces (baked)
FEATURE [App::Part] gear_sub2
  Group = -> [Part__Feature069,Part__Feature070]
  Origin = -> Origin032
  Placement = pos=(8.10365,16.927,13.0282) rot=(0,-1,0;1.26951rad)
FEATURE [Part::Feature] Part__Feature071  label="spur gear_iso_ISO - Spur gear 0.25M 39T 20PA 1FW ---S39A75H50L1.0N002"
  Placement = pos=(4.585,-0.563843,8.48204) rot=(-0.566707,-0.566707,0.59807;2.06359rad)
  shape: bbox 10.24 x 1 x 10.25 mm, 164 faces (baked)
FEATURE [Part::Feature] Part__Feature072  label="spur gear_iso_ISO - Spur gear 0.25M 10T 20PA 6FW ---S10A75H50L1.0N"
  Placement = pos=(4.585,6.43616,8.48204) rot=(0.541603,-0.541603,-0.642909;1.99884rad)
  shape: bbox 2.967 x 6 x 2.978 mm, 49 faces (baked)
FEATURE [App::Part] gear_sub3
  Group = -> [Part__Feature071,Part__Feature072]
  Origin = -> Origin033
  Placement = pos=(15.6535,19.4558,12.7337) rot=(0,-1,0;1.39414rad)
FEATURE [Part::Feature] Part__Feature073  label="gear_sub4"
  Placement = pos=(9.01392,24.755,13.5968) rot=(-0.396635,-0.396635,0.827865;1.75859rad)
  shape: bbox 10.24 x 7.5 x 10.25 mm, 326 faces (baked)
FEATURE [Part::Feature] Part__Feature074  label="serv.Part8"
  Placement = pos=(3.36076,8.68633,18.738) rot=(0.976296,0.21644,0;3.14159rad)
  shape: bbox 9.486 x 5.132 x 9 mm, 178 faces, 10 solids (baked)
FEATURE [Part::Feature] Part__Feature075  label="wire^servo"
  shape: bbox 1.983 x 1.765 x 7.995 mm, 8 faces, 2 solids (baked)
FEATURE [Part::Feature] Part__Feature076  label="TapaCarcasaDcMotor_Predeterminado"
  shape: bbox 9.23 x 7.862 x 5.006 mm, 212 faces (baked)
FEATURE [Part::Feature] Part__Feature077  label="RondanaDcMotor_Predeterminado"
  Placement = pos=(1.75486e-07,-1.65959e-07,-4.15397) rot=(0,0,1;2.71138rad)
  shape: bbox 2.73 x 2.73 x 1.365 mm, 14 faces (baked)
FEATURE [Part::Feature] Part__Feature078  label="Soportede Cobre_Predeterminado"
  Placement = pos=(-2.41575,-0.0897276,0.823647) rot=(0,1,0;3.14159rad)
  shape: bbox 3.114 x 2.853 x 3.235 mm, 31 faces (baked)
FEATURE [Part::Feature] Part__Feature079  label="CarcasaDcMotor_Predeterminado"
  Placement = pos=(-5.53376e-05,-0.00206495,2.43784) rot=(0,0,1;0rad)
  shape: bbox 9.11 x 8.642 x 9.443 mm, 124 faces (baked)
FEATURE [Part::Feature] Part__Feature080  label="Arcometalico_Predeterminado"
  Placement = pos=(-1e-14,3.51437,-4.58863) rot=(1,0,0;3.14159rad)
  shape: bbox 4.074 x 0.455 x 7.269 mm, 42 faces (baked)
FEATURE [Part::Feature] Part__Feature081  label="AislanteDcMotor_Predeterminado"
  Placement = pos=(-4.0652,-0.155865,-3.42147) rot=(0,0,1;0.038322rad)
  shape: bbox 2.8 x 6.299 x 5.46 mm, 44 faces (baked)
FEATURE [Part::Feature] Part__Feature082  label="AislanteDcMotor_Predeterminado001"
  Placement = pos=(4.0652,-0.155865,8.57853) rot=(0.01916,0.999816,0;3.14159rad)
  shape: bbox 2.8 x 6.299 x 5.46 mm, 44 faces (baked)
FEATURE [Part::Feature] Part__Feature083  label="Rondana2DcMotor_Predeterminado"
  Placement = pos=(1.75486e-07,-1.65959e-07,8.69605) rot=(0.510656,0.859785,0;3.14159rad)
  shape: bbox 2.598 x 2.598 x 0.7963 mm, 14 faces (baked)
FEATURE [Part::Feature] Part__Feature084  label="Soportede Cobre_Predeterminado001"
  Placement = pos=(2.41575,0.0897276,0.823647) rot=(1,0,0;3.14159rad)
  shape: bbox 3.114 x 2.853 x 3.235 mm, 31 faces (baked)
FEATURE [App::Part] DcMotor_Emsamblaje_Final_Predeterminado  label="DcMotor Emsamblaje Final_Predeterminado"
  Group = -> [Part__Feature076,Part__Feature077,Part__Feature078,Part__Feature079,Part__Feature080,Part__Feature081,Part__Feature082,Part__Feature083,Part__Feature084]
  Origin = -> Origin034
  Placement = pos=(14.2292,7.0834,18.738) rot=(0.57735,0.57735,0.57735;4.18879rad)
FEATURE [Part::Feature] Part__Feature085  label="spur gear_iso_ISO - Spur gear 0.25M 10T 20PA 2FW ---S10A75H50L1.0N"
  Placement = pos=(14.2292,15.6419,18.738) rot=(0.058415,0.058415,0.996582;1.57422rad)
  shape: bbox 2.954 x 2 x 2.986 mm, 49 faces (baked)
FEATURE [Part::Feature] Part__Feature086  label="Rotor_Predeterminado"
  Placement = pos=(14.2292,10.7797,18.738) rot=(-0.595076,-0.56828,-0.56828;2.06801rad)
  shape: bbox 5.726 x 16.91 x 5.786 mm, 3722 faces, 129 solids (baked)
FEATURE [Part::Feature] Part__Feature087  label="serv.Part5"
  Placement = pos=(-4.02078,15.6669,24.738) rot=(0,0,1;0rad)
  shape: bbox 32 x 11 x 12.99 mm, 302 faces (baked)
FEATURE [Part::Feature] Part__Feature088  label="serv.Part3"
  Placement = pos=(18.9792,0.66693,12.738) rot=(0,0.707107,0.707107;3.14159rad)
  shape: bbox 23 x 5 x 12 mm, 96 faces (baked)
FEATURE [Part::Feature] Part__Feature089  label="serv.Part6"
  Placement = pos=(17.7292,0.31693,23.488) rot=(0,0,1;1.5708rad)
  shape: bbox 2.165 x 20 x 2.165 mm, 58 faces (baked)
FEATURE [Part::Feature] Part__Feature090  label="serv.Part009"
  Placement = pos=(-2.77078,0.31693,23.488) rot=(0.429756,0.429756,0.794115;1.79931rad)
  shape: bbox 2.119 x 20 x 2.119 mm, 58 faces (baked)
FEATURE [Part::Feature] Part__Feature091  label="serv.Part010"
  Placement = pos=(17.7292,0.31693,13.988) rot=(0.429756,0.429756,0.794115;1.79931rad)
  shape: bbox 2.119 x 20 x 2.119 mm, 58 faces (baked)
FEATURE [Part::Feature] Part__Feature092  label="serv.Part011"
  Placement = pos=(-2.77078,0.31693,13.988) rot=(0.301511,0.301511,0.904534;1.67096rad)
  shape: bbox 2.144 x 20 x 2.144 mm, 58 faces (baked)
FEATURE [Part::Feature] Part__Feature093  label="serv.Part7 servo hourn "
  Placement = pos=(-12.7504,33.3919,17.962) rot=(0.597604,0.566952,-0.566952;2.06428rad)
  shape: bbox 34.46 x 5 x 6.955 mm, 201 faces (baked)
FEATURE [App::Part] servo
  Group = -> [Part__Feature062,Part__Feature063,Part__Feature064,Part__Feature065,gear_sub1,gear_sub2,gear_sub3,Part__Feature073,Part__Feature074,Part__Feature075,DcMotor_Emsamblaje_Final_Predeterminado,Part__Feature085,Part__Feature086,Part__Feature087,Part__Feature088,Part__Feature089,Part__Feature090,Part__Feature091,Part__Feature092,Part__Feature093]
  Origin = -> Origin035
  Placement = pos=(26.5629,42.4873,17.8) rot=(-0.6444,-0.540716,0.540716;1.99673rad)
FEATURE [PartDesign::Body] Body018  label="RotatingFunnel"
  Origin = -> Origin036
FEATURE [Sketcher::SketchObject] Sketch077
  FullyConstrained = false
  MapMode = 5
  Support = -> [XY_Plane037]
  sketch-geometry (16):
    g0: Circle CenterX=0 CenterY=14 CenterZ=0 NormalX=0 NormalY=0 NormalZ=1 AngleXU=0 Radius=0.4
    g1: Circle CenterX=0 CenterY=-14 CenterZ=0 NormalX=0 NormalY=0 NormalZ=1 AngleXU=0 Radius=0.4
    g2: LineSegment StartX=-6.25 StartY=-11.5 StartZ=0 EndX=6.25 EndY=-11.5 EndZ=0
    g3: LineSegment StartX=6.25 StartY=-11.5 StartZ=0 EndX=6.25 EndY=11.5 EndZ=0
    g4: LineSegment StartX=6.25 StartY=11.5 StartZ=0 EndX=-6.25 EndY=11.5 EndZ=0
    g5: LineSegment StartX=-6.25 StartY=11.5 StartZ=0 EndX=-6.25 EndY=-11.5 EndZ=0
    g6: Circle CenterX=-7.96029 CenterY=-26.5613 CenterZ=0 NormalX=0 NormalY=0 NormalZ=1 AngleXU=0 Radius=2.45261
    g7: Circle CenterX=7.28309 CenterY=-26.7995 CenterZ=0 NormalX=0 NormalY=0 NormalZ=1 AngleXU=0 Radius=2.45261
    g8: LineSegment StartX=-12.3013 StartY=9.58319 StartZ=0 EndX=-9.10633 EndY=18.8134 EndZ=0
    g9: LineSegment StartX=-9.10633 StartY=18.8134 StartZ=0 EndX=9.10633 EndY=18.8134 EndZ=0
    g10: LineSegment StartX=9.10633 StartY=18.8134 StartZ=0 EndX=11.5295 EndY=10.5367 EndZ=0
    g11: LineSegment StartX=11.5295 StartY=10.5367 StartZ=0 EndX=16.2743 EndY=-22.1551 EndZ=0
    g12: LineSegment StartX=16.2743 StartY=-22.1551 StartZ=0 EndX=13.7541 EndY=-32.0047 EndZ=0
    g13: LineSegment StartX=13.7541 StartY=-32.0047 StartZ=0 EndX=-13.7831 EndY=-32.0047 EndZ=0
    g14: LineSegment StartX=-13.7831 StartY=-32.0047 StartZ=0 EndX=-15.9988 EndY=-22.7505 EndZ=0
    g15: LineSegment StartX=-15.9988 StartY=-22.7505 StartZ=0 EndX=-12.3013 EndY=9.58319 EndZ=0
  constraints (26):
    c: PointOnObject(g0,g-2)
    c: Symmetric(g1,g0,g-1)
    c: Equal(g1,g0)
    c: Coincident(g2,g3)
    c: Coincident(g3,g4)
    c: Coincident(g4,g5)
    c: Coincident(g5,g2)
    c: Horizontal(g2)
    c: Vertical(g5)
    c: Symmetric(g4,g3,g-2)
    c: DistanceY(g3,g3) = 23
    c: Symmetric(g3,g2,g-1)
    c: DistanceY(g1,g0) = 28
    c: DistanceX(g4,g4) = 12.5
    c: Diameter(g0) = 0.8
    c: Equal(g6,g7)
    c: Coincident(g9,g8)
    c: Coincident(g9,g10)
    c: Coincident(g10,g11)
    c: Coincident(g11,g12)
    c: Coincident(g12,g13)
    c: Horizontal(g13)
    c: Coincident(g13,g14)
    c: Coincident(g14,g15)
    c: Coincident(g15,g8)
    c: Symmetric(g8,g9,g-2)
FEATURE [Sketcher::SketchObject] Sketch078
  FullyConstrained = false
  MapMode = 5
  Placement = pos=(0,0,0) rot=(0,1,0;3.14159rad)
  Support = -> [XY_Plane037]
  sketch-geometry (7):
    g0: ArcOfCircle CenterX=0 CenterY=0 CenterZ=0 NormalX=0 NormalY=0 NormalZ=1 AngleXU=0 Radius=21.9404 StartAngle=1.19577 EndAngle=2.14643
    g1: LineSegment StartX=8.0367 StartY=20.4156 StartZ=0 EndX=12.75 EndY=0 EndZ=0
    g2: ArcOfCircle CenterX=0 CenterY=0 CenterZ=0 NormalX=0 NormalY=0 NormalZ=1 AngleXU=0 Radius=32.4633 StartAngle=1.40499 EndAngle=2.12098
    g3: LineSegment StartX=5.35804 StartY=32.0181 StartZ=0 EndX=8.0367 EndY=20.4156 EndZ=0
    g4: LineSegment StartX=-16.9731 StartY=27.6727 StartZ=0 EndX=-11.9437 EndY=18.4047 EndZ=0
    g5: Circle CenterX=-12.2657 CenterY=25.6173 CenterZ=0 NormalX=0 NormalY=0 NormalZ=1 AngleXU=0 Radius=1.55
    g6: Circle CenterX=2.47211 CenterY=28.4094 CenterZ=0 NormalX=0 NormalY=0 NormalZ=1 AngleXU=0 Radius=1.55
  constraints (14):
    c: Coincident(g0,g-1)
    c: Coincident(g1,g0)
    c: PointOnObject(g1,g-1)
    c: Angle(g1,g-1) = 1.3439
    c: Coincident(g2,g0)
    c: Coincident(g3,g2)
    c: Coincident(g3,g0)
    c: Coincident(g4,g2)
    c: Coincident(g4,g0)
    c: Equal(g6,g5)
    c: Diameter(g5) = 3.1
    c: Distance(g5,g6) = 15
    c: Parallel(g3,g1)
    c: DistanceX(g0,g1) = 12.75
FEATURE [PartDesign::Pad] Pad032
  Direction = (0,0,1)
  Length = 3
  Length2 = 10
  Profile = -> Sketch077
  ReferenceAxis = -> Sketch077 [N_Axis]
  Reversed = true
  Type = 0
FEATURE [PartDesign::Body] Body019  label="ServoMnt"
  Group = -> [Sketch077,Sketch078,Pad032]
  Origin = -> Origin037
  Placement = pos=(9.377,53.1796,5) rot=(0,0,-1;0.174533rad)
  Tip = -> Pad032
FEATURE [Sketcher::SketchObject] Sketch079
  FullyConstrained = true
  MapMode = 5
  Support = -> [XY_Plane038]
  sketch-geometry (8):
    g0: Circle CenterX=0 CenterY=0 CenterZ=0 NormalX=0 NormalY=0 NormalZ=1 AngleXU=0 Radius=2.05
    g1: LineSegment StartX=0 StartY=5.5 StartZ=0 EndX=-4.76314 EndY=2.75 EndZ=0
    g2: LineSegment StartX=-4.76314 StartY=2.75 StartZ=0 EndX=-4.76314 EndY=-2.75 EndZ=0
    g3: LineSegment StartX=-4.76314 StartY=-2.75 StartZ=0 EndX=3.14797e-11 EndY=-5.5 EndZ=0
    g4: LineSegment StartX=3.14797e-11 StartY=-5.5 StartZ=0 EndX=4.76314 EndY=-2.75 EndZ=0
    g5: LineSegment StartX=4.76314 StartY=-2.75 StartZ=0 EndX=4.76314 EndY=2.75 EndZ=0
    g6: LineSegment StartX=4.76314 StartY=2.75 StartZ=0 EndX=0 EndY=5.5 EndZ=0
    g7: Circle CenterX=0 CenterY=0 CenterZ=0 NormalX=0 NormalY=0 NormalZ=1 AngleXU=0 Radius=5.5
  constraints (18):
    c: Coincident(g0,g-1)
    c: Diameter(g0) = 4.1
    c: Coincident(g1,g2)
    c: Coincident(g2,g3)
    c: Coincident(g3,g4)
    c: Coincident(g4,g5)
    c: Coincident(g5,g6)
    c: Coincident(g6,g1)
    c: Equal(g1, g2-g6) x5
    c: PointOnObject(g1,g7)
    c: PointOnObject(g2,g7)
    c: PointOnObject(g3,g7)
    c: PointOnObject(g4,g7)
    c: PointOnObject(g5,g7)
    c: PointOnObject(g6,g7)
    c: Coincident(g7,g0)
    c: PointOnObject(g6,g-2)
    c: Diameter(g7) = 11
FEATURE [Sketcher::SketchObject] Sketch080
  AttachmentOffset = pos=(0,0,-3.6) rot=(0,0,1;0rad)
  FullyConstrained = false
  MapMode = 5
  Placement = pos=(0,0,-3.6) rot=(0,0,1;0rad)
  Support = -> [XY_Plane038]
  sketch-geometry (9):
    g0: Circle CenterX=0 CenterY=0 CenterZ=0 NormalX=0 NormalY=0 NormalZ=1 AngleXU=0 Radius=1.25
    g1: Circle CenterX=-7.7 CenterY=-55.2 CenterZ=0 NormalX=0 NormalY=0 NormalZ=1 AngleXU=0 Radius=2
    g2: LineSegment StartX=-7.94398 StartY=0.937797 StartZ=0 EndX=-14.6377 EndY=-55.7644 EndZ=0
    g3: LineSegment StartX=-12.4441 StartY=-59.1932 StartZ=0 EndX=-5.52132 EndY=-61.4491 EndZ=0
    g4: LineSegment StartX=7.89798 StartY=-1.26818 StartZ=0 EndX=-1.3569 EndY=-58.9056 EndZ=0
    g5: ArcOfCircle CenterX=0 CenterY=0 CenterZ=0 NormalX=0 NormalY=0 NormalZ=1 AngleXU=0 Radius=7.99914 StartAngle=6.12397 EndAngle=9.30727
    g6: ArcOfCircle CenterX=-11.4495 CenterY=-56.1408 CenterZ=0 NormalX=0 NormalY=0 NormalZ=1 AngleXU=0 Radius=3.21038 StartAngle=3.02409 EndAngle=4.39738
    g7: ArcOfCircle CenterX=-4.52668 CenterY=-58.3966 CenterZ=0 NormalX=0 NormalY=0 NormalZ=1 AngleXU=0 Radius=3.21038 StartAngle=4.39738 EndAngle=6.12397
    g8: LineSegment StartX=-14.3851 StartY=-53.6242 StartZ=0 EndX=-1.0149 EndY=-56.7758 EndZ=0
  constraints (16):
    c: Coincident(g0,g-1)
    c: Diameter(g0) = 2.5
    c: DistanceX(g1,g-1) = 7.7
    c: Coincident(g5,g0)
    c: Tangent(g5,g2) = -1.5708
    c: Tangent(g5,g4) = 1.5708
    c: Tangent(g2,g6) = -1.5708
    c: Tangent(g3,g6) = -1.5708
    c: Tangent(g3,g7) = -1.5708
    c: Tangent(g4,g7) = 1.5708
    c: Equal(g7,g6)
    c: PointOnObject(g8,g2)
    c: PointOnObject(g8,g4)
    c: Symmetric(g8,g8,g1)
    c: Diameter(g1) = 4
    c: DistanceY(g1,g0) = 55.2
FEATURE [Sketcher::SketchObject] Sketch081
  AttachmentOffset = pos=(0,0,-5) rot=(0,0,1;0rad)
  FullyConstrained = true
  MapMode = 5
  Placement = pos=(0,0,-5) rot=(0,0,1;0rad)
  Support = -> [XY_Plane038]
  sketch-geometry (1):
    g0: Circle CenterX=0 CenterY=0 CenterZ=0 NormalX=0 NormalY=0 NormalZ=1 AngleXU=0 Radius=2
  constraints (2):
    c: Coincident(g0,g-1)
    c: Diameter(g0) = 4
FEATURE [Sketcher::SketchObject] Sketch082
  AttachmentOffset = pos=(0,0,-3.6) rot=(0,0,1;0rad)
  FullyConstrained = false
  MapMode = 5
  Placement = pos=(0,0,-3.6) rot=(0,0,1;0rad)
  Support = -> [XY_Plane038]
  sketch-geometry (7):
    g0: Circle CenterX=0 CenterY=0 CenterZ=0 NormalX=0 NormalY=0 NormalZ=1 AngleXU=0 Radius=1.25
    g1: Circle CenterX=-7.7 CenterY=-55.2 CenterZ=0 NormalX=0 NormalY=0 NormalZ=1 AngleXU=0 Radius=2
    g2: LineSegment StartX=-7.94624 StartY=0.813158 StartZ=0 EndX=-13.899 EndY=-57.358 EndZ=0
    g3: LineSegment StartX=-13.899 StartY=-57.358 StartZ=0 EndX=-3.31271 EndY=-59.106 EndZ=0
    g4: LineSegment StartX=7.84198 StartY=-1.519 StartZ=0 EndX=-3.31271 EndY=-59.106 EndZ=0
    g5: ArcOfCircle CenterX=0 CenterY=0 CenterZ=0 NormalX=0 NormalY=0 NormalZ=1 AngleXU=0 Radius=7.98774 StartAngle=6.09185 EndAngle=9.3228
    g6: Circle CenterX=-7.7 CenterY=-55.2 CenterZ=0 NormalX=0 NormalY=0 NormalZ=1 AngleXU=0 Radius=5.05002
  constraints (12):
    c: Coincident(g0,g-1)
    c: Diameter(g0) = 2.5
    c: DistanceX(g1,g-1) = 7.7
    c: DistanceY(g1,g0) = 55.2
    c: Coincident(g3,g2)
    c: Coincident(g4,g3)
    c: Coincident(g5,g0)
    c: Tangent(g5,g2) = -1.5708
    c: Tangent(g5,g4) = 1.5708
    c: Coincident(g6,g1)
    c: Tangent(g6,g4)
    c: Diameter(g1) = 4
FEATURE [PartDesign::Pad] Pad033
  Direction = (0,0,1)
  Length = 3.6
  Length2 = 10
  Profile = -> Sketch079
  ReferenceAxis = -> Sketch079 [N_Axis]
  Reversed = true
  Type = 0
FEATURE [PartDesign::Pad] Pad034
  BaseFeature = -> Pad033
  Direction = (0,0,1)
  Length = 4
  Length2 = 10
  Profile = -> Sketch080
  ReferenceAxis = -> Sketch080 [N_Axis]
  Reversed = true
  Type = 0
FEATURE [PartDesign::Pocket] Pocket029
  BaseFeature = -> Pad034
  Direction = (0,0,-1)
  Length = 5
  Length2 = 5
  Profile = -> Sketch081
  ReferenceAxis = -> Sketch081 [N_Axis]
  Type = 0
FEATURE [PartDesign::Chamfer] Chamfer
  Angle = 65
  Base = -> Pocket029 [Edge25]
  BaseFeature = -> Pocket029
  ChamferType = 2
  FlipDirection = false
  Size = 1.2
  Size2 = 1
  SupportTransform = false
  UseAllEdges = false
FEATURE [PartDesign::Pad] Pad035
  BaseFeature = -> Chamfer
  Direction = (0,0,1)
  Length = 10
  Length2 = 10
  Profile = -> Sketch082
  ReferenceAxis = -> Sketch082 [N_Axis]
  Type = 0
FEATURE [PartDesign::Chamfer] Chamfer010
  Angle = 35
  Base = -> Pad035 [Edge35]
  BaseFeature = -> Pad035
  ChamferType = 2
  FlipDirection = false
  Size = 4
  Size2 = 1
  SupportTransform = false
  UseAllEdges = false
FEATURE [PartDesign::Chamfer] Chamfer011
  Angle = 75
  Base = -> Chamfer010 [Edge53]
  BaseFeature = -> Chamfer010
  ChamferType = 2
  FlipDirection = false
  Size = 0.3
  Size2 = 1
  SupportTransform = false
  UseAllEdges = false
FEATURE [PartDesign::Body] Body020  label="ServoTop"
  Group = -> [Sketch079,Pad033,Sketch080,Pad034,Sketch081,Pocket029,Chamfer,Sketch082,Pad035,Chamfer010,Chamfer011]
  Origin = -> Origin038
  Placement = pos=(8.42194,47.7632,-13.2) rot=(0,0,-1;0.174533rad)
  Tip = -> Chamfer011
FEATURE [App::Part] Part004  label="Outlet"
  Group = -> [Body011,Part__Feature059,Body012,Part005,Part__Feature060,Body018,servo,Body019,Body020]
  Origin = -> Origin020
  Placement = pos=(0,0,-27.2) rot=(0,0,1;5.74213rad)
FEATURE [App::Part] Part001  label="Feeder"
  Group = -> [Body004,InvoluteGear,_8BYJ_48_Stepper_Motor,Body007,Part__Feature057,Body008,InvoluteGear003,Body010,NEMA_17,Body006,Part__Feature061,Part006,Part004,InvoluteGear004,Body017]
  Origin = -> Origin008
  Placement = pos=(0,0,0) rot=(0,0,-1;5.75959rad)
FEATURE [App::Part] Part  label="MMU"
  Group = -> [Body,Body002,Body003,Part001,Part003,Part002,bearing_w_61705_2rs1_2_1,bearing_w_61705_2rs1_2_002,Body009,Part__Feature058,Body013]
  Origin = -> Origin003
FEATURE [Mesh::Feature] Mesh  label="ServoTop (Meshed)"
